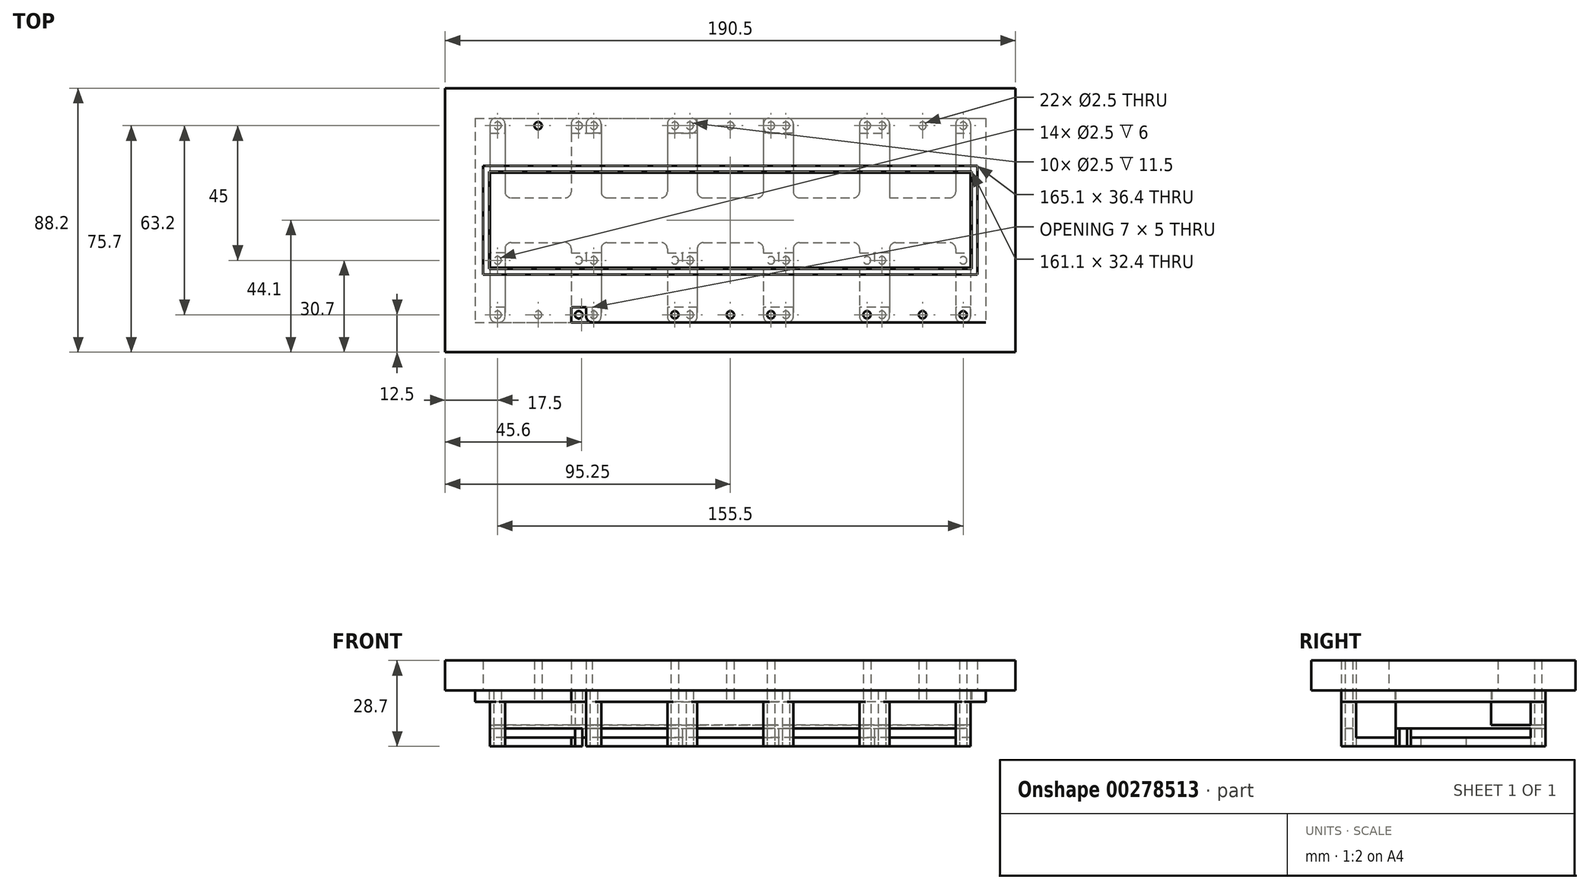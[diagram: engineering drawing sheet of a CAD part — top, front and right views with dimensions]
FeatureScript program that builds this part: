
annotation { "Feature Type Name" : "Feature", "Feature Type Description" : "" }
export const myFeature = defineFeature(function(context is Context, id is Id, definition is map)
    precondition{}
    {
        {
            var Q0;
            Q0=qCreatedBy(makeId("Top.planeOp"),FACE);
            var sketch = newSketch(context, id + "F0", { "sketchPlane" : qUnion([Q0])});
            skLineSegment(sketch, "E0.bottom", {"start": v(0, 0) * mm, "end": v(32.1, 0) * mm});
            skLineSegment(sketch, "E0.top", {"start": v(0, 50) * mm, "end": v(32.1, 50) * mm});
            skLineSegment(sketch, "E0.left", {"start": v(0, 0) * mm, "end": v(0, 50) * mm});
            skLineSegment(sketch, "E0.right", {"start": v(32.1, 0) * mm, "end": v(32.1, 50) * mm});
            skLineSegment(sketch, "E1", {"start": v(0, 31.8) * mm, "end": v(32.1, 31.8) * mm, "construction": true});
            skLineSegment(sketch, "E2", {"start": v(0, -18.2) * mm, "end": v(32.1, -18.2) * mm});
            skLineSegment(sketch, "E3", {"start": v(0, 0) * mm, "end": v(0, -18.2) * mm});
            skLineSegment(sketch, "E4", {"start": v(32.1, -18.2) * mm, "end": v(32.1, 0) * mm});
            skLineSegment(sketch, "E5", {"start": v(16.05, 50) * mm, "end": v(16.05, -18.2) * mm, "construction": true});
            skLineSegment(sketch, "E6", {"start": v(61.63, 15.9) * mm, "end": v(-27.1, 15.9) * mm, "construction": true});
            skPoint(sketch, "E6.startSnap0", {"position": v(16.05, 15.9) * mm});
            skCircle(sketch, "E7", {"center": v(2.5, 47.5) * mm, "radius": 1.25 * mm});
            skCircle(sketch, "E8.MirrorC", {"center": v(29.6, 47.5) * mm, "radius": 1.25 * mm});
            skCircle(sketch, "E9.MirrorC", {"center": v(29.6, -15.7) * mm, "radius": 1.25 * mm});
            skCircle(sketch, "E10.MirrorC", {"center": v(2.5, -15.7) * mm, "radius": 1.25 * mm});
            skCircle(sketch, "E11.1.0.0", {"center": v(61.7, 47.5) * mm, "radius": 1.25 * mm});
            skCircle(sketch, "E11.1.0.1", {"center": v(34.6, 47.5) * mm, "radius": 1.25 * mm});
            skCircle(sketch, "E11.1.0.2", {"center": v(34.6, -15.7) * mm, "radius": 1.25 * mm});
            skCircle(sketch, "E11.1.0.3", {"center": v(61.7, -15.7) * mm, "radius": 1.25 * mm});
            skLineSegment(sketch, "E11.1.0.4", {"start": v(32.1, 50) * mm, "end": v(64.2, 50) * mm});
            skLineSegment(sketch, "E11.1.0.5", {"start": v(32.1, -18.2) * mm, "end": v(64.2, -18.2) * mm});
            skCircle(sketch, "E11.2.0.0", {"center": v(93.8, 47.5) * mm, "radius": 1.25 * mm});
            skCircle(sketch, "E11.2.0.1", {"center": v(66.7, 47.5) * mm, "radius": 1.25 * mm});
            skCircle(sketch, "E11.2.0.2", {"center": v(66.7, -15.7) * mm, "radius": 1.25 * mm});
            skCircle(sketch, "E11.2.0.3", {"center": v(93.8, -15.7) * mm, "radius": 1.25 * mm});
            skLineSegment(sketch, "E11.2.0.4", {"start": v(64.2, 50) * mm, "end": v(96.3, 50) * mm});
            skLineSegment(sketch, "E11.2.0.5", {"start": v(64.2, -18.2) * mm, "end": v(96.3, -18.2) * mm});
            skCircle(sketch, "E11.3.0.0", {"center": v(125.9, 47.5) * mm, "radius": 1.25 * mm});
            skCircle(sketch, "E11.3.0.1", {"center": v(98.8, 47.5) * mm, "radius": 1.25 * mm});
            skCircle(sketch, "E11.3.0.2", {"center": v(98.8, -15.7) * mm, "radius": 1.25 * mm});
            skCircle(sketch, "E11.3.0.3", {"center": v(125.9, -15.7) * mm, "radius": 1.25 * mm});
            skLineSegment(sketch, "E11.3.0.4", {"start": v(96.3, 50) * mm, "end": v(128.4, 50) * mm});
            skLineSegment(sketch, "E11.3.0.5", {"start": v(96.3, -18.2) * mm, "end": v(128.4, -18.2) * mm});
            skCircle(sketch, "E11.4.0.0", {"center": v(158, 47.5) * mm, "radius": 1.25 * mm});
            skCircle(sketch, "E11.4.0.1", {"center": v(130.9, 47.5) * mm, "radius": 1.25 * mm});
            skCircle(sketch, "E11.4.0.2", {"center": v(130.9, -15.7) * mm, "radius": 1.25 * mm});
            skCircle(sketch, "E11.4.0.3", {"center": v(158, -15.7) * mm, "radius": 1.25 * mm});
            skLineSegment(sketch, "E11.4.0.4", {"start": v(128.4, 50) * mm, "end": v(160.5, 50) * mm});
            skLineSegment(sketch, "E11.4.0.5", {"start": v(128.4, -18.2) * mm, "end": v(160.5, -18.2) * mm});
            skLineSegment(sketch, "E11.direction1", {"start": v(29.6, 47.5) * mm, "end": v(61.7, 47.5) * mm, "construction": true});
            skLineSegment(sketch, "E12", {"start": v(160.5, 50) * mm, "end": v(160.5, -18.2) * mm});
            skSolve(sketch);
        }
        {
            var Q0;
            Q0=qCreatedBy(makeId("Top.planeOp"),FACE);
            var sketch = newSketch(context, id + "F1", { "sketchPlane" : qUnion([Q0])});
            skPoint(sketch, "E13.0", {"position": v(2.5, 47.5) * mm});
            skPoint(sketch, "E14.0", {"position": v(2.5, -15.7) * mm});
            skCircle(sketch, "E15", {"center": v(2.5, 47.5) * mm, "radius": 1.25 * mm});
            skCircle(sketch, "E16", {"center": v(2.5, -15.7) * mm, "radius": 1.25 * mm});
            skCircle(sketch, "E17", {"center": v(2.5, 2.5) * mm, "radius": 1.25 * mm});
            skCircle(sketch, "E18.MirrorC", {"center": v(29.6, 47.5) * mm, "radius": 1.25 * mm});
            skCircle(sketch, "E19.MirrorC", {"center": v(29.6, 2.5) * mm, "radius": 1.25 * mm});
            skCircle(sketch, "E20.MirrorC", {"center": v(29.6, -15.7) * mm, "radius": 1.25 * mm});
            skPoint(sketch, "E21.0", {"position": v(0, 50) * mm});
            skPoint(sketch, "E22.0", {"position": v(0, -18.2) * mm});
            skLineSegment(sketch, "E23.bottom", {"start": v(0, 50) * mm, "end": v(5, 50) * mm});
            skLineSegment(sketch, "E23.top", {"start": v(0, -18.2) * mm, "end": v(5, -18.2) * mm});
            skLineSegment(sketch, "E23.left", {"start": v(0, 50) * mm, "end": v(0, -18.2) * mm});
            skLineSegment(sketch, "E23.right", {"start": v(5, 50) * mm, "end": v(5, 23.4) * mm});
            skLineSegment(sketch, "E24.MirrorCS", {"start": v(27.1, 50) * mm, "end": v(27.1, 23.4) * mm});
            skLineSegment(sketch, "E25.MirrorCS", {"start": v(32.1, 50) * mm, "end": v(32.1, -18.2) * mm});
            skLineSegment(sketch, "E26.MirrorCS", {"start": v(32.1, 50) * mm, "end": v(27.1, 50) * mm});
            skLineSegment(sketch, "E27.MirrorCS", {"start": v(32.1, -18.2) * mm, "end": v(27.1, -18.2) * mm});
            skLineSegment(sketch, "E28", {"start": v(5, 23.4) * mm, "end": v(27.1, 23.4) * mm});
            skLineSegment(sketch, "E29", {"start": v(5, 15.9) * mm, "end": v(27.1, 15.9) * mm, "construction": true});
            skLineSegment(sketch, "E30.MirrorCS", {"start": v(5, 8.4) * mm, "end": v(27.1, 8.4) * mm});
            skLineSegment(sketch, "E31.trimOffspring", {"start": v(5, 8.4) * mm, "end": v(5, -18.2) * mm});
            skLineSegment(sketch, "E32.trimOffspring", {"start": v(27.1, 8.4) * mm, "end": v(27.1, -18.2) * mm});
            skPoint(sketch, "E33.1.0.0", {"position": v(32.1, -18.2) * mm});
            skLineSegment(sketch, "E33.1.0.1", {"start": v(37.1, 50) * mm, "end": v(37.1, 23.4) * mm});
            skPoint(sketch, "E33.1.0.2", {"position": v(34.6, -15.7) * mm});
            skLineSegment(sketch, "E33.1.0.3", {"start": v(59.2, 50) * mm, "end": v(59.2, 23.4) * mm});
            skLineSegment(sketch, "E33.1.0.4", {"start": v(64.2, 50) * mm, "end": v(64.2, -18.2) * mm});
            skPoint(sketch, "E33.1.0.5", {"position": v(34.6, 47.5) * mm});
            skLineSegment(sketch, "E33.1.0.6", {"start": v(64.2, 50) * mm, "end": v(59.2, 50) * mm});
            skPoint(sketch, "E33.1.0.7", {"position": v(32.1, 50) * mm});
            skLineSegment(sketch, "E33.1.0.8", {"start": v(37.1, 8.4) * mm, "end": v(37.1, -18.2) * mm});
            skLineSegment(sketch, "E33.1.0.9", {"start": v(59.2, 8.4) * mm, "end": v(59.2, -18.2) * mm});
            skLineSegment(sketch, "E33.1.0.10", {"start": v(37.1, 8.4) * mm, "end": v(59.2, 8.4) * mm});
            skLineSegment(sketch, "E33.1.0.11", {"start": v(64.2, -18.2) * mm, "end": v(59.2, -18.2) * mm});
            skLineSegment(sketch, "E33.1.0.12", {"start": v(37.1, 23.4) * mm, "end": v(59.2, 23.4) * mm});
            skLineSegment(sketch, "E33.1.0.13", {"start": v(37.1, 15.9) * mm, "end": v(59.2, 15.9) * mm, "construction": true});
            skLineSegment(sketch, "E33.1.0.15", {"start": v(32.1, -18.2) * mm, "end": v(37.1, -18.2) * mm});
            skCircle(sketch, "E33.1.0.16", {"center": v(34.6, 2.5) * mm, "radius": 1.25 * mm});
            skCircle(sketch, "E33.1.0.17", {"center": v(61.7, 47.5) * mm, "radius": 1.25 * mm});
            skCircle(sketch, "E33.1.0.18", {"center": v(61.7, 2.5) * mm, "radius": 1.25 * mm});
            skCircle(sketch, "E33.1.0.19", {"center": v(61.7, -15.7) * mm, "radius": 1.25 * mm});
            skLineSegment(sketch, "E33.1.0.20", {"start": v(32.1, 50) * mm, "end": v(37.1, 50) * mm});
            skCircle(sketch, "E33.1.0.21", {"center": v(34.6, 47.5) * mm, "radius": 1.25 * mm});
            skCircle(sketch, "E33.1.0.22", {"center": v(34.6, -15.7) * mm, "radius": 1.25 * mm});
            skPoint(sketch, "E33.2.0.0", {"position": v(64.2, -18.2) * mm});
            skLineSegment(sketch, "E33.2.0.1", {"start": v(69.2, 50) * mm, "end": v(69.2, 23.4) * mm});
            skPoint(sketch, "E33.2.0.2", {"position": v(66.7, -15.7) * mm});
            skLineSegment(sketch, "E33.2.0.3", {"start": v(91.3, 50) * mm, "end": v(91.3, 23.4) * mm});
            skLineSegment(sketch, "E33.2.0.4", {"start": v(96.3, 50) * mm, "end": v(96.3, -18.2) * mm});
            skPoint(sketch, "E33.2.0.5", {"position": v(66.7, 47.5) * mm});
            skLineSegment(sketch, "E33.2.0.6", {"start": v(96.3, 50) * mm, "end": v(91.3, 50) * mm});
            skPoint(sketch, "E33.2.0.7", {"position": v(64.2, 50) * mm});
            skLineSegment(sketch, "E33.2.0.8", {"start": v(69.2, 8.4) * mm, "end": v(69.2, -18.2) * mm});
            skLineSegment(sketch, "E33.2.0.9", {"start": v(91.3, 8.4) * mm, "end": v(91.3, -18.2) * mm});
            skLineSegment(sketch, "E33.2.0.10", {"start": v(69.2, 8.4) * mm, "end": v(91.3, 8.4) * mm});
            skLineSegment(sketch, "E33.2.0.11", {"start": v(96.3, -18.2) * mm, "end": v(91.3, -18.2) * mm});
            skLineSegment(sketch, "E33.2.0.12", {"start": v(69.2, 23.4) * mm, "end": v(91.3, 23.4) * mm});
            skLineSegment(sketch, "E33.2.0.13", {"start": v(69.2, 15.9) * mm, "end": v(91.3, 15.9) * mm, "construction": true});
            skLineSegment(sketch, "E33.2.0.14", {"start": v(64.2, 50) * mm, "end": v(64.2, -18.2) * mm});
            skLineSegment(sketch, "E33.2.0.15", {"start": v(64.2, -18.2) * mm, "end": v(69.2, -18.2) * mm});
            skCircle(sketch, "E33.2.0.16", {"center": v(66.7, 2.5) * mm, "radius": 1.25 * mm});
            skCircle(sketch, "E33.2.0.17", {"center": v(93.8, 47.5) * mm, "radius": 1.25 * mm});
            skCircle(sketch, "E33.2.0.18", {"center": v(93.8, 2.5) * mm, "radius": 1.25 * mm});
            skCircle(sketch, "E33.2.0.19", {"center": v(93.8, -15.7) * mm, "radius": 1.25 * mm});
            skLineSegment(sketch, "E33.2.0.20", {"start": v(64.2, 50) * mm, "end": v(69.2, 50) * mm});
            skCircle(sketch, "E33.2.0.21", {"center": v(66.7, 47.5) * mm, "radius": 1.25 * mm});
            skCircle(sketch, "E33.2.0.22", {"center": v(66.7, -15.7) * mm, "radius": 1.25 * mm});
            skPoint(sketch, "E33.3.0.0", {"position": v(96.3, -18.2) * mm});
            skLineSegment(sketch, "E33.3.0.1", {"start": v(101.3, 50) * mm, "end": v(101.3, 23.4) * mm});
            skPoint(sketch, "E33.3.0.2", {"position": v(98.8, -15.7) * mm});
            skLineSegment(sketch, "E33.3.0.3", {"start": v(123.4, 50) * mm, "end": v(123.4, 23.4) * mm});
            skLineSegment(sketch, "E33.3.0.4", {"start": v(128.4, 50) * mm, "end": v(128.4, -18.2) * mm});
            skPoint(sketch, "E33.3.0.5", {"position": v(98.8, 47.5) * mm});
            skLineSegment(sketch, "E33.3.0.6", {"start": v(128.4, 50) * mm, "end": v(123.4, 50) * mm});
            skPoint(sketch, "E33.3.0.7", {"position": v(96.3, 50) * mm});
            skLineSegment(sketch, "E33.3.0.8", {"start": v(101.3, 8.4) * mm, "end": v(101.3, -18.2) * mm});
            skLineSegment(sketch, "E33.3.0.9", {"start": v(123.4, 8.4) * mm, "end": v(123.4, -18.2) * mm});
            skLineSegment(sketch, "E33.3.0.10", {"start": v(101.3, 8.4) * mm, "end": v(123.4, 8.4) * mm});
            skLineSegment(sketch, "E33.3.0.11", {"start": v(128.4, -18.2) * mm, "end": v(123.4, -18.2) * mm});
            skLineSegment(sketch, "E33.3.0.12", {"start": v(101.3, 23.4) * mm, "end": v(123.4, 23.4) * mm});
            skLineSegment(sketch, "E33.3.0.13", {"start": v(101.3, 15.9) * mm, "end": v(123.4, 15.9) * mm, "construction": true});
            skLineSegment(sketch, "E33.3.0.14", {"start": v(96.3, 50) * mm, "end": v(96.3, -18.2) * mm});
            skLineSegment(sketch, "E33.3.0.15", {"start": v(96.3, -18.2) * mm, "end": v(101.3, -18.2) * mm});
            skCircle(sketch, "E33.3.0.16", {"center": v(98.8, 2.5) * mm, "radius": 1.25 * mm});
            skCircle(sketch, "E33.3.0.17", {"center": v(125.9, 47.5) * mm, "radius": 1.25 * mm});
            skCircle(sketch, "E33.3.0.18", {"center": v(125.9, 2.5) * mm, "radius": 1.25 * mm});
            skCircle(sketch, "E33.3.0.19", {"center": v(125.9, -15.7) * mm, "radius": 1.25 * mm});
            skLineSegment(sketch, "E33.3.0.20", {"start": v(96.3, 50) * mm, "end": v(101.3, 50) * mm});
            skCircle(sketch, "E33.3.0.21", {"center": v(98.8, 47.5) * mm, "radius": 1.25 * mm});
            skCircle(sketch, "E33.3.0.22", {"center": v(98.8, -15.7) * mm, "radius": 1.25 * mm});
            skPoint(sketch, "E33.4.0.0", {"position": v(128.4, -18.2) * mm});
            skLineSegment(sketch, "E33.4.0.1", {"start": v(133.4, 50) * mm, "end": v(133.4, 23.4) * mm});
            skPoint(sketch, "E33.4.0.2", {"position": v(130.9, -15.7) * mm});
            skLineSegment(sketch, "E33.4.0.3", {"start": v(155.5, 50) * mm, "end": v(155.5, 23.4) * mm});
            skLineSegment(sketch, "E33.4.0.4", {"start": v(160.5, 50) * mm, "end": v(160.5, -18.2) * mm});
            skPoint(sketch, "E33.4.0.5", {"position": v(130.9, 47.5) * mm});
            skLineSegment(sketch, "E33.4.0.6", {"start": v(160.5, 50) * mm, "end": v(155.5, 50) * mm});
            skPoint(sketch, "E33.4.0.7", {"position": v(128.4, 50) * mm});
            skLineSegment(sketch, "E33.4.0.8", {"start": v(133.4, 8.4) * mm, "end": v(133.4, -18.2) * mm});
            skLineSegment(sketch, "E33.4.0.9", {"start": v(155.5, 8.4) * mm, "end": v(155.5, -18.2) * mm});
            skLineSegment(sketch, "E33.4.0.10", {"start": v(133.4, 8.4) * mm, "end": v(155.5, 8.4) * mm});
            skLineSegment(sketch, "E33.4.0.11", {"start": v(160.5, -18.2) * mm, "end": v(155.5, -18.2) * mm});
            skLineSegment(sketch, "E33.4.0.12", {"start": v(133.4, 23.4) * mm, "end": v(155.5, 23.4) * mm});
            skLineSegment(sketch, "E33.4.0.13", {"start": v(133.4, 15.9) * mm, "end": v(155.5, 15.9) * mm, "construction": true});
            skLineSegment(sketch, "E33.4.0.14", {"start": v(128.4, 50) * mm, "end": v(128.4, -18.2) * mm});
            skLineSegment(sketch, "E33.4.0.15", {"start": v(128.4, -18.2) * mm, "end": v(133.4, -18.2) * mm});
            skCircle(sketch, "E33.4.0.16", {"center": v(130.9, 2.5) * mm, "radius": 1.25 * mm});
            skCircle(sketch, "E33.4.0.17", {"center": v(158, 47.5) * mm, "radius": 1.25 * mm});
            skCircle(sketch, "E33.4.0.18", {"center": v(158, 2.5) * mm, "radius": 1.25 * mm});
            skCircle(sketch, "E33.4.0.19", {"center": v(158, -15.7) * mm, "radius": 1.25 * mm});
            skLineSegment(sketch, "E33.4.0.20", {"start": v(128.4, 50) * mm, "end": v(133.4, 50) * mm});
            skCircle(sketch, "E33.4.0.21", {"center": v(130.9, 47.5) * mm, "radius": 1.25 * mm});
            skCircle(sketch, "E33.4.0.22", {"center": v(130.9, -15.7) * mm, "radius": 1.25 * mm});
            skLineSegment(sketch, "E33.direction1", {"start": v(0, -18.2) * mm, "end": v(32.1, -18.2) * mm, "construction": true});
            skLineSegment(sketch, "E34", {"start": v(0, 45) * mm, "end": v(5, 45) * mm});
            skLineSegment(sketch, "E35.trimOffspring", {"start": v(27.1, 45) * mm, "end": v(37.1, 45) * mm});
            skLineSegment(sketch, "E36.trimOffspring", {"start": v(59.2, 45) * mm, "end": v(69.2, 45) * mm});
            skLineSegment(sketch, "E37.trimOffspring", {"start": v(91.3, 45) * mm, "end": v(101.3, 45) * mm});
            skLineSegment(sketch, "E38.trimOffspring", {"start": v(123.4, 45) * mm, "end": v(133.4, 45) * mm});
            skLineSegment(sketch, "E39.trimOffspring", {"start": v(155.5, 45) * mm, "end": v(160.5, 45) * mm});
            skLineSegment(sketch, "E40.MirrorCS", {"start": v(0, -13.2) * mm, "end": v(5, -13.2) * mm});
            skLineSegment(sketch, "E41.MirrorCS", {"start": v(27.1, -13.2) * mm, "end": v(37.1, -13.2) * mm});
            skLineSegment(sketch, "E42.MirrorCS", {"start": v(59.2, -13.2) * mm, "end": v(69.2, -13.2) * mm});
            skLineSegment(sketch, "E43.MirrorCS", {"start": v(91.3, -13.2) * mm, "end": v(101.3, -13.2) * mm});
            skLineSegment(sketch, "E44.MirrorCS", {"start": v(123.4, -13.2) * mm, "end": v(133.4, -13.2) * mm});
            skLineSegment(sketch, "E45.MirrorCS", {"start": v(155.5, -13.2) * mm, "end": v(160.5, -13.2) * mm});
            skLineSegment(sketch, "E46", {"start": v(2.5, 2.5) * mm, "end": v(29.6, 2.5) * mm, "construction": true});
            skLineSegment(sketch, "E47", {"start": v(0, 5) * mm, "end": v(5, 5) * mm});
            skLineSegment(sketch, "E48.MirrorCS", {"start": v(0, 0) * mm, "end": v(5, 0) * mm});
            skPoint(sketch, "E49.orphan", {"position": v(-13.99, 5) * mm});
            skPoint(sketch, "E50.orphan", {"position": v(-13.99, 0) * mm});
            skLineSegment(sketch, "E51.trimOffspring", {"start": v(27.1, 5) * mm, "end": v(37.1, 5) * mm});
            skLineSegment(sketch, "E52.trimOffspring", {"start": v(27.1, 0) * mm, "end": v(37.1, 0) * mm});
            skLineSegment(sketch, "E53.trimOffspring", {"start": v(59.2, 5) * mm, "end": v(69.2, 5) * mm});
            skLineSegment(sketch, "E54.trimOffspring", {"start": v(59.2, 0) * mm, "end": v(69.2, 0) * mm});
            skLineSegment(sketch, "E55.trimOffspring", {"start": v(91.3, 5) * mm, "end": v(101.3, 5) * mm});
            skLineSegment(sketch, "E56.trimOffspring", {"start": v(91.3, 0) * mm, "end": v(101.3, 0) * mm});
            skLineSegment(sketch, "E57.trimOffspring", {"start": v(123.4, 5) * mm, "end": v(133.4, 5) * mm});
            skLineSegment(sketch, "E58.trimOffspring", {"start": v(123.4, 0) * mm, "end": v(133.4, 0) * mm});
            skLineSegment(sketch, "E59.trimOffspring", {"start": v(155.5, 5) * mm, "end": v(160.5, 5) * mm});
            skLineSegment(sketch, "E60.trimOffspring", {"start": v(155.5, 0) * mm, "end": v(160.5, 0) * mm});
            skPoint(sketch, "E61.orphan", {"position": v(172.12, 5) * mm});
            skPoint(sketch, "E62.orphan", {"position": v(172.12, 0) * mm});
            skSolve(sketch);
        }
        {
            var Q0;
            Q0=makeQuery(id+"F1.imprint","IMPRINT",FACE,{"disambiguationData":[TD([[makeQuery(id+"F1.imprint","IMPRINT",EDGE,{"derivedFrom":sQuery(id+"F1.wireOp",EDGE,"E15")}),-1.0]])]});
            var Q1;
            Q1=makeQuery(id+"F1.imprint","IMPRINT",FACE,{"disambiguationData":[TD([[makeQuery(id+"F1.imprint","IMPRINT",EDGE,{"derivedFrom":sQuery(id+"F1.wireOp",EDGE,"E33.1.0.1")}),-1.0]])]});
            var Q2;
            Q2=makeQuery(id+"F1.imprint","IMPRINT",FACE,{"disambiguationData":[TD([[makeQuery(id+"F1.imprint","IMPRINT",EDGE,{"derivedFrom":sQuery(id+"F1.wireOp",EDGE,"E33.3.0.1")}),-1.0]])]});
            var Q3;
            Q3=makeQuery(id+"F1.imprint","IMPRINT",FACE,{"disambiguationData":[TD([[makeQuery(id+"F1.imprint","IMPRINT",EDGE,{"derivedFrom":sQuery(id+"F1.wireOp",EDGE,"E33.2.0.1")}),-1.0]])]});
            var Q4;
            Q4=makeQuery(id+"F1.imprint","IMPRINT",FACE,{"disambiguationData":[TD([[makeQuery(id+"F1.imprint","IMPRINT",EDGE,{"derivedFrom":sQuery(id+"F1.wireOp",EDGE,"E33.4.0.1")}),-1.0]])]});
            var Q5;
            {var subQ12=sQuery(id+"F1.wireOp",EDGE,"E28");Q5=makeQuery(id+"F1.imprint","IMPRINT",FACE,{"disambiguationData":[TD([[makeQuery(id+"F1.imprint","IMPRINT",EDGE,{"derivedFrom":subQ12}),-1.0]])]});}
            var Q6;
            {var subQ15=sQuery(id+"F1.wireOp",EDGE,"E33.2.0.10");Q6=makeQuery(id+"F1.imprint","IMPRINT",FACE,{"disambiguationData":[TD([[makeQuery(id+"F1.imprint","IMPRINT",EDGE,{"derivedFrom":subQ15}),1.0]])]});}
            var Q7;
            {var subQ5=sQuery(id+"F1.wireOp",EDGE,"E33.3.0.10");Q7=makeQuery(id+"F1.imprint","IMPRINT",FACE,{"disambiguationData":[TD([[makeQuery(id+"F1.imprint","IMPRINT",EDGE,{"derivedFrom":subQ5}),1.0]])]});}
            var Q8;
            {var subQ9=sQuery(id+"F1.wireOp",EDGE,"E33.4.0.10");Q8=makeQuery(id+"F1.imprint","IMPRINT",FACE,{"disambiguationData":[TD([[makeQuery(id+"F1.imprint","IMPRINT",EDGE,{"derivedFrom":subQ9}),1.0]])]});}
            var Q9;
            Q9=makeQuery(id+"F1.imprint","IMPRINT",FACE,{"disambiguationData":[TD([[makeQuery(id+"F1.imprint","IMPRINT",EDGE,{"derivedFrom":sQuery(id+"F1.wireOp",EDGE,"E18.MirrorC")}),1.0]])]});
            var Q10;
            {var subQ1=sQuery(id+"F1.wireOp",EDGE,"E33.1.0.6");Q10=makeQuery(id+"F1.imprint","IMPRINT",FACE,{"disambiguationData":[TD([[makeQuery(id+"F1.imprint","IMPRINT",EDGE,{"derivedFrom":subQ1}),1.0]])]});}
            var Q11;
            {var subQ1=sQuery(id+"F1.wireOp",EDGE,"E33.2.0.6");Q11=makeQuery(id+"F1.imprint","IMPRINT",FACE,{"disambiguationData":[TD([[makeQuery(id+"F1.imprint","IMPRINT",EDGE,{"derivedFrom":subQ1}),1.0]])]});}
            var Q12;
            {var subQ1=sQuery(id+"F1.wireOp",EDGE,"E33.3.0.6");Q12=makeQuery(id+"F1.imprint","IMPRINT",FACE,{"disambiguationData":[TD([[makeQuery(id+"F1.imprint","IMPRINT",EDGE,{"derivedFrom":subQ1}),1.0]])]});}
            var Q13;
            {var subQ0=sQuery(id+"F1.wireOp",EDGE,"E33.4.0.6");Q13=makeQuery(id+"F1.imprint","IMPRINT",FACE,{"disambiguationData":[TD([[makeQuery(id+"F1.imprint","IMPRINT",EDGE,{"derivedFrom":subQ0}),1.0]])]});}
            var Q14;
            {var subQ13=sQuery(id+"F1.wireOp",EDGE,"E33.1.0.10");Q14=makeQuery(id+"F1.imprint","IMPRINT",FACE,{"disambiguationData":[TD([[makeQuery(id+"F1.imprint","IMPRINT",EDGE,{"derivedFrom":subQ13}),1.0]])]});}
            var Q15;
            {var subQ0=sQuery(id+"F1.wireOp",EDGE,"E40.MirrorCS");Q15=makeQuery(id+"F1.imprint","IMPRINT",FACE,{"disambiguationData":[TD([[makeQuery(id+"F1.imprint","IMPRINT",EDGE,{"derivedFrom":subQ0}),1.0]])]});}
            var Q16;
            {var subQ0=sQuery(id+"F1.wireOp",EDGE,"E41.MirrorCS");var subQ1=sQuery(id+"F1.wireOp",EDGE,"E32.trimOffspring");var subQ2=makeQuery(id+"F1.imprint","INTERSECT",VERTEX,{"derivedFrom":[subQ1,subQ0]});Q16=makeQuery(id+"F1.imprint","IMPRINT",FACE,{"disambiguationData":[TD([[makeQuery(id+"F1.imprint","IMPRINT",EDGE,{"disambiguationData":[TD([[subQ2,1.0]])],"derivedFrom":subQ1}),1.0]])]});}
            var Q17;
            {var subQ0=sQuery(id+"F1.wireOp",EDGE,"E41.MirrorCS");var subQ1=sQuery(id+"F1.wireOp",EDGE,"E33.1.0.8");var subQ2=makeQuery(id+"F1.imprint","INTERSECT",VERTEX,{"derivedFrom":[subQ1,subQ0]});Q17=makeQuery(id+"F1.imprint","IMPRINT",FACE,{"disambiguationData":[TD([[makeQuery(id+"F1.imprint","IMPRINT",EDGE,{"disambiguationData":[TD([[subQ2,1.0]])],"derivedFrom":subQ1}),-1.0]])]});}
            var Q18;
            {var subQ0=sQuery(id+"F1.wireOp",EDGE,"E42.MirrorCS");var subQ1=sQuery(id+"F1.wireOp",EDGE,"E33.1.0.9");var subQ2=makeQuery(id+"F1.imprint","INTERSECT",VERTEX,{"derivedFrom":[subQ1,subQ0]});Q18=makeQuery(id+"F1.imprint","IMPRINT",FACE,{"disambiguationData":[TD([[makeQuery(id+"F1.imprint","IMPRINT",EDGE,{"disambiguationData":[TD([[subQ2,1.0]])],"derivedFrom":subQ1}),1.0]])]});}
            var Q19;
            {var subQ0=sQuery(id+"F1.wireOp",EDGE,"E43.MirrorCS");var subQ1=sQuery(id+"F1.wireOp",EDGE,"E33.3.0.8");var subQ2=makeQuery(id+"F1.imprint","INTERSECT",VERTEX,{"derivedFrom":[subQ1,subQ0]});Q19=makeQuery(id+"F1.imprint","IMPRINT",FACE,{"disambiguationData":[TD([[makeQuery(id+"F1.imprint","IMPRINT",EDGE,{"disambiguationData":[TD([[subQ2,1.0]])],"derivedFrom":subQ1}),-1.0]])]});}
            var Q20;
            {var subQ0=sQuery(id+"F1.wireOp",EDGE,"E44.MirrorCS");var subQ1=sQuery(id+"F1.wireOp",EDGE,"E33.3.0.9");var subQ2=makeQuery(id+"F1.imprint","INTERSECT",VERTEX,{"derivedFrom":[subQ1,subQ0]});Q20=makeQuery(id+"F1.imprint","IMPRINT",FACE,{"disambiguationData":[TD([[makeQuery(id+"F1.imprint","IMPRINT",EDGE,{"disambiguationData":[TD([[subQ2,1.0]])],"derivedFrom":subQ1}),1.0]])]});}
            var Q21;
            {var subQ0=sQuery(id+"F1.wireOp",EDGE,"E44.MirrorCS");var subQ1=sQuery(id+"F1.wireOp",EDGE,"E33.4.0.8");var subQ2=makeQuery(id+"F1.imprint","INTERSECT",VERTEX,{"derivedFrom":[subQ1,subQ0]});Q21=makeQuery(id+"F1.imprint","IMPRINT",FACE,{"disambiguationData":[TD([[makeQuery(id+"F1.imprint","IMPRINT",EDGE,{"disambiguationData":[TD([[subQ2,1.0]])],"derivedFrom":subQ1}),-1.0]])]});}
            var Q22;
            {var subQ0=sQuery(id+"F1.wireOp",EDGE,"E45.MirrorCS");Q22=makeQuery(id+"F1.imprint","IMPRINT",FACE,{"disambiguationData":[TD([[makeQuery(id+"F1.imprint","IMPRINT",EDGE,{"derivedFrom":subQ0}),1.0]])]});}
            var Q23;
            Q23=makeQuery(id+"F1.imprint","IMPRINT",FACE,{"disambiguationData":[TD([[makeQuery(id+"F1.imprint","IMPRINT",EDGE,{"derivedFrom":sQuery(id+"F1.wireOp",EDGE,"E17")}),-1.0]])]});
            var Q24;
            Q24=makeQuery(id+"F1.imprint","IMPRINT",FACE,{"disambiguationData":[TD([[makeQuery(id+"F1.imprint","IMPRINT",EDGE,{"derivedFrom":sQuery(id+"F1.wireOp",EDGE,"E16")}),-1.0]])]});
            var Q25;
            Q25=makeQuery(id+"F1.imprint","IMPRINT",FACE,{"disambiguationData":[TD([[makeQuery(id+"F1.imprint","IMPRINT",EDGE,{"derivedFrom":sQuery(id+"F1.wireOp",EDGE,"E19.MirrorC")}),1.0]])]});
            var Q26;
            Q26=makeQuery(id+"F1.imprint","IMPRINT",FACE,{"disambiguationData":[TD([[makeQuery(id+"F1.imprint","IMPRINT",EDGE,{"derivedFrom":sQuery(id+"F1.wireOp",EDGE,"E33.1.0.16")}),-1.0]])]});
            var Q27;
            Q27=makeQuery(id+"F1.imprint","IMPRINT",FACE,{"disambiguationData":[TD([[makeQuery(id+"F1.imprint","IMPRINT",EDGE,{"derivedFrom":sQuery(id+"F1.wireOp",EDGE,"E20.MirrorC")}),1.0]])]});
            var Q28;
            {var subQ0=sQuery(id+"F1.wireOp",EDGE,"E33.1.0.15");Q28=makeQuery(id+"F1.imprint","IMPRINT",FACE,{"disambiguationData":[TD([[makeQuery(id+"F1.imprint","IMPRINT",EDGE,{"derivedFrom":subQ0}),1.0]])]});}
            var Q29;
            {var subQ0=sQuery(id+"F1.wireOp",EDGE,"E33.1.0.11");Q29=makeQuery(id+"F1.imprint","IMPRINT",FACE,{"disambiguationData":[TD([[makeQuery(id+"F1.imprint","IMPRINT",EDGE,{"derivedFrom":subQ0}),-1.0]])]});}
            var Q30;
            Q30=makeQuery(id+"F1.imprint","IMPRINT",FACE,{"disambiguationData":[TD([[makeQuery(id+"F1.imprint","IMPRINT",EDGE,{"derivedFrom":sQuery(id+"F1.wireOp",EDGE,"E33.1.0.18")}),1.0]])]});
            var Q31;
            Q31=makeQuery(id+"F1.imprint","IMPRINT",FACE,{"disambiguationData":[TD([[makeQuery(id+"F1.imprint","IMPRINT",EDGE,{"derivedFrom":sQuery(id+"F1.wireOp",EDGE,"E33.2.0.16")}),-1.0]])]});
            var Q32;
            {var subQ0=sQuery(id+"F1.wireOp",EDGE,"E33.2.0.15");Q32=makeQuery(id+"F1.imprint","IMPRINT",FACE,{"disambiguationData":[TD([[makeQuery(id+"F1.imprint","IMPRINT",EDGE,{"derivedFrom":subQ0}),1.0]])]});}
            var Q33;
            {var subQ0=sQuery(id+"F1.wireOp",EDGE,"E33.2.0.11");Q33=makeQuery(id+"F1.imprint","IMPRINT",FACE,{"disambiguationData":[TD([[makeQuery(id+"F1.imprint","IMPRINT",EDGE,{"derivedFrom":subQ0}),-1.0]])]});}
            var Q34;
            Q34=makeQuery(id+"F1.imprint","IMPRINT",FACE,{"disambiguationData":[TD([[makeQuery(id+"F1.imprint","IMPRINT",EDGE,{"derivedFrom":sQuery(id+"F1.wireOp",EDGE,"E33.2.0.18")}),1.0]])]});
            var Q35;
            Q35=makeQuery(id+"F1.imprint","IMPRINT",FACE,{"disambiguationData":[TD([[makeQuery(id+"F1.imprint","IMPRINT",EDGE,{"derivedFrom":sQuery(id+"F1.wireOp",EDGE,"E33.3.0.16")}),-1.0]])]});
            var Q36;
            {var subQ0=sQuery(id+"F1.wireOp",EDGE,"E33.3.0.15");Q36=makeQuery(id+"F1.imprint","IMPRINT",FACE,{"disambiguationData":[TD([[makeQuery(id+"F1.imprint","IMPRINT",EDGE,{"derivedFrom":subQ0}),1.0]])]});}
            var Q37;
            {var subQ0=sQuery(id+"F1.wireOp",EDGE,"E43.MirrorCS");var subQ1=sQuery(id+"F1.wireOp",EDGE,"E33.2.0.9");var subQ2=makeQuery(id+"F1.imprint","INTERSECT",VERTEX,{"derivedFrom":[subQ1,subQ0]});Q37=makeQuery(id+"F1.imprint","IMPRINT",FACE,{"disambiguationData":[TD([[makeQuery(id+"F1.imprint","IMPRINT",EDGE,{"disambiguationData":[TD([[subQ2,1.0]])],"derivedFrom":subQ1}),1.0]])]});}
            var Q38;
            {var subQ0=sQuery(id+"F1.wireOp",EDGE,"E42.MirrorCS");var subQ1=sQuery(id+"F1.wireOp",EDGE,"E33.2.0.8");var subQ2=makeQuery(id+"F1.imprint","INTERSECT",VERTEX,{"derivedFrom":[subQ1,subQ0]});Q38=makeQuery(id+"F1.imprint","IMPRINT",FACE,{"disambiguationData":[TD([[makeQuery(id+"F1.imprint","IMPRINT",EDGE,{"disambiguationData":[TD([[subQ2,1.0]])],"derivedFrom":subQ1}),-1.0]])]});}
            var Q39;
            Q39=makeQuery(id+"F1.imprint","IMPRINT",FACE,{"disambiguationData":[TD([[makeQuery(id+"F1.imprint","IMPRINT",EDGE,{"derivedFrom":sQuery(id+"F1.wireOp",EDGE,"E33.4.0.16")}),-1.0]])]});
            var Q40;
            {var subQ0=sQuery(id+"F1.wireOp",EDGE,"E33.4.0.15");Q40=makeQuery(id+"F1.imprint","IMPRINT",FACE,{"disambiguationData":[TD([[makeQuery(id+"F1.imprint","IMPRINT",EDGE,{"derivedFrom":subQ0}),1.0]])]});}
            var Q41;
            {var subQ0=sQuery(id+"F1.wireOp",EDGE,"E33.3.0.11");Q41=makeQuery(id+"F1.imprint","IMPRINT",FACE,{"disambiguationData":[TD([[makeQuery(id+"F1.imprint","IMPRINT",EDGE,{"derivedFrom":subQ0}),-1.0]])]});}
            var Q42;
            Q42=makeQuery(id+"F1.imprint","IMPRINT",FACE,{"disambiguationData":[TD([[makeQuery(id+"F1.imprint","IMPRINT",EDGE,{"derivedFrom":sQuery(id+"F1.wireOp",EDGE,"E33.4.0.18")}),1.0]])]});
            var Q43;
            {var subQ0=sQuery(id+"F1.wireOp",EDGE,"E33.4.0.11");Q43=makeQuery(id+"F1.imprint","IMPRINT",FACE,{"disambiguationData":[TD([[makeQuery(id+"F1.imprint","IMPRINT",EDGE,{"derivedFrom":subQ0}),-1.0]])]});}
            var Q44;
            Q44=makeQuery(id+"F1.imprint","IMPRINT",FACE,{"disambiguationData":[TD([[makeQuery(id+"F1.imprint","IMPRINT",EDGE,{"derivedFrom":sQuery(id+"F1.wireOp",EDGE,"E33.3.0.18")}),1.0]])]});
            extrude(context, id + "F2", {"entities" : qUnion([Q0, Q1, Q2, Q3, Q4, Q5, Q6, Q7, Q8, Q9, Q10, Q11, Q12, Q13, Q14, Q15, Q16, Q17, Q18, Q19, Q20, Q21, Q22, Q23, Q24, Q25, Q26, Q27, Q28, Q29, Q30, Q31, Q32, Q33, Q34, Q35, Q36, Q37, Q38, Q39, Q40, Q41, Q42, Q43, Q44]), "depth" : 3 * mm, "offsetDistance" : 25 * mm});
        }
        {
            var Q0;
            Q0=makeQuery(id+"F1.imprint","IMPRINT",FACE,{"disambiguationData":[TD([[makeQuery(id+"F1.imprint","IMPRINT",EDGE,{"derivedFrom":sQuery(id+"F1.wireOp",EDGE,"E15")}),-1.0]])]});
            var Q1;
            Q1=makeQuery(id+"F1.imprint","IMPRINT",FACE,{"disambiguationData":[TD([[makeQuery(id+"F1.imprint","IMPRINT",EDGE,{"derivedFrom":sQuery(id+"F1.wireOp",EDGE,"E18.MirrorC")}),1.0]])]});
            var Q2;
            {var subQ0=sQuery(id+"F1.wireOp",EDGE,"E33.1.0.20");Q2=makeQuery(id+"F1.imprint","IMPRINT",FACE,{"disambiguationData":[TD([[makeQuery(id+"F1.imprint","IMPRINT",EDGE,{"derivedFrom":subQ0}),-1.0]])]});}
            var Q3;
            {var subQ1=sQuery(id+"F1.wireOp",EDGE,"E33.1.0.6");Q3=makeQuery(id+"F1.imprint","IMPRINT",FACE,{"disambiguationData":[TD([[makeQuery(id+"F1.imprint","IMPRINT",EDGE,{"derivedFrom":subQ1}),1.0]])]});}
            var Q4;
            {var subQ0=sQuery(id+"F1.wireOp",EDGE,"E33.2.0.20");Q4=makeQuery(id+"F1.imprint","IMPRINT",FACE,{"disambiguationData":[TD([[makeQuery(id+"F1.imprint","IMPRINT",EDGE,{"derivedFrom":subQ0}),-1.0]])]});}
            var Q5;
            {var subQ0=sQuery(id+"F1.wireOp",EDGE,"E33.3.0.20");Q5=makeQuery(id+"F1.imprint","IMPRINT",FACE,{"disambiguationData":[TD([[makeQuery(id+"F1.imprint","IMPRINT",EDGE,{"derivedFrom":subQ0}),-1.0]])]});}
            var Q6;
            {var subQ1=sQuery(id+"F1.wireOp",EDGE,"E33.3.0.6");Q6=makeQuery(id+"F1.imprint","IMPRINT",FACE,{"disambiguationData":[TD([[makeQuery(id+"F1.imprint","IMPRINT",EDGE,{"derivedFrom":subQ1}),1.0]])]});}
            var Q7;
            {var subQ0=sQuery(id+"F1.wireOp",EDGE,"E33.4.0.20");Q7=makeQuery(id+"F1.imprint","IMPRINT",FACE,{"disambiguationData":[TD([[makeQuery(id+"F1.imprint","IMPRINT",EDGE,{"derivedFrom":subQ0}),-1.0]])]});}
            var Q8;
            {var subQ1=sQuery(id+"F1.wireOp",EDGE,"E33.2.0.6");Q8=makeQuery(id+"F1.imprint","IMPRINT",FACE,{"disambiguationData":[TD([[makeQuery(id+"F1.imprint","IMPRINT",EDGE,{"derivedFrom":subQ1}),1.0]])]});}
            var Q9;
            {var subQ0=sQuery(id+"F1.wireOp",EDGE,"E33.4.0.6");Q9=makeQuery(id+"F1.imprint","IMPRINT",FACE,{"disambiguationData":[TD([[makeQuery(id+"F1.imprint","IMPRINT",EDGE,{"derivedFrom":subQ0}),1.0]])]});}
            var Q10;
            Q10=makeQuery(id+"F1.imprint","IMPRINT",FACE,{"disambiguationData":[TD([[makeQuery(id+"F1.imprint","IMPRINT",EDGE,{"derivedFrom":sQuery(id+"F1.wireOp",EDGE,"E33.4.0.18")}),1.0]])]});
            var Q11;
            Q11=makeQuery(id+"F1.imprint","IMPRINT",FACE,{"disambiguationData":[TD([[makeQuery(id+"F1.imprint","IMPRINT",EDGE,{"derivedFrom":sQuery(id+"F1.wireOp",EDGE,"E33.4.0.16")}),-1.0]])]});
            var Q12;
            Q12=makeQuery(id+"F1.imprint","IMPRINT",FACE,{"disambiguationData":[TD([[makeQuery(id+"F1.imprint","IMPRINT",EDGE,{"derivedFrom":sQuery(id+"F1.wireOp",EDGE,"E33.3.0.18")}),1.0]])]});
            var Q13;
            Q13=makeQuery(id+"F1.imprint","IMPRINT",FACE,{"disambiguationData":[TD([[makeQuery(id+"F1.imprint","IMPRINT",EDGE,{"derivedFrom":sQuery(id+"F1.wireOp",EDGE,"E33.3.0.16")}),-1.0]])]});
            var Q14;
            Q14=makeQuery(id+"F1.imprint","IMPRINT",FACE,{"disambiguationData":[TD([[makeQuery(id+"F1.imprint","IMPRINT",EDGE,{"derivedFrom":sQuery(id+"F1.wireOp",EDGE,"E33.2.0.18")}),1.0]])]});
            var Q15;
            Q15=makeQuery(id+"F1.imprint","IMPRINT",FACE,{"disambiguationData":[TD([[makeQuery(id+"F1.imprint","IMPRINT",EDGE,{"derivedFrom":sQuery(id+"F1.wireOp",EDGE,"E33.2.0.16")}),-1.0]])]});
            var Q16;
            Q16=makeQuery(id+"F1.imprint","IMPRINT",FACE,{"disambiguationData":[TD([[makeQuery(id+"F1.imprint","IMPRINT",EDGE,{"derivedFrom":sQuery(id+"F1.wireOp",EDGE,"E33.1.0.18")}),1.0]])]});
            var Q17;
            Q17=makeQuery(id+"F1.imprint","IMPRINT",FACE,{"disambiguationData":[TD([[makeQuery(id+"F1.imprint","IMPRINT",EDGE,{"derivedFrom":sQuery(id+"F1.wireOp",EDGE,"E33.1.0.16")}),-1.0]])]});
            var Q18;
            Q18=makeQuery(id+"F1.imprint","IMPRINT",FACE,{"disambiguationData":[TD([[makeQuery(id+"F1.imprint","IMPRINT",EDGE,{"derivedFrom":sQuery(id+"F1.wireOp",EDGE,"E19.MirrorC")}),1.0]])]});
            var Q19;
            Q19=makeQuery(id+"F1.imprint","IMPRINT",FACE,{"disambiguationData":[TD([[makeQuery(id+"F1.imprint","IMPRINT",EDGE,{"derivedFrom":sQuery(id+"F1.wireOp",EDGE,"E17")}),-1.0]])]});
            var Q20;
            Q20=makeQuery(id+"F1.imprint","IMPRINT",FACE,{"disambiguationData":[TD([[makeQuery(id+"F1.imprint","IMPRINT",EDGE,{"derivedFrom":sQuery(id+"F1.wireOp",EDGE,"E16")}),-1.0]])]});
            var Q21;
            Q21=makeQuery(id+"F1.imprint","IMPRINT",FACE,{"disambiguationData":[TD([[makeQuery(id+"F1.imprint","IMPRINT",EDGE,{"derivedFrom":sQuery(id+"F1.wireOp",EDGE,"E20.MirrorC")}),1.0]])]});
            var Q22;
            {var subQ0=sQuery(id+"F1.wireOp",EDGE,"E33.1.0.15");Q22=makeQuery(id+"F1.imprint","IMPRINT",FACE,{"disambiguationData":[TD([[makeQuery(id+"F1.imprint","IMPRINT",EDGE,{"derivedFrom":subQ0}),1.0]])]});}
            var Q23;
            {var subQ0=sQuery(id+"F1.wireOp",EDGE,"E33.1.0.11");Q23=makeQuery(id+"F1.imprint","IMPRINT",FACE,{"disambiguationData":[TD([[makeQuery(id+"F1.imprint","IMPRINT",EDGE,{"derivedFrom":subQ0}),-1.0]])]});}
            var Q24;
            {var subQ0=sQuery(id+"F1.wireOp",EDGE,"E33.2.0.15");Q24=makeQuery(id+"F1.imprint","IMPRINT",FACE,{"disambiguationData":[TD([[makeQuery(id+"F1.imprint","IMPRINT",EDGE,{"derivedFrom":subQ0}),1.0]])]});}
            var Q25;
            {var subQ0=sQuery(id+"F1.wireOp",EDGE,"E33.2.0.11");Q25=makeQuery(id+"F1.imprint","IMPRINT",FACE,{"disambiguationData":[TD([[makeQuery(id+"F1.imprint","IMPRINT",EDGE,{"derivedFrom":subQ0}),-1.0]])]});}
            var Q26;
            {var subQ0=sQuery(id+"F1.wireOp",EDGE,"E33.3.0.15");Q26=makeQuery(id+"F1.imprint","IMPRINT",FACE,{"disambiguationData":[TD([[makeQuery(id+"F1.imprint","IMPRINT",EDGE,{"derivedFrom":subQ0}),1.0]])]});}
            var Q27;
            {var subQ0=sQuery(id+"F1.wireOp",EDGE,"E33.3.0.11");Q27=makeQuery(id+"F1.imprint","IMPRINT",FACE,{"disambiguationData":[TD([[makeQuery(id+"F1.imprint","IMPRINT",EDGE,{"derivedFrom":subQ0}),-1.0]])]});}
            var Q28;
            {var subQ0=sQuery(id+"F1.wireOp",EDGE,"E33.4.0.15");Q28=makeQuery(id+"F1.imprint","IMPRINT",FACE,{"disambiguationData":[TD([[makeQuery(id+"F1.imprint","IMPRINT",EDGE,{"derivedFrom":subQ0}),1.0]])]});}
            var Q29;
            {var subQ0=sQuery(id+"F1.wireOp",EDGE,"E33.4.0.11");Q29=makeQuery(id+"F1.imprint","IMPRINT",FACE,{"disambiguationData":[TD([[makeQuery(id+"F1.imprint","IMPRINT",EDGE,{"derivedFrom":subQ0}),-1.0]])]});}
            extrude(context, id + "F3", {"entities" : qUnion([Q0, Q1, Q2, Q3, Q4, Q5, Q6, Q7, Q8, Q9, Q10, Q11, Q12, Q13, Q14, Q15, Q16, Q17, Q18, Q19, Q20, Q21, Q22, Q23, Q24, Q25, Q26, Q27, Q28, Q29]), "operationType" : NewBodyOperationType.ADD, "depth" : 6 * mm, "offsetDistance" : 25 * mm});
        }
        {
            var Q0;
            Q0=makeQuery(id+"F3.opExtrude","CAP_FACE",FACE,{"disambiguationData":[OSD([sQuery(id+"F1.wireOp",EDGE,"E18.MirrorC"),sQuery(id+"F1.wireOp",EDGE,"E24.MirrorCS"),sQuery(id+"F1.wireOp",EDGE,"E26.MirrorCS"),sQuery(id+"F1.wireOp",EDGE,"E33.1.0.1"),sQuery(id+"F1.wireOp",EDGE,"E33.1.0.20"),sQuery(id+"F1.wireOp",EDGE,"E33.1.0.21"),sQuery(id+"F1.wireOp",EDGE,"E35.trimOffspring")])],"isStart":false});
            var sketch = newSketch(context, id + "F4", { "sketchPlane" : qUnion([Q0])});
            skPoint(sketch, "E63.0", {"position": v(0, 50) * mm});
            skPoint(sketch, "E64.0", {"position": v(160.5, 0) * mm});
            skLineSegment(sketch, "E65.bottom", {"start": v(0, 50) * mm, "end": v(160.5, 50) * mm});
            skLineSegment(sketch, "E65.top", {"start": v(0, 0) * mm, "end": v(160.5, 0) * mm});
            skLineSegment(sketch, "E65.left", {"start": v(0, 50) * mm, "end": v(0, 0) * mm});
            skLineSegment(sketch, "E65.right", {"start": v(160.5, 50) * mm, "end": v(160.5, 0) * mm});
            skLineSegment(sketch, "E66", {"start": v(0, 31.8) * mm, "end": v(160.5, 31.8) * mm});
            skLineSegment(sketch, "E67.0", {"start": v(0, 31.8) * mm, "end": v(32.1, 31.8) * mm});
            skSolve(sketch);
        }
        {
            var Q0;
            Q0 = qSketchRegion(id + "F4", true);
            extrude(context, id + "F5", {"entities" : qUnion([Q0]), "depth" : 1.2 * mm, "offsetDistance" : 25 * mm});
        }
        {
            var Q0;
            {var subQ0=sQuery(id+"F4.wireOp",EDGE,"E65.top");Q0=makeQuery(id+"F4.imprint","IMPRINT",FACE,{"disambiguationData":[TD([[makeQuery(id+"F4.imprint","IMPRINT",EDGE,{"derivedFrom":subQ0}),1.0]])]});}
            extrude(context, id + "F6", {"entities" : qUnion([Q0]), "operationType" : NewBodyOperationType.ADD, "depth" : 12.7 * mm, "offsetDistance" : 25 * mm});
        }
        {
            var Q0;
            Q0=makeQuery(id+"F5.opExtrude","CAP_FACE",FACE,{"disambiguationData":[OSD([sQuery(id+"F4.wireOp",EDGE,"E65.bottom"),sQuery(id+"F4.wireOp",EDGE,"E65.top"),sQuery(id+"F4.wireOp",EDGE,"E65.left"),sQuery(id+"F4.wireOp",EDGE,"E65.right")])],"isStart":false});
            var sketch = newSketch(context, id + "F7", { "sketchPlane" : qUnion([Q0])});
            skLineSegment(sketch, "E68.0.0", {"start": v(27.1, 50) * mm, "end": v(27.1, 45) * mm});
            skLineSegment(sketch, "E68.0.1", {"start": v(27.1, 45) * mm, "end": v(37.1, 45) * mm});
            skLineSegment(sketch, "E68.0.2", {"start": v(37.1, 45) * mm, "end": v(37.1, 50) * mm});
            skLineSegment(sketch, "E68.0.3", {"start": v(37.1, 50) * mm, "end": v(27.1, 50) * mm});
            skCircle(sketch, "E69.0", {"center": v(66.7, 47.5) * mm, "radius": 1.25 * mm});
            skLineSegment(sketch, "E70.0.0", {"start": v(59.2, 50) * mm, "end": v(59.2, 45) * mm});
            skLineSegment(sketch, "E70.0.1", {"start": v(59.2, 45) * mm, "end": v(69.2, 45) * mm});
            skLineSegment(sketch, "E70.0.2", {"start": v(69.2, 45) * mm, "end": v(69.2, 50) * mm});
            skLineSegment(sketch, "E70.0.3", {"start": v(69.2, 50) * mm, "end": v(59.2, 50) * mm});
            skLineSegment(sketch, "E71.0.0", {"start": v(101.3, 50) * mm, "end": v(91.3, 50) * mm});
            skLineSegment(sketch, "E71.0.1", {"start": v(91.3, 50) * mm, "end": v(91.3, 45) * mm});
            skLineSegment(sketch, "E71.0.2", {"start": v(91.3, 45) * mm, "end": v(101.3, 45) * mm});
            skLineSegment(sketch, "E71.0.3", {"start": v(101.3, 45) * mm, "end": v(101.3, 50) * mm});
            skLineSegment(sketch, "E72.0.0", {"start": v(123.4, 50) * mm, "end": v(123.4, 45) * mm});
            skLineSegment(sketch, "E72.0.1", {"start": v(123.4, 45) * mm, "end": v(133.4, 45) * mm});
            skLineSegment(sketch, "E72.0.2", {"start": v(133.4, 45) * mm, "end": v(133.4, 50) * mm});
            skLineSegment(sketch, "E72.0.3", {"start": v(133.4, 50) * mm, "end": v(123.4, 50) * mm});
            skLineSegment(sketch, "E73.0.0", {"start": v(155.5, 50) * mm, "end": v(155.5, 45) * mm});
            skLineSegment(sketch, "E73.0.1", {"start": v(155.5, 45) * mm, "end": v(160.5, 45) * mm});
            skLineSegment(sketch, "E73.0.2", {"start": v(160.5, 45) * mm, "end": v(160.5, 50) * mm});
            skLineSegment(sketch, "E73.0.3", {"start": v(160.5, 50) * mm, "end": v(155.5, 50) * mm});
            skCircle(sketch, "E74.0", {"center": v(61.7, 47.5) * mm, "radius": 1.25 * mm});
            skCircle(sketch, "E75.0", {"center": v(34.6, 47.5) * mm, "radius": 1.25 * mm});
            skCircle(sketch, "E76.0", {"center": v(29.6, 47.5) * mm, "radius": 1.25 * mm});
            skCircle(sketch, "E77.0", {"center": v(2.5, 47.5) * mm, "radius": 1.25 * mm});
            skLineSegment(sketch, "E78.0.0", {"start": v(0, 50) * mm, "end": v(0, 45) * mm});
            skLineSegment(sketch, "E78.0.1", {"start": v(0, 45) * mm, "end": v(5, 45) * mm});
            skLineSegment(sketch, "E78.0.2", {"start": v(5, 45) * mm, "end": v(5, 50) * mm});
            skLineSegment(sketch, "E78.0.3", {"start": v(5, 50) * mm, "end": v(0, 50) * mm});
            skCircle(sketch, "E79.0", {"center": v(93.8, 47.5) * mm, "radius": 1.25 * mm});
            skCircle(sketch, "E80.0", {"center": v(98.8, 47.5) * mm, "radius": 1.25 * mm});
            skCircle(sketch, "E81.0", {"center": v(125.9, 47.5) * mm, "radius": 1.25 * mm});
            skCircle(sketch, "E82.0", {"center": v(130.9, 47.5) * mm, "radius": 1.25 * mm});
            skCircle(sketch, "E83.0", {"center": v(158, 47.5) * mm, "radius": 1.25 * mm});
            skLineSegment(sketch, "E84.0.0", {"start": v(5, -13.2) * mm, "end": v(0, -13.2) * mm});
            skLineSegment(sketch, "E84.0.1", {"start": v(0, -13.2) * mm, "end": v(0, -18.2) * mm});
            skLineSegment(sketch, "E84.0.2", {"start": v(0, -18.2) * mm, "end": v(5, -18.2) * mm});
            skLineSegment(sketch, "E84.0.3", {"start": v(5, -18.2) * mm, "end": v(5, -13.2) * mm});
            skCircle(sketch, "E85.0", {"center": v(2.5, -15.7) * mm, "radius": 1.25 * mm});
            skLineSegment(sketch, "E86.0.0", {"start": v(37.1, -13.2) * mm, "end": v(27.1, -13.2) * mm});
            skLineSegment(sketch, "E86.0.1", {"start": v(27.1, -13.2) * mm, "end": v(27.1, -18.2) * mm});
            skLineSegment(sketch, "E86.0.2", {"start": v(27.1, -18.2) * mm, "end": v(37.1, -18.2) * mm});
            skLineSegment(sketch, "E86.0.3", {"start": v(37.1, -18.2) * mm, "end": v(37.1, -13.2) * mm});
            skCircle(sketch, "E87.0", {"center": v(29.6, -15.7) * mm, "radius": 1.25 * mm});
            skCircle(sketch, "E88.0", {"center": v(34.6, -15.7) * mm, "radius": 1.25 * mm});
            skCircle(sketch, "E89.0", {"center": v(61.7, -15.7) * mm, "radius": 1.25 * mm});
            skCircle(sketch, "E90.0", {"center": v(66.7, -15.7) * mm, "radius": 1.25 * mm});
            skLineSegment(sketch, "E91.0.0", {"start": v(59.2, -18.2) * mm, "end": v(69.2, -18.2) * mm});
            skLineSegment(sketch, "E91.0.1", {"start": v(69.2, -18.2) * mm, "end": v(69.2, -13.2) * mm});
            skLineSegment(sketch, "E91.0.2", {"start": v(69.2, -13.2) * mm, "end": v(59.2, -13.2) * mm});
            skLineSegment(sketch, "E91.0.3", {"start": v(59.2, -13.2) * mm, "end": v(59.2, -18.2) * mm});
            skCircle(sketch, "E92.0", {"center": v(93.8, -15.7) * mm, "radius": 1.25 * mm});
            skCircle(sketch, "E93.0", {"center": v(98.8, -15.7) * mm, "radius": 1.25 * mm});
            skLineSegment(sketch, "E94.0.0", {"start": v(91.3, -18.2) * mm, "end": v(101.3, -18.2) * mm});
            skLineSegment(sketch, "E94.0.1", {"start": v(101.3, -18.2) * mm, "end": v(101.3, -13.2) * mm});
            skLineSegment(sketch, "E94.0.2", {"start": v(101.3, -13.2) * mm, "end": v(91.3, -13.2) * mm});
            skLineSegment(sketch, "E94.0.3", {"start": v(91.3, -13.2) * mm, "end": v(91.3, -18.2) * mm});
            skCircle(sketch, "E95.0", {"center": v(125.9, -15.7) * mm, "radius": 1.25 * mm});
            skCircle(sketch, "E96.0", {"center": v(130.9, -15.7) * mm, "radius": 1.25 * mm});
            skCircle(sketch, "E97.0", {"center": v(158, -15.7) * mm, "radius": 1.25 * mm});
            skPoint(sketch, "E98.0", {"position": v(155.5, -13.2) * mm});
            skLineSegment(sketch, "E99.0.0", {"start": v(160.5, -13.2) * mm, "end": v(155.5, -13.2) * mm});
            skLineSegment(sketch, "E99.0.1", {"start": v(155.5, -13.2) * mm, "end": v(155.5, -18.2) * mm});
            skLineSegment(sketch, "E99.0.2", {"start": v(155.5, -18.2) * mm, "end": v(160.5, -18.2) * mm});
            skLineSegment(sketch, "E99.0.3", {"start": v(160.5, -18.2) * mm, "end": v(160.5, -13.2) * mm});
            skLineSegment(sketch, "E100.0.0", {"start": v(123.4, -18.2) * mm, "end": v(133.4, -18.2) * mm});
            skLineSegment(sketch, "E100.0.1", {"start": v(133.4, -18.2) * mm, "end": v(133.4, -13.2) * mm});
            skLineSegment(sketch, "E100.0.2", {"start": v(133.4, -13.2) * mm, "end": v(123.4, -13.2) * mm});
            skLineSegment(sketch, "E100.0.3", {"start": v(123.4, -13.2) * mm, "end": v(123.4, -18.2) * mm});
            skLineSegment(sketch, "E101.0.0", {"start": v(160.5, 0) * mm, "end": v(160.5, 31.8) * mm, "construction": true});
            skLineSegment(sketch, "E101.0.1", {"start": v(160.5, 31.8) * mm, "end": v(0, 31.8) * mm, "construction": true});
            skLineSegment(sketch, "E101.0.2", {"start": v(0, 31.8) * mm, "end": v(0, 0) * mm, "construction": true});
            skLineSegment(sketch, "E101.0.3", {"start": v(0, 0) * mm, "end": v(160.5, 0) * mm, "construction": true});
            skLineSegment(sketch, "E102.0", {"start": v(160.8, -0.3) * mm, "end": v(160.8, 32.1) * mm});
            skLineSegment(sketch, "E102.1", {"start": v(-0.3, -0.3) * mm, "end": v(160.8, -0.3) * mm});
            skLineSegment(sketch, "E102.2", {"start": v(-0.3, 32.1) * mm, "end": v(-0.3, -0.3) * mm});
            skLineSegment(sketch, "E102.3", {"start": v(160.8, 32.1) * mm, "end": v(-0.3, 32.1) * mm});
            skLineSegment(sketch, "E103.left", {"start": v(-5, 50) * mm, "end": v(-5, -18.2) * mm});
            skLineSegment(sketch, "E103.right", {"start": v(165.5, 50) * mm, "end": v(165.5, -18.2) * mm});
            skLineSegment(sketch, "E104", {"start": v(0, 50) * mm, "end": v(5, 50) * mm});
            skLineSegment(sketch, "E105", {"start": v(-5, -18.2) * mm, "end": v(165.5, -18.2) * mm});
            skLineSegment(sketch, "E106.trimOffspring", {"start": v(59.2, 50) * mm, "end": v(101.3, 50) * mm});
            skLineSegment(sketch, "E107.trimOffspring", {"start": v(123.4, 50) * mm, "end": v(133.4, 50) * mm});
            skLineSegment(sketch, "E108.trimOffspring", {"start": v(155.5, 50) * mm, "end": v(160.5, 50) * mm});
            skLineSegment(sketch, "E109", {"start": v(-5, 50) * mm, "end": v(165.5, 50) * mm});
            skSolve(sketch);
        }
        {
            var Q0;
            {var subQ0=sQuery(id+"F7.wireOp",EDGE,"E68.0.3");Q0=makeQuery(id+"F7.imprint","IMPRINT",FACE,{"disambiguationData":[TD([[makeQuery(id+"F7.imprint","IMPRINT",EDGE,{"derivedFrom":subQ0}),1.0]])]});}
            var Q1;
            {var subQ20=sQuery(id+"F7.wireOp",EDGE,"E68.0.0");Q1=makeQuery(id+"F7.imprint","IMPRINT",FACE,{"disambiguationData":[TD([[makeQuery(id+"F7.imprint","IMPRINT",EDGE,{"derivedFrom":subQ20}),-1.0]])]});}
            var Q2;
            {var subQ13=sQuery(id+"F7.wireOp",EDGE,"E73.0.2");Q2=makeQuery(id+"F7.imprint","IMPRINT",FACE,{"disambiguationData":[TD([[makeQuery(id+"F7.imprint","IMPRINT",EDGE,{"derivedFrom":subQ13}),1.0]])]});}
            var Q3;
            Q3=makeQuery(id+"F6.opExtrude","CAP_FACE",FACE,{"disambiguationData":[OSD([sQuery(id+"F4.wireOp",EDGE,"E65.top"),sQuery(id+"F4.wireOp",EDGE,"E65.left"),sQuery(id+"F4.wireOp",EDGE,"E65.right"),sQuery(id+"F4.wireOp",EDGE,"E66")])],"isStart":false});
            extrude(context, id + "F8", {"entities" : qUnion([Q0, Q1, Q2]), "endBound" : BoundingType.UP_TO_SURFACE, "depth" : -3 * mm, "endBoundEntityFace" : qUnion([Q3]), "offsetDistance" : 25 * mm, "hasSecondDirection" : true, "secondDirectionOppositeDirection" : false, "secondDirectionDepth" : 7.7 * mm});
        }
        {
            var Q0;
            Q0=makeQuery(id+"F3.opExtrude","CAP_FACE",FACE,{"disambiguationData":[OSD([sQuery(id+"F1.wireOp",EDGE,"E16"),sQuery(id+"F1.wireOp",EDGE,"E23.top"),sQuery(id+"F1.wireOp",EDGE,"E23.left"),sQuery(id+"F1.wireOp",EDGE,"E31.trimOffspring"),sQuery(id+"F1.wireOp",EDGE,"E40.MirrorCS")])],"isStart":false});
            var Q1;
            Q1=makeQuery(id+"F3.opExtrude","CAP_FACE",FACE,{"disambiguationData":[OSD([sQuery(id+"F1.wireOp",EDGE,"E33.1.0.9"),sQuery(id+"F1.wireOp",EDGE,"E33.1.0.11"),sQuery(id+"F1.wireOp",EDGE,"E33.1.0.19"),sQuery(id+"F1.wireOp",EDGE,"E33.2.0.8"),sQuery(id+"F1.wireOp",EDGE,"E33.2.0.15"),sQuery(id+"F1.wireOp",EDGE,"E33.2.0.22"),sQuery(id+"F1.wireOp",EDGE,"E42.MirrorCS")])],"isStart":false});
            var Q2;
            Q2=makeQuery(id+"F3.opExtrude","CAP_FACE",FACE,{"disambiguationData":[OSD([sQuery(id+"F1.wireOp",EDGE,"E33.2.0.9"),sQuery(id+"F1.wireOp",EDGE,"E33.2.0.11"),sQuery(id+"F1.wireOp",EDGE,"E33.2.0.19"),sQuery(id+"F1.wireOp",EDGE,"E33.3.0.8"),sQuery(id+"F1.wireOp",EDGE,"E33.3.0.15"),sQuery(id+"F1.wireOp",EDGE,"E33.3.0.22"),sQuery(id+"F1.wireOp",EDGE,"E43.MirrorCS")])],"isStart":false});
            var Q3;
            Q3=makeQuery(id+"F3.opExtrude","CAP_FACE",FACE,{"disambiguationData":[OSD([sQuery(id+"F1.wireOp",EDGE,"E33.3.0.9"),sQuery(id+"F1.wireOp",EDGE,"E33.3.0.11"),sQuery(id+"F1.wireOp",EDGE,"E33.3.0.19"),sQuery(id+"F1.wireOp",EDGE,"E33.4.0.8"),sQuery(id+"F1.wireOp",EDGE,"E33.4.0.15"),sQuery(id+"F1.wireOp",EDGE,"E33.4.0.22"),sQuery(id+"F1.wireOp",EDGE,"E44.MirrorCS")])],"isStart":false});
            var Q4;
            Q4=makeQuery(id+"F3.opExtrude","CAP_FACE",FACE,{"disambiguationData":[OSD([sQuery(id+"F1.wireOp",EDGE,"E33.4.0.4"),sQuery(id+"F1.wireOp",EDGE,"E33.4.0.9"),sQuery(id+"F1.wireOp",EDGE,"E33.4.0.11"),sQuery(id+"F1.wireOp",EDGE,"E33.4.0.19"),sQuery(id+"F1.wireOp",EDGE,"E45.MirrorCS")])],"isStart":false});
            var Q5;
            Q5=makeQuery(id+"F3.opExtrude","CAP_FACE",FACE,{"disambiguationData":[OSD([sQuery(id+"F1.wireOp",EDGE,"E20.MirrorC"),sQuery(id+"F1.wireOp",EDGE,"E27.MirrorCS"),sQuery(id+"F1.wireOp",EDGE,"E32.trimOffspring"),sQuery(id+"F1.wireOp",EDGE,"E33.1.0.8"),sQuery(id+"F1.wireOp",EDGE,"E33.1.0.15"),sQuery(id+"F1.wireOp",EDGE,"E33.1.0.22"),sQuery(id+"F1.wireOp",EDGE,"E41.MirrorCS")])],"isStart":false});
            var Q6;
            Q6=makeQuery(id+"F8.opExtrude","CAP_FACE",FACE,{"disambiguationData":[OSD([sQuery(id+"F7.wireOp",EDGE,"E68.0.0"),sQuery(id+"F7.wireOp",EDGE,"E68.0.1"),sQuery(id+"F7.wireOp",EDGE,"E68.0.2"),sQuery(id+"F7.wireOp",EDGE,"E70.0.0"),sQuery(id+"F7.wireOp",EDGE,"E70.0.1"),sQuery(id+"F7.wireOp",EDGE,"E70.0.2"),sQuery(id+"F7.wireOp",EDGE,"E71.0.1"),sQuery(id+"F7.wireOp",EDGE,"E71.0.2"),sQuery(id+"F7.wireOp",EDGE,"E71.0.3"),sQuery(id+"F7.wireOp",EDGE,"E72.0.0"),sQuery(id+"F7.wireOp",EDGE,"E72.0.1"),sQuery(id+"F7.wireOp",EDGE,"E72.0.2"),sQuery(id+"F7.wireOp",EDGE,"E73.0.0"),sQuery(id+"F7.wireOp",EDGE,"E73.0.1"),sQuery(id+"F7.wireOp",EDGE,"E73.0.2"),sQuery(id+"F7.wireOp",EDGE,"E78.0.0"),sQuery(id+"F7.wireOp",EDGE,"E78.0.1"),sQuery(id+"F7.wireOp",EDGE,"E78.0.2"),sQuery(id+"F7.wireOp",EDGE,"E84.0.0"),sQuery(id+"F7.wireOp",EDGE,"E84.0.1"),sQuery(id+"F7.wireOp",EDGE,"E84.0.3"),sQuery(id+"F7.wireOp",EDGE,"E86.0.0"),sQuery(id+"F7.wireOp",EDGE,"E86.0.1"),sQuery(id+"F7.wireOp",EDGE,"E86.0.3"),sQuery(id+"F7.wireOp",EDGE,"E91.0.1"),sQuery(id+"F7.wireOp",EDGE,"E91.0.2"),sQuery(id+"F7.wireOp",EDGE,"E91.0.3"),sQuery(id+"F7.wireOp",EDGE,"E94.0.1"),sQuery(id+"F7.wireOp",EDGE,"E94.0.2"),sQuery(id+"F7.wireOp",EDGE,"E94.0.3"),sQuery(id+"F7.wireOp",EDGE,"E99.0.0"),sQuery(id+"F7.wireOp",EDGE,"E99.0.1"),sQuery(id+"F7.wireOp",EDGE,"E99.0.3"),sQuery(id+"F7.wireOp",EDGE,"E100.0.1"),sQuery(id+"F7.wireOp",EDGE,"E100.0.2"),sQuery(id+"F7.wireOp",EDGE,"E100.0.3"),sQuery(id+"F7.wireOp",EDGE,"E102.0"),sQuery(id+"F7.wireOp",EDGE,"E102.1"),sQuery(id+"F7.wireOp",EDGE,"E102.2"),sQuery(id+"F7.wireOp",EDGE,"E102.3"),sQuery(id+"F7.wireOp",EDGE,"E103.left"),sQuery(id+"F7.wireOp",EDGE,"E103.right"),sQuery(id+"F7.wireOp",EDGE,"E105"),sQuery(id+"F7.wireOp",EDGE,"E109")])],"isStart":false});
            extrude(context, id + "F9", {"entities" : qUnion([Q0, Q1, Q2, Q3, Q4, Q5]), "operationType" : NewBodyOperationType.ADD, "endBound" : BoundingType.UP_TO_SURFACE, "depth" : 25 * mm, "endBoundEntityFace" : qUnion([Q6]), "offsetDistance" : 25 * mm});
        }
        {
            var Q0;
            {var subQ1=sQuery(id+"F7.wireOp",EDGE,"E73.0.0");Q0=makeQuery(id+"F7.imprint","IMPRINT",FACE,{"disambiguationData":[TD([[makeQuery(id+"F7.imprint","IMPRINT",EDGE,{"derivedFrom":subQ1}),1.0]])]});}
            var Q1;
            {var subQ1=sQuery(id+"F7.wireOp",EDGE,"E72.0.0");Q1=makeQuery(id+"F7.imprint","IMPRINT",FACE,{"disambiguationData":[TD([[makeQuery(id+"F7.imprint","IMPRINT",EDGE,{"derivedFrom":subQ1}),1.0]])]});}
            var Q2;
            {var subQ1=sQuery(id+"F7.wireOp",EDGE,"E71.0.1");Q2=makeQuery(id+"F7.imprint","IMPRINT",FACE,{"disambiguationData":[TD([[makeQuery(id+"F7.imprint","IMPRINT",EDGE,{"derivedFrom":subQ1}),1.0]])]});}
            var Q3;
            Q3=makeQuery(id+"F7.imprint","IMPRINT",FACE,{"disambiguationData":[TD([[makeQuery(id+"F7.imprint","IMPRINT",EDGE,{"derivedFrom":sQuery(id+"F7.wireOp",EDGE,"E69.0")}),-1.0]])]});
            var Q4;
            {var subQ1=sQuery(id+"F7.wireOp",EDGE,"E68.0.0");Q4=makeQuery(id+"F7.imprint","IMPRINT",FACE,{"disambiguationData":[TD([[makeQuery(id+"F7.imprint","IMPRINT",EDGE,{"derivedFrom":subQ1}),1.0]])]});}
            var Q5;
            Q5=makeQuery(id+"F7.imprint","IMPRINT",FACE,{"disambiguationData":[TD([[makeQuery(id+"F7.imprint","IMPRINT",EDGE,{"derivedFrom":sQuery(id+"F7.wireOp",EDGE,"E77.0")}),-1.0]])]});
            var Q6;
            Q6=makeQuery(id+"F9.boolean.opBoolean","MERGE",FACE,{"derivedFrom":[makeQuery(id+"F8.opExtrude","CAP_FACE",FACE,{"disambiguationData":[OSD([sQuery(id+"F7.wireOp",EDGE,"E68.0.0"),sQuery(id+"F7.wireOp",EDGE,"E68.0.1"),sQuery(id+"F7.wireOp",EDGE,"E68.0.2"),sQuery(id+"F7.wireOp",EDGE,"E70.0.0"),sQuery(id+"F7.wireOp",EDGE,"E70.0.1"),sQuery(id+"F7.wireOp",EDGE,"E70.0.2"),sQuery(id+"F7.wireOp",EDGE,"E71.0.1"),sQuery(id+"F7.wireOp",EDGE,"E71.0.2"),sQuery(id+"F7.wireOp",EDGE,"E71.0.3"),sQuery(id+"F7.wireOp",EDGE,"E72.0.0"),sQuery(id+"F7.wireOp",EDGE,"E72.0.1"),sQuery(id+"F7.wireOp",EDGE,"E72.0.2"),sQuery(id+"F7.wireOp",EDGE,"E73.0.0"),sQuery(id+"F7.wireOp",EDGE,"E73.0.1"),sQuery(id+"F7.wireOp",EDGE,"E73.0.2"),sQuery(id+"F7.wireOp",EDGE,"E78.0.0"),sQuery(id+"F7.wireOp",EDGE,"E78.0.1"),sQuery(id+"F7.wireOp",EDGE,"E78.0.2"),sQuery(id+"F7.wireOp",EDGE,"E84.0.0"),sQuery(id+"F7.wireOp",EDGE,"E84.0.1"),sQuery(id+"F7.wireOp",EDGE,"E84.0.3"),sQuery(id+"F7.wireOp",EDGE,"E86.0.0"),sQuery(id+"F7.wireOp",EDGE,"E86.0.1"),sQuery(id+"F7.wireOp",EDGE,"E86.0.3"),sQuery(id+"F7.wireOp",EDGE,"E91.0.1"),sQuery(id+"F7.wireOp",EDGE,"E91.0.2"),sQuery(id+"F7.wireOp",EDGE,"E91.0.3"),sQuery(id+"F7.wireOp",EDGE,"E94.0.1"),sQuery(id+"F7.wireOp",EDGE,"E94.0.2"),sQuery(id+"F7.wireOp",EDGE,"E94.0.3"),sQuery(id+"F7.wireOp",EDGE,"E99.0.0"),sQuery(id+"F7.wireOp",EDGE,"E99.0.1"),sQuery(id+"F7.wireOp",EDGE,"E99.0.3"),sQuery(id+"F7.wireOp",EDGE,"E100.0.1"),sQuery(id+"F7.wireOp",EDGE,"E100.0.2"),sQuery(id+"F7.wireOp",EDGE,"E100.0.3"),sQuery(id+"F7.wireOp",EDGE,"E102.0"),sQuery(id+"F7.wireOp",EDGE,"E102.1"),sQuery(id+"F7.wireOp",EDGE,"E102.2"),sQuery(id+"F7.wireOp",EDGE,"E102.3"),sQuery(id+"F7.wireOp",EDGE,"E103.left"),sQuery(id+"F7.wireOp",EDGE,"E103.right"),sQuery(id+"F7.wireOp",EDGE,"E105"),sQuery(id+"F7.wireOp",EDGE,"E109")])],"isStart":false}),makeQuery(id+"F9.opExtrude","CAP_FACE",FACE,{"disambiguationData":[OSD([sQuery(id+"F1.wireOp",EDGE,"E16"),sQuery(id+"F1.wireOp",EDGE,"E23.top"),sQuery(id+"F1.wireOp",EDGE,"E23.left"),sQuery(id+"F1.wireOp",EDGE,"E31.trimOffspring"),sQuery(id+"F1.wireOp",EDGE,"E40.MirrorCS")])],"isStart":false}),makeQuery(id+"F9.opExtrude","CAP_FACE",FACE,{"disambiguationData":[OSD([sQuery(id+"F1.wireOp",EDGE,"E20.MirrorC"),sQuery(id+"F1.wireOp",EDGE,"E27.MirrorCS"),sQuery(id+"F1.wireOp",EDGE,"E32.trimOffspring"),sQuery(id+"F1.wireOp",EDGE,"E33.1.0.8"),sQuery(id+"F1.wireOp",EDGE,"E33.1.0.15"),sQuery(id+"F1.wireOp",EDGE,"E33.1.0.22"),sQuery(id+"F1.wireOp",EDGE,"E41.MirrorCS")])],"isStart":false}),makeQuery(id+"F9.opExtrude","CAP_FACE",FACE,{"disambiguationData":[OSD([sQuery(id+"F1.wireOp",EDGE,"E33.1.0.9"),sQuery(id+"F1.wireOp",EDGE,"E33.1.0.11"),sQuery(id+"F1.wireOp",EDGE,"E33.1.0.19"),sQuery(id+"F1.wireOp",EDGE,"E33.2.0.8"),sQuery(id+"F1.wireOp",EDGE,"E33.2.0.15"),sQuery(id+"F1.wireOp",EDGE,"E33.2.0.22"),sQuery(id+"F1.wireOp",EDGE,"E42.MirrorCS")])],"isStart":false}),makeQuery(id+"F9.opExtrude","CAP_FACE",FACE,{"disambiguationData":[OSD([sQuery(id+"F1.wireOp",EDGE,"E33.2.0.9"),sQuery(id+"F1.wireOp",EDGE,"E33.2.0.11"),sQuery(id+"F1.wireOp",EDGE,"E33.2.0.19"),sQuery(id+"F1.wireOp",EDGE,"E33.3.0.8"),sQuery(id+"F1.wireOp",EDGE,"E33.3.0.15"),sQuery(id+"F1.wireOp",EDGE,"E33.3.0.22"),sQuery(id+"F1.wireOp",EDGE,"E43.MirrorCS")])],"isStart":false}),makeQuery(id+"F9.opExtrude","CAP_FACE",FACE,{"disambiguationData":[OSD([sQuery(id+"F1.wireOp",EDGE,"E33.3.0.9"),sQuery(id+"F1.wireOp",EDGE,"E33.3.0.11"),sQuery(id+"F1.wireOp",EDGE,"E33.3.0.19"),sQuery(id+"F1.wireOp",EDGE,"E33.4.0.8"),sQuery(id+"F1.wireOp",EDGE,"E33.4.0.15"),sQuery(id+"F1.wireOp",EDGE,"E33.4.0.22"),sQuery(id+"F1.wireOp",EDGE,"E44.MirrorCS")])],"isStart":false}),makeQuery(id+"F9.opExtrude","CAP_FACE",FACE,{"disambiguationData":[OSD([sQuery(id+"F1.wireOp",EDGE,"E33.4.0.4"),sQuery(id+"F1.wireOp",EDGE,"E33.4.0.9"),sQuery(id+"F1.wireOp",EDGE,"E33.4.0.11"),sQuery(id+"F1.wireOp",EDGE,"E33.4.0.19"),sQuery(id+"F1.wireOp",EDGE,"E45.MirrorCS")])],"isStart":false})]});
            extrude(context, id + "F10", {"entities" : qUnion([Q0, Q1, Q2, Q3, Q4, Q5]), "operationType" : NewBodyOperationType.ADD, "endBound" : BoundingType.UP_TO_SURFACE, "depth" : 25 * mm, "endBoundEntityFace" : qUnion([Q6]), "offsetDistance" : 25 * mm});
        }
        {
            var Q0;
            Q0=makeQuery(id+"F8.opExtrude","CAP_FACE",FACE,{"disambiguationData":[OSD([sQuery(id+"F7.wireOp",EDGE,"E68.0.0"),sQuery(id+"F7.wireOp",EDGE,"E68.0.1"),sQuery(id+"F7.wireOp",EDGE,"E68.0.2"),sQuery(id+"F7.wireOp",EDGE,"E70.0.0"),sQuery(id+"F7.wireOp",EDGE,"E70.0.1"),sQuery(id+"F7.wireOp",EDGE,"E70.0.2"),sQuery(id+"F7.wireOp",EDGE,"E71.0.1"),sQuery(id+"F7.wireOp",EDGE,"E71.0.2"),sQuery(id+"F7.wireOp",EDGE,"E71.0.3"),sQuery(id+"F7.wireOp",EDGE,"E72.0.0"),sQuery(id+"F7.wireOp",EDGE,"E72.0.1"),sQuery(id+"F7.wireOp",EDGE,"E72.0.2"),sQuery(id+"F7.wireOp",EDGE,"E73.0.0"),sQuery(id+"F7.wireOp",EDGE,"E73.0.1"),sQuery(id+"F7.wireOp",EDGE,"E73.0.2"),sQuery(id+"F7.wireOp",EDGE,"E78.0.0"),sQuery(id+"F7.wireOp",EDGE,"E78.0.1"),sQuery(id+"F7.wireOp",EDGE,"E78.0.2"),sQuery(id+"F7.wireOp",EDGE,"E84.0.0"),sQuery(id+"F7.wireOp",EDGE,"E84.0.1"),sQuery(id+"F7.wireOp",EDGE,"E84.0.3"),sQuery(id+"F7.wireOp",EDGE,"E86.0.0"),sQuery(id+"F7.wireOp",EDGE,"E86.0.1"),sQuery(id+"F7.wireOp",EDGE,"E86.0.3"),sQuery(id+"F7.wireOp",EDGE,"E91.0.1"),sQuery(id+"F7.wireOp",EDGE,"E91.0.2"),sQuery(id+"F7.wireOp",EDGE,"E91.0.3"),sQuery(id+"F7.wireOp",EDGE,"E94.0.1"),sQuery(id+"F7.wireOp",EDGE,"E94.0.2"),sQuery(id+"F7.wireOp",EDGE,"E94.0.3"),sQuery(id+"F7.wireOp",EDGE,"E99.0.0"),sQuery(id+"F7.wireOp",EDGE,"E99.0.1"),sQuery(id+"F7.wireOp",EDGE,"E99.0.3"),sQuery(id+"F7.wireOp",EDGE,"E100.0.1"),sQuery(id+"F7.wireOp",EDGE,"E100.0.2"),sQuery(id+"F7.wireOp",EDGE,"E100.0.3"),sQuery(id+"F7.wireOp",EDGE,"E102.0"),sQuery(id+"F7.wireOp",EDGE,"E102.1"),sQuery(id+"F7.wireOp",EDGE,"E102.2"),sQuery(id+"F7.wireOp",EDGE,"E102.3"),sQuery(id+"F7.wireOp",EDGE,"E103.left"),sQuery(id+"F7.wireOp",EDGE,"E103.right"),sQuery(id+"F7.wireOp",EDGE,"E105"),sQuery(id+"F7.wireOp",EDGE,"E109")])],"isStart":true});
            var sketch = newSketch(context, id + "F11", { "sketchPlane" : qUnion([Q0])});
            skCircle(sketch, "E110", {"center": v(144.45, -47.5) * mm, "radius": 1.25 * mm});
            skLineSegment(sketch, "E111", {"start": v(178.71, -15.9) * mm, "end": v(-18.62, -15.9) * mm, "construction": true});
            skPoint(sketch, "E111.startSnap0", {"position": v(160.8, -15.9) * mm});
            skLineSegment(sketch, "E112", {"start": v(80.25, 22.96) * mm, "end": v(80.25, -62.15) * mm, "construction": true});
            skPoint(sketch, "E112.startSnap0", {"position": v(80.25, 18.2) * mm});
            skCircle(sketch, "E113", {"center": v(80.25, -47.5) * mm, "radius": 1.25 * mm});
            skCircle(sketch, "E114.MirrorC", {"center": v(16.05, -47.5) * mm, "radius": 1.25 * mm});
            skCircle(sketch, "E115.MirrorC", {"center": v(144.45, 15.7) * mm, "radius": 1.25 * mm});
            skCircle(sketch, "E116.MirrorC", {"center": v(80.25, 15.7) * mm, "radius": 1.25 * mm});
            skCircle(sketch, "E117.MirrorC", {"center": v(16.05, 15.7) * mm, "radius": 1.25 * mm});
            skPoint(sketch, "E118", {"position": v(133.4, -47.5) * mm});
            skPoint(sketch, "E119", {"position": v(144.45, -50) * mm});
            skSolve(sketch);
        }
        {
            var Q0;
            Q0 = qSketchRegion(id + "F11", true);
            extrude(context, id + "F12", {"entities" : qUnion([Q0]), "operationType" : NewBodyOperationType.REMOVE, "endBound" : BoundingType.THROUGH_ALL, "oppositeDirection" : true, "depth" : 25 * mm, "offsetDistance" : 25 * mm});
        }
        {
            var Q0;
            Q0=makeQuery(id+"F2.opExtrude","SWEPT_EDGE",EDGE,{"disambiguationData":[OSD([sQuery(id+"F1.wireOp",EDGE,"E33.1.0.8"),sQuery(id+"F1.wireOp",EDGE,"E33.1.0.10")])]});
            var Q1;
            Q1=makeQuery(id+"F2.opExtrude","SWEPT_EDGE",EDGE,{"disambiguationData":[OSD([sQuery(id+"F1.wireOp",EDGE,"E30.MirrorCS"),sQuery(id+"F1.wireOp",EDGE,"E31.trimOffspring")])]});
            var Q2;
            Q2=makeQuery(id+"F2.opExtrude","SWEPT_EDGE",EDGE,{"disambiguationData":[OSD([sQuery(id+"F1.wireOp",EDGE,"E33.2.0.8"),sQuery(id+"F1.wireOp",EDGE,"E33.2.0.10")])]});
            var Q3;
            Q3=makeQuery(id+"F2.opExtrude","SWEPT_EDGE",EDGE,{"disambiguationData":[OSD([sQuery(id+"F1.wireOp",EDGE,"E33.3.0.8"),sQuery(id+"F1.wireOp",EDGE,"E33.3.0.10")])]});
            var Q4;
            Q4=makeQuery(id+"F2.opExtrude","SWEPT_EDGE",EDGE,{"disambiguationData":[OSD([sQuery(id+"F1.wireOp",EDGE,"E33.4.0.8"),sQuery(id+"F1.wireOp",EDGE,"E33.4.0.10")])]});
            var Q5;
            Q5=makeQuery(id+"F2.opExtrude","SWEPT_EDGE",EDGE,{"disambiguationData":[OSD([sQuery(id+"F1.wireOp",EDGE,"E30.MirrorCS"),sQuery(id+"F1.wireOp",EDGE,"E32.trimOffspring")])]});
            var Q6;
            Q6=makeQuery(id+"F2.opExtrude","SWEPT_EDGE",EDGE,{"disambiguationData":[OSD([sQuery(id+"F1.wireOp",EDGE,"E33.1.0.9"),sQuery(id+"F1.wireOp",EDGE,"E33.1.0.10")])]});
            var Q7;
            Q7=makeQuery(id+"F2.opExtrude","SWEPT_EDGE",EDGE,{"disambiguationData":[OSD([sQuery(id+"F1.wireOp",EDGE,"E33.2.0.9"),sQuery(id+"F1.wireOp",EDGE,"E33.2.0.10")])]});
            var Q8;
            Q8=makeQuery(id+"F2.opExtrude","SWEPT_EDGE",EDGE,{"disambiguationData":[OSD([sQuery(id+"F1.wireOp",EDGE,"E33.3.0.9"),sQuery(id+"F1.wireOp",EDGE,"E33.3.0.10")])]});
            var Q9;
            Q9=makeQuery(id+"F2.opExtrude","SWEPT_EDGE",EDGE,{"disambiguationData":[OSD([sQuery(id+"F1.wireOp",EDGE,"E33.4.0.9"),sQuery(id+"F1.wireOp",EDGE,"E33.4.0.10")])]});
            var Q10;
            Q10=makeQuery(id+"F2.opExtrude","SWEPT_EDGE",EDGE,{"disambiguationData":[OSD([sQuery(id+"F1.wireOp",EDGE,"E23.right"),sQuery(id+"F1.wireOp",EDGE,"E28")])]});
            var Q11;
            Q11=makeQuery(id+"F2.opExtrude","SWEPT_EDGE",EDGE,{"disambiguationData":[OSD([sQuery(id+"F1.wireOp",EDGE,"E24.MirrorCS"),sQuery(id+"F1.wireOp",EDGE,"E28")])]});
            var Q12;
            Q12=makeQuery(id+"F2.opExtrude","SWEPT_EDGE",EDGE,{"disambiguationData":[OSD([sQuery(id+"F1.wireOp",EDGE,"E33.1.0.1"),sQuery(id+"F1.wireOp",EDGE,"E33.1.0.12")])]});
            var Q13;
            Q13=makeQuery(id+"F2.opExtrude","SWEPT_EDGE",EDGE,{"disambiguationData":[OSD([sQuery(id+"F1.wireOp",EDGE,"E33.1.0.3"),sQuery(id+"F1.wireOp",EDGE,"E33.1.0.12")])]});
            var Q14;
            Q14=makeQuery(id+"F2.opExtrude","SWEPT_EDGE",EDGE,{"disambiguationData":[OSD([sQuery(id+"F1.wireOp",EDGE,"E33.2.0.3"),sQuery(id+"F1.wireOp",EDGE,"E33.2.0.12")])]});
            var Q15;
            Q15=makeQuery(id+"F2.opExtrude","SWEPT_EDGE",EDGE,{"disambiguationData":[OSD([sQuery(id+"F1.wireOp",EDGE,"E33.3.0.3"),sQuery(id+"F1.wireOp",EDGE,"E33.3.0.12")])]});
            var Q16;
            Q16=makeQuery(id+"F2.opExtrude","SWEPT_EDGE",EDGE,{"disambiguationData":[OSD([sQuery(id+"F1.wireOp",EDGE,"E33.4.0.3"),sQuery(id+"F1.wireOp",EDGE,"E33.4.0.12")])]});
            var Q17;
            Q17=makeQuery(id+"F2.opExtrude","SWEPT_EDGE",EDGE,{"disambiguationData":[OSD([sQuery(id+"F1.wireOp",EDGE,"E33.2.0.1"),sQuery(id+"F1.wireOp",EDGE,"E33.2.0.12")])]});
            var Q18;
            Q18=makeQuery(id+"F2.opExtrude","SWEPT_EDGE",EDGE,{"disambiguationData":[OSD([sQuery(id+"F1.wireOp",EDGE,"E33.3.0.1"),sQuery(id+"F1.wireOp",EDGE,"E33.3.0.12")])]});
            var Q19;
            {var subQ0=sQuery(id+"F1.wireOp",EDGE,"E23.left");var subQ1=sQuery(id+"F1.wireOp",EDGE,"E23.bottom");Q19=makeQuery(id+"F3.boolean.opBoolean","MERGE",EDGE,{"derivedFrom":[makeQuery(id+"F2.opExtrude","SWEPT_EDGE",EDGE,{"disambiguationData":[OSD([subQ1,subQ0])]}),makeQuery(id+"F3.opExtrude","SWEPT_EDGE",EDGE,{"disambiguationData":[OSD([subQ1,subQ0])]})]});}
            var Q20;
            {var subQ0=sQuery(id+"F1.wireOp",EDGE,"E23.right");var subQ1=sQuery(id+"F1.wireOp",EDGE,"E23.bottom");Q20=makeQuery(id+"F3.boolean.opBoolean","MERGE",EDGE,{"derivedFrom":[makeQuery(id+"F2.opExtrude","SWEPT_EDGE",EDGE,{"disambiguationData":[OSD([subQ1,subQ0])]}),makeQuery(id+"F3.opExtrude","SWEPT_EDGE",EDGE,{"disambiguationData":[OSD([subQ1,subQ0])]})]});}
            var Q21;
            {var subQ0=sQuery(id+"F1.wireOp",EDGE,"E26.MirrorCS");var subQ1=sQuery(id+"F1.wireOp",EDGE,"E24.MirrorCS");Q21=makeQuery(id+"F3.boolean.opBoolean","MERGE",EDGE,{"derivedFrom":[makeQuery(id+"F2.opExtrude","SWEPT_EDGE",EDGE,{"disambiguationData":[OSD([subQ1,subQ0])]}),makeQuery(id+"F3.opExtrude","SWEPT_EDGE",EDGE,{"disambiguationData":[OSD([subQ1,subQ0])]})]});}
            var Q22;
            {var subQ0=sQuery(id+"F1.wireOp",EDGE,"E33.1.0.20");var subQ1=sQuery(id+"F1.wireOp",EDGE,"E33.1.0.1");Q22=makeQuery(id+"F3.boolean.opBoolean","MERGE",EDGE,{"derivedFrom":[makeQuery(id+"F2.opExtrude","SWEPT_EDGE",EDGE,{"disambiguationData":[OSD([subQ1,subQ0])]}),makeQuery(id+"F3.opExtrude","SWEPT_EDGE",EDGE,{"disambiguationData":[OSD([subQ1,subQ0])]})]});}
            var Q23;
            {var subQ0=sQuery(id+"F1.wireOp",EDGE,"E33.1.0.6");var subQ1=sQuery(id+"F1.wireOp",EDGE,"E33.1.0.3");Q23=makeQuery(id+"F3.boolean.opBoolean","MERGE",EDGE,{"derivedFrom":[makeQuery(id+"F2.opExtrude","SWEPT_EDGE",EDGE,{"disambiguationData":[OSD([subQ1,subQ0])]}),makeQuery(id+"F3.opExtrude","SWEPT_EDGE",EDGE,{"disambiguationData":[OSD([subQ1,subQ0])]})]});}
            var Q24;
            {var subQ0=sQuery(id+"F1.wireOp",EDGE,"E33.2.0.20");var subQ1=sQuery(id+"F1.wireOp",EDGE,"E33.2.0.1");Q24=makeQuery(id+"F3.boolean.opBoolean","MERGE",EDGE,{"derivedFrom":[makeQuery(id+"F2.opExtrude","SWEPT_EDGE",EDGE,{"disambiguationData":[OSD([subQ1,subQ0])]}),makeQuery(id+"F3.opExtrude","SWEPT_EDGE",EDGE,{"disambiguationData":[OSD([subQ1,subQ0])]})]});}
            var Q25;
            {var subQ0=sQuery(id+"F1.wireOp",EDGE,"E33.2.0.6");var subQ1=sQuery(id+"F1.wireOp",EDGE,"E33.2.0.3");Q25=makeQuery(id+"F3.boolean.opBoolean","MERGE",EDGE,{"derivedFrom":[makeQuery(id+"F2.opExtrude","SWEPT_EDGE",EDGE,{"disambiguationData":[OSD([subQ1,subQ0])]}),makeQuery(id+"F3.opExtrude","SWEPT_EDGE",EDGE,{"disambiguationData":[OSD([subQ1,subQ0])]})]});}
            var Q26;
            {var subQ0=sQuery(id+"F1.wireOp",EDGE,"E33.3.0.6");var subQ1=sQuery(id+"F1.wireOp",EDGE,"E33.3.0.3");Q26=makeQuery(id+"F3.boolean.opBoolean","MERGE",EDGE,{"derivedFrom":[makeQuery(id+"F2.opExtrude","SWEPT_EDGE",EDGE,{"disambiguationData":[OSD([subQ1,subQ0])]}),makeQuery(id+"F3.opExtrude","SWEPT_EDGE",EDGE,{"disambiguationData":[OSD([subQ1,subQ0])]})]});}
            var Q27;
            {var subQ0=sQuery(id+"F1.wireOp",EDGE,"E33.4.0.20");var subQ1=sQuery(id+"F1.wireOp",EDGE,"E33.4.0.1");Q27=makeQuery(id+"F3.boolean.opBoolean","MERGE",EDGE,{"derivedFrom":[makeQuery(id+"F2.opExtrude","SWEPT_EDGE",EDGE,{"disambiguationData":[OSD([subQ1,subQ0])]}),makeQuery(id+"F3.opExtrude","SWEPT_EDGE",EDGE,{"disambiguationData":[OSD([subQ1,subQ0])]})]});}
            var Q28;
            {var subQ0=sQuery(id+"F1.wireOp",EDGE,"E33.4.0.6");var subQ1=sQuery(id+"F1.wireOp",EDGE,"E33.4.0.3");Q28=makeQuery(id+"F3.boolean.opBoolean","MERGE",EDGE,{"derivedFrom":[makeQuery(id+"F2.opExtrude","SWEPT_EDGE",EDGE,{"disambiguationData":[OSD([subQ1,subQ0])]}),makeQuery(id+"F3.opExtrude","SWEPT_EDGE",EDGE,{"disambiguationData":[OSD([subQ1,subQ0])]})]});}
            var Q29;
            {var subQ0=sQuery(id+"F1.wireOp",EDGE,"E33.4.0.6");var subQ1=sQuery(id+"F1.wireOp",EDGE,"E33.4.0.4");Q29=makeQuery(id+"F3.boolean.opBoolean","MERGE",EDGE,{"derivedFrom":[makeQuery(id+"F2.opExtrude","SWEPT_EDGE",EDGE,{"disambiguationData":[OSD([subQ1,subQ0])]}),makeQuery(id+"F3.opExtrude","SWEPT_EDGE",EDGE,{"disambiguationData":[OSD([subQ1,subQ0])]})]});}
            var Q30;
            {var subQ0=sQuery(id+"F1.wireOp",EDGE,"E33.4.0.11");var subQ1=sQuery(id+"F1.wireOp",EDGE,"E33.4.0.4");Q30=makeQuery(id+"F3.boolean.opBoolean","MERGE",EDGE,{"derivedFrom":[makeQuery(id+"F2.opExtrude","SWEPT_EDGE",EDGE,{"disambiguationData":[OSD([subQ1,subQ0])]}),makeQuery(id+"F3.opExtrude","SWEPT_EDGE",EDGE,{"disambiguationData":[OSD([subQ1,subQ0])]})]});}
            var Q31;
            {var subQ0=sQuery(id+"F1.wireOp",EDGE,"E33.4.0.11");var subQ1=sQuery(id+"F1.wireOp",EDGE,"E33.4.0.9");Q31=makeQuery(id+"F3.boolean.opBoolean","MERGE",EDGE,{"derivedFrom":[makeQuery(id+"F2.opExtrude","SWEPT_EDGE",EDGE,{"disambiguationData":[OSD([subQ1,subQ0])]}),makeQuery(id+"F3.opExtrude","SWEPT_EDGE",EDGE,{"disambiguationData":[OSD([subQ1,subQ0])]})]});}
            var Q32;
            {var subQ0=sQuery(id+"F1.wireOp",EDGE,"E33.4.0.15");var subQ1=sQuery(id+"F1.wireOp",EDGE,"E33.4.0.8");Q32=makeQuery(id+"F3.boolean.opBoolean","MERGE",EDGE,{"derivedFrom":[makeQuery(id+"F2.opExtrude","SWEPT_EDGE",EDGE,{"disambiguationData":[OSD([subQ1,subQ0])]}),makeQuery(id+"F3.opExtrude","SWEPT_EDGE",EDGE,{"disambiguationData":[OSD([subQ1,subQ0])]})]});}
            var Q33;
            {var subQ0=sQuery(id+"F1.wireOp",EDGE,"E33.3.0.11");var subQ1=sQuery(id+"F1.wireOp",EDGE,"E33.3.0.9");Q33=makeQuery(id+"F3.boolean.opBoolean","MERGE",EDGE,{"derivedFrom":[makeQuery(id+"F2.opExtrude","SWEPT_EDGE",EDGE,{"disambiguationData":[OSD([subQ1,subQ0])]}),makeQuery(id+"F3.opExtrude","SWEPT_EDGE",EDGE,{"disambiguationData":[OSD([subQ1,subQ0])]})]});}
            var Q34;
            {var subQ0=sQuery(id+"F1.wireOp",EDGE,"E33.2.0.15");var subQ1=sQuery(id+"F1.wireOp",EDGE,"E33.2.0.8");Q34=makeQuery(id+"F3.boolean.opBoolean","MERGE",EDGE,{"derivedFrom":[makeQuery(id+"F2.opExtrude","SWEPT_EDGE",EDGE,{"disambiguationData":[OSD([subQ1,subQ0])]}),makeQuery(id+"F3.opExtrude","SWEPT_EDGE",EDGE,{"disambiguationData":[OSD([subQ1,subQ0])]})]});}
            var Q35;
            {var subQ0=sQuery(id+"F1.wireOp",EDGE,"E33.1.0.11");var subQ1=sQuery(id+"F1.wireOp",EDGE,"E33.1.0.9");Q35=makeQuery(id+"F3.boolean.opBoolean","MERGE",EDGE,{"derivedFrom":[makeQuery(id+"F2.opExtrude","SWEPT_EDGE",EDGE,{"disambiguationData":[OSD([subQ1,subQ0])]}),makeQuery(id+"F3.opExtrude","SWEPT_EDGE",EDGE,{"disambiguationData":[OSD([subQ1,subQ0])]})]});}
            var Q36;
            {var subQ0=sQuery(id+"F1.wireOp",EDGE,"E33.1.0.15");var subQ1=sQuery(id+"F1.wireOp",EDGE,"E33.1.0.8");Q36=makeQuery(id+"F3.boolean.opBoolean","MERGE",EDGE,{"derivedFrom":[makeQuery(id+"F2.opExtrude","SWEPT_EDGE",EDGE,{"disambiguationData":[OSD([subQ1,subQ0])]}),makeQuery(id+"F3.opExtrude","SWEPT_EDGE",EDGE,{"disambiguationData":[OSD([subQ1,subQ0])]})]});}
            var Q37;
            {var subQ0=sQuery(id+"F1.wireOp",EDGE,"E31.trimOffspring");var subQ1=sQuery(id+"F1.wireOp",EDGE,"E23.top");Q37=makeQuery(id+"F3.boolean.opBoolean","MERGE",EDGE,{"derivedFrom":[makeQuery(id+"F2.opExtrude","SWEPT_EDGE",EDGE,{"disambiguationData":[OSD([subQ1,subQ0])]}),makeQuery(id+"F3.opExtrude","SWEPT_EDGE",EDGE,{"disambiguationData":[OSD([subQ1,subQ0])]})]});}
            var Q38;
            {var subQ0=sQuery(id+"F1.wireOp",EDGE,"E23.left");var subQ1=sQuery(id+"F1.wireOp",EDGE,"E23.top");Q38=makeQuery(id+"F3.boolean.opBoolean","MERGE",EDGE,{"derivedFrom":[makeQuery(id+"F2.opExtrude","SWEPT_EDGE",EDGE,{"disambiguationData":[OSD([subQ1,subQ0])]}),makeQuery(id+"F3.opExtrude","SWEPT_EDGE",EDGE,{"disambiguationData":[OSD([subQ1,subQ0])]})]});}
            var Q39;
            {var subQ0=sQuery(id+"F1.wireOp",EDGE,"E33.2.0.11");var subQ1=sQuery(id+"F1.wireOp",EDGE,"E33.2.0.9");Q39=makeQuery(id+"F3.boolean.opBoolean","MERGE",EDGE,{"derivedFrom":[makeQuery(id+"F2.opExtrude","SWEPT_EDGE",EDGE,{"disambiguationData":[OSD([subQ1,subQ0])]}),makeQuery(id+"F3.opExtrude","SWEPT_EDGE",EDGE,{"disambiguationData":[OSD([subQ1,subQ0])]})]});}
            var Q40;
            {var subQ0=sQuery(id+"F1.wireOp",EDGE,"E33.3.0.15");var subQ1=sQuery(id+"F1.wireOp",EDGE,"E33.3.0.8");Q40=makeQuery(id+"F3.boolean.opBoolean","MERGE",EDGE,{"derivedFrom":[makeQuery(id+"F2.opExtrude","SWEPT_EDGE",EDGE,{"disambiguationData":[OSD([subQ1,subQ0])]}),makeQuery(id+"F3.opExtrude","SWEPT_EDGE",EDGE,{"disambiguationData":[OSD([subQ1,subQ0])]})]});}
            var Q41;
            {var subQ0=sQuery(id+"F1.wireOp",EDGE,"E32.trimOffspring");var subQ1=sQuery(id+"F1.wireOp",EDGE,"E27.MirrorCS");Q41=makeQuery(id+"F3.boolean.opBoolean","MERGE",EDGE,{"derivedFrom":[makeQuery(id+"F2.opExtrude","SWEPT_EDGE",EDGE,{"disambiguationData":[OSD([subQ1,subQ0])]}),makeQuery(id+"F3.opExtrude","SWEPT_EDGE",EDGE,{"disambiguationData":[OSD([subQ1,subQ0])]})]});}
            var Q42;
            {var subQ0=sQuery(id+"F1.wireOp",EDGE,"E33.3.0.20");var subQ1=sQuery(id+"F1.wireOp",EDGE,"E33.3.0.1");Q42=makeQuery(id+"F3.boolean.opBoolean","MERGE",EDGE,{"derivedFrom":[makeQuery(id+"F2.opExtrude","SWEPT_EDGE",EDGE,{"disambiguationData":[OSD([subQ1,subQ0])]}),makeQuery(id+"F3.opExtrude","SWEPT_EDGE",EDGE,{"disambiguationData":[OSD([subQ1,subQ0])]})]});}
            var Q43;
            Q43=makeQuery(id+"F9.opExtrude","SWEPT_EDGE",EDGE,{"disambiguationData":[OSD([sQuery(id+"F1.wireOp",EDGE,"E23.top"),sQuery(id+"F1.wireOp",EDGE,"E23.left")])]});
            var Q44;
            Q44=makeQuery(id+"F9.opExtrude","SWEPT_EDGE",EDGE,{"disambiguationData":[OSD([sQuery(id+"F1.wireOp",EDGE,"E23.top"),sQuery(id+"F1.wireOp",EDGE,"E31.trimOffspring")])]});
            var Q45;
            Q45=makeQuery(id+"F9.opExtrude","SWEPT_EDGE",EDGE,{"disambiguationData":[OSD([sQuery(id+"F1.wireOp",EDGE,"E27.MirrorCS"),sQuery(id+"F1.wireOp",EDGE,"E32.trimOffspring")])]});
            var Q46;
            Q46=makeQuery(id+"F9.opExtrude","SWEPT_EDGE",EDGE,{"disambiguationData":[OSD([sQuery(id+"F1.wireOp",EDGE,"E33.1.0.8"),sQuery(id+"F1.wireOp",EDGE,"E33.1.0.15")])]});
            var Q47;
            Q47=makeQuery(id+"F9.opExtrude","SWEPT_EDGE",EDGE,{"disambiguationData":[OSD([sQuery(id+"F1.wireOp",EDGE,"E33.1.0.9"),sQuery(id+"F1.wireOp",EDGE,"E33.1.0.11")])]});
            var Q48;
            Q48=makeQuery(id+"F9.opExtrude","SWEPT_EDGE",EDGE,{"disambiguationData":[OSD([sQuery(id+"F1.wireOp",EDGE,"E33.2.0.8"),sQuery(id+"F1.wireOp",EDGE,"E33.2.0.15")])]});
            var Q49;
            Q49=makeQuery(id+"F9.opExtrude","SWEPT_EDGE",EDGE,{"disambiguationData":[OSD([sQuery(id+"F1.wireOp",EDGE,"E33.2.0.9"),sQuery(id+"F1.wireOp",EDGE,"E33.2.0.11")])]});
            var Q50;
            Q50=makeQuery(id+"F9.opExtrude","SWEPT_EDGE",EDGE,{"disambiguationData":[OSD([sQuery(id+"F1.wireOp",EDGE,"E33.3.0.8"),sQuery(id+"F1.wireOp",EDGE,"E33.3.0.15")])]});
            var Q51;
            Q51=makeQuery(id+"F9.opExtrude","SWEPT_EDGE",EDGE,{"disambiguationData":[OSD([sQuery(id+"F1.wireOp",EDGE,"E33.3.0.9"),sQuery(id+"F1.wireOp",EDGE,"E33.3.0.11")])]});
            var Q52;
            Q52=makeQuery(id+"F9.opExtrude","SWEPT_EDGE",EDGE,{"disambiguationData":[OSD([sQuery(id+"F1.wireOp",EDGE,"E33.4.0.8"),sQuery(id+"F1.wireOp",EDGE,"E33.4.0.15")])]});
            var Q53;
            Q53=makeQuery(id+"F9.opExtrude","SWEPT_EDGE",EDGE,{"disambiguationData":[OSD([sQuery(id+"F1.wireOp",EDGE,"E33.4.0.9"),sQuery(id+"F1.wireOp",EDGE,"E33.4.0.11")])]});
            var Q54;
            Q54=makeQuery(id+"F9.opExtrude","SWEPT_EDGE",EDGE,{"disambiguationData":[OSD([sQuery(id+"F1.wireOp",EDGE,"E33.4.0.4"),sQuery(id+"F1.wireOp",EDGE,"E33.4.0.11")])]});
            var Q55;
            Q55=makeQuery(id+"F10.opExtrude","SWEPT_EDGE",EDGE,{"disambiguationData":[OSD([sQuery(id+"F7.wireOp",EDGE,"E78.0.0"),sQuery(id+"F7.wireOp",EDGE,"E109")])]});
            var Q56;
            Q56=makeQuery(id+"F10.opExtrude","SWEPT_EDGE",EDGE,{"disambiguationData":[OSD([sQuery(id+"F7.wireOp",EDGE,"E78.0.2"),sQuery(id+"F7.wireOp",EDGE,"E109")])]});
            var Q57;
            Q57=makeQuery(id+"F10.opExtrude","SWEPT_EDGE",EDGE,{"disambiguationData":[OSD([sQuery(id+"F7.wireOp",EDGE,"E68.0.0"),sQuery(id+"F7.wireOp",EDGE,"E109")])]});
            var Q58;
            Q58=makeQuery(id+"F10.opExtrude","SWEPT_EDGE",EDGE,{"disambiguationData":[OSD([sQuery(id+"F7.wireOp",EDGE,"E68.0.2"),sQuery(id+"F7.wireOp",EDGE,"E109")])]});
            var Q59;
            Q59=makeQuery(id+"F10.opExtrude","SWEPT_EDGE",EDGE,{"disambiguationData":[OSD([sQuery(id+"F7.wireOp",EDGE,"E70.0.0"),sQuery(id+"F7.wireOp",EDGE,"E109")])]});
            var Q60;
            Q60=makeQuery(id+"F10.opExtrude","SWEPT_EDGE",EDGE,{"disambiguationData":[OSD([sQuery(id+"F7.wireOp",EDGE,"E70.0.2"),sQuery(id+"F7.wireOp",EDGE,"E109")])]});
            var Q61;
            Q61=makeQuery(id+"F10.opExtrude","SWEPT_EDGE",EDGE,{"disambiguationData":[OSD([sQuery(id+"F7.wireOp",EDGE,"E71.0.1"),sQuery(id+"F7.wireOp",EDGE,"E109")])]});
            var Q62;
            Q62=makeQuery(id+"F10.opExtrude","SWEPT_EDGE",EDGE,{"disambiguationData":[OSD([sQuery(id+"F7.wireOp",EDGE,"E71.0.3"),sQuery(id+"F7.wireOp",EDGE,"E109")])]});
            var Q63;
            Q63=makeQuery(id+"F10.opExtrude","SWEPT_EDGE",EDGE,{"disambiguationData":[OSD([sQuery(id+"F7.wireOp",EDGE,"E72.0.0"),sQuery(id+"F7.wireOp",EDGE,"E109")])]});
            var Q64;
            Q64=makeQuery(id+"F10.opExtrude","SWEPT_EDGE",EDGE,{"disambiguationData":[OSD([sQuery(id+"F7.wireOp",EDGE,"E72.0.2"),sQuery(id+"F7.wireOp",EDGE,"E109")])]});
            var Q65;
            Q65=makeQuery(id+"F10.opExtrude","SWEPT_EDGE",EDGE,{"disambiguationData":[OSD([sQuery(id+"F7.wireOp",EDGE,"E73.0.0"),sQuery(id+"F7.wireOp",EDGE,"E109")])]});
            var Q66;
            Q66=makeQuery(id+"F10.opExtrude","SWEPT_EDGE",EDGE,{"disambiguationData":[OSD([sQuery(id+"F7.wireOp",EDGE,"E73.0.2"),sQuery(id+"F7.wireOp",EDGE,"E109")])]});
            fillet(context, id + "F13", {"entities" : qUnion([Q0, Q1, Q2, Q3, Q4, Q5, Q6, Q7, Q8, Q9, Q10, Q11, Q12, Q13, Q14, Q15, Q16, Q17, Q18, Q19, Q20, Q21, Q22, Q23, Q24, Q25, Q26, Q27, Q28, Q29, Q30, Q31, Q32, Q33, Q34, Q35, Q36, Q37, Q38, Q39, Q40, Q41, Q42, Q43, Q44, Q45, Q46, Q47, Q48, Q49, Q50, Q51, Q52, Q53, Q54, Q55, Q56, Q57, Q58, Q59, Q60, Q61, Q62, Q63, Q64, Q65, Q66]), "radius" : 2 * mm, "allowEdgeOverflow" : false});
        }
        {
            var Q0;
            {var subQ0=sQuery(id+"F7.wireOp",EDGE,"E109");var subQ1=sQuery(id+"F7.wireOp",EDGE,"E78.0.2");var subQ2=sQuery(id+"F7.wireOp",EDGE,"E78.0.1");var subQ3=sQuery(id+"F7.wireOp",EDGE,"E78.0.0");var subQ4=sQuery(id+"F7.wireOp",EDGE,"E73.0.2");var subQ5=sQuery(id+"F7.wireOp",EDGE,"E73.0.1");var subQ6=sQuery(id+"F7.wireOp",EDGE,"E73.0.0");var subQ7=sQuery(id+"F7.wireOp",EDGE,"E72.0.2");var subQ8=sQuery(id+"F7.wireOp",EDGE,"E72.0.1");var subQ9=sQuery(id+"F7.wireOp",EDGE,"E72.0.0");var subQ10=sQuery(id+"F7.wireOp",EDGE,"E71.0.3");var subQ11=sQuery(id+"F7.wireOp",EDGE,"E71.0.2");var subQ12=sQuery(id+"F7.wireOp",EDGE,"E71.0.1");var subQ13=sQuery(id+"F7.wireOp",EDGE,"E70.0.2");var subQ14=sQuery(id+"F7.wireOp",EDGE,"E70.0.1");var subQ15=sQuery(id+"F7.wireOp",EDGE,"E70.0.0");var subQ16=sQuery(id+"F7.wireOp",EDGE,"E68.0.2");var subQ17=sQuery(id+"F7.wireOp",EDGE,"E68.0.1");var subQ18=sQuery(id+"F7.wireOp",EDGE,"E68.0.0");Q0=makeQuery(id+"F10.boolean.opBoolean","MERGE",FACE,{"derivedFrom":[makeQuery(id+"F9.boolean.opBoolean","MERGE",FACE,{"derivedFrom":[makeQuery(id+"F8.opExtrude","CAP_FACE",FACE,{"disambiguationData":[OSD([subQ18,subQ17,subQ16,subQ15,subQ14,subQ13,subQ12,subQ11,subQ10,subQ9,subQ8,subQ7,subQ6,subQ5,subQ4,subQ3,subQ2,subQ1,sQuery(id+"F7.wireOp",EDGE,"E84.0.0"),sQuery(id+"F7.wireOp",EDGE,"E84.0.1"),sQuery(id+"F7.wireOp",EDGE,"E84.0.3"),sQuery(id+"F7.wireOp",EDGE,"E86.0.0"),sQuery(id+"F7.wireOp",EDGE,"E86.0.1"),sQuery(id+"F7.wireOp",EDGE,"E86.0.3"),sQuery(id+"F7.wireOp",EDGE,"E91.0.1"),sQuery(id+"F7.wireOp",EDGE,"E91.0.2"),sQuery(id+"F7.wireOp",EDGE,"E91.0.3"),sQuery(id+"F7.wireOp",EDGE,"E94.0.1"),sQuery(id+"F7.wireOp",EDGE,"E94.0.2"),sQuery(id+"F7.wireOp",EDGE,"E94.0.3"),sQuery(id+"F7.wireOp",EDGE,"E99.0.0"),sQuery(id+"F7.wireOp",EDGE,"E99.0.1"),sQuery(id+"F7.wireOp",EDGE,"E99.0.3"),sQuery(id+"F7.wireOp",EDGE,"E100.0.1"),sQuery(id+"F7.wireOp",EDGE,"E100.0.2"),sQuery(id+"F7.wireOp",EDGE,"E100.0.3"),sQuery(id+"F7.wireOp",EDGE,"E102.0"),sQuery(id+"F7.wireOp",EDGE,"E102.1"),sQuery(id+"F7.wireOp",EDGE,"E102.2"),sQuery(id+"F7.wireOp",EDGE,"E102.3"),sQuery(id+"F7.wireOp",EDGE,"E103.left"),sQuery(id+"F7.wireOp",EDGE,"E103.right"),sQuery(id+"F7.wireOp",EDGE,"E105"),subQ0])],"isStart":false}),makeQuery(id+"F9.opExtrude","CAP_FACE",FACE,{"disambiguationData":[OSD([sQuery(id+"F1.wireOp",EDGE,"E16"),sQuery(id+"F1.wireOp",EDGE,"E23.top"),sQuery(id+"F1.wireOp",EDGE,"E23.left"),sQuery(id+"F1.wireOp",EDGE,"E31.trimOffspring"),sQuery(id+"F1.wireOp",EDGE,"E40.MirrorCS")])],"isStart":false}),makeQuery(id+"F9.opExtrude","CAP_FACE",FACE,{"disambiguationData":[OSD([sQuery(id+"F1.wireOp",EDGE,"E20.MirrorC"),sQuery(id+"F1.wireOp",EDGE,"E27.MirrorCS"),sQuery(id+"F1.wireOp",EDGE,"E32.trimOffspring"),sQuery(id+"F1.wireOp",EDGE,"E33.1.0.8"),sQuery(id+"F1.wireOp",EDGE,"E33.1.0.15"),sQuery(id+"F1.wireOp",EDGE,"E33.1.0.22"),sQuery(id+"F1.wireOp",EDGE,"E41.MirrorCS")])],"isStart":false}),makeQuery(id+"F9.opExtrude","CAP_FACE",FACE,{"disambiguationData":[OSD([sQuery(id+"F1.wireOp",EDGE,"E33.1.0.9"),sQuery(id+"F1.wireOp",EDGE,"E33.1.0.11"),sQuery(id+"F1.wireOp",EDGE,"E33.1.0.19"),sQuery(id+"F1.wireOp",EDGE,"E33.2.0.8"),sQuery(id+"F1.wireOp",EDGE,"E33.2.0.15"),sQuery(id+"F1.wireOp",EDGE,"E33.2.0.22"),sQuery(id+"F1.wireOp",EDGE,"E42.MirrorCS")])],"isStart":false}),makeQuery(id+"F9.opExtrude","CAP_FACE",FACE,{"disambiguationData":[OSD([sQuery(id+"F1.wireOp",EDGE,"E33.2.0.9"),sQuery(id+"F1.wireOp",EDGE,"E33.2.0.11"),sQuery(id+"F1.wireOp",EDGE,"E33.2.0.19"),sQuery(id+"F1.wireOp",EDGE,"E33.3.0.8"),sQuery(id+"F1.wireOp",EDGE,"E33.3.0.15"),sQuery(id+"F1.wireOp",EDGE,"E33.3.0.22"),sQuery(id+"F1.wireOp",EDGE,"E43.MirrorCS")])],"isStart":false}),makeQuery(id+"F9.opExtrude","CAP_FACE",FACE,{"disambiguationData":[OSD([sQuery(id+"F1.wireOp",EDGE,"E33.3.0.9"),sQuery(id+"F1.wireOp",EDGE,"E33.3.0.11"),sQuery(id+"F1.wireOp",EDGE,"E33.3.0.19"),sQuery(id+"F1.wireOp",EDGE,"E33.4.0.8"),sQuery(id+"F1.wireOp",EDGE,"E33.4.0.15"),sQuery(id+"F1.wireOp",EDGE,"E33.4.0.22"),sQuery(id+"F1.wireOp",EDGE,"E44.MirrorCS")])],"isStart":false}),makeQuery(id+"F9.opExtrude","CAP_FACE",FACE,{"disambiguationData":[OSD([sQuery(id+"F1.wireOp",EDGE,"E33.4.0.4"),sQuery(id+"F1.wireOp",EDGE,"E33.4.0.9"),sQuery(id+"F1.wireOp",EDGE,"E33.4.0.11"),sQuery(id+"F1.wireOp",EDGE,"E33.4.0.19"),sQuery(id+"F1.wireOp",EDGE,"E45.MirrorCS")])],"isStart":false})]}),makeQuery(id+"F10.opExtrude","CAP_FACE",FACE,{"disambiguationData":[OSD([subQ18,subQ17,subQ16,sQuery(id+"F7.wireOp",EDGE,"E75.0"),sQuery(id+"F7.wireOp",EDGE,"E76.0"),subQ0])],"isStart":false}),makeQuery(id+"F10.opExtrude","CAP_FACE",FACE,{"disambiguationData":[OSD([sQuery(id+"F7.wireOp",EDGE,"E69.0"),subQ15,subQ14,subQ13,sQuery(id+"F7.wireOp",EDGE,"E74.0"),subQ0])],"isStart":false}),makeQuery(id+"F10.opExtrude","CAP_FACE",FACE,{"disambiguationData":[OSD([subQ12,subQ11,subQ10,sQuery(id+"F7.wireOp",EDGE,"E79.0"),sQuery(id+"F7.wireOp",EDGE,"E80.0"),subQ0])],"isStart":false}),makeQuery(id+"F10.opExtrude","CAP_FACE",FACE,{"disambiguationData":[OSD([subQ9,subQ8,subQ7,sQuery(id+"F7.wireOp",EDGE,"E81.0"),sQuery(id+"F7.wireOp",EDGE,"E82.0"),subQ0])],"isStart":false}),makeQuery(id+"F10.opExtrude","CAP_FACE",FACE,{"disambiguationData":[OSD([subQ6,subQ5,subQ4,sQuery(id+"F7.wireOp",EDGE,"E83.0"),subQ0])],"isStart":false}),makeQuery(id+"F10.opExtrude","CAP_FACE",FACE,{"disambiguationData":[OSD([sQuery(id+"F7.wireOp",EDGE,"E77.0"),subQ3,subQ2,subQ1,subQ0])],"isStart":false})]});}
            var sketch = newSketch(context, id + "F14", { "sketchPlane" : qUnion([Q0])});
            skLineSegment(sketch, "E120.bottom", {"start": v(-5, 50) * mm, "end": v(165.5, 50) * mm});
            skLineSegment(sketch, "E120.top", {"start": v(-5, -18.2) * mm, "end": v(165.5, -18.2) * mm});
            skLineSegment(sketch, "E120.left", {"start": v(-5, 50) * mm, "end": v(-5, -18.2) * mm});
            skLineSegment(sketch, "E120.right", {"start": v(165.5, 50) * mm, "end": v(165.5, -18.2) * mm});
            skLineSegment(sketch, "E121.0", {"start": v(160.8, 32.1) * mm, "end": v(-0.3, 32.1) * mm, "construction": true});
            skLineSegment(sketch, "E122.0", {"start": v(-0.3, -0.3) * mm, "end": v(160.8, -0.3) * mm, "construction": true});
            skPoint(sketch, "E123.0", {"position": v(-0.3, 15.9) * mm});
            skLineSegment(sketch, "E124.0", {"start": v(160.8, -0.3) * mm, "end": v(160.8, 32.1) * mm, "construction": true});
            skLineSegment(sketch, "E125.0", {"start": v(-0.3, 32.1) * mm, "end": v(-0.3, -0.3) * mm, "construction": true});
            skLineSegment(sketch, "E126.0", {"start": v(162.8, 34.1) * mm, "end": v(-2.3, 34.1) * mm});
            skLineSegment(sketch, "E126.1", {"start": v(162.8, -2.3) * mm, "end": v(162.8, 34.1) * mm});
            skLineSegment(sketch, "E126.2", {"start": v(-2.3, -2.3) * mm, "end": v(162.8, -2.3) * mm});
            skLineSegment(sketch, "E126.3", {"start": v(-2.3, 34.1) * mm, "end": v(-2.3, -2.3) * mm});
            skLineSegment(sketch, "E127.bottom", {"start": v(-5, 50) * mm, "end": v(-15, 50) * mm});
            skLineSegment(sketch, "E127.top", {"start": v(-5, -18.2) * mm, "end": v(-15, -18.2) * mm});
            skLineSegment(sketch, "E127.right", {"start": v(-15, 50) * mm, "end": v(-15, -18.2) * mm});
            skLineSegment(sketch, "E128.bottom", {"start": v(165.5, 50) * mm, "end": v(175.5, 50) * mm});
            skLineSegment(sketch, "E128.top", {"start": v(165.5, -18.2) * mm, "end": v(175.5, -18.2) * mm});
            skLineSegment(sketch, "E128.right", {"start": v(175.5, 50) * mm, "end": v(175.5, -18.2) * mm});
            skLineSegment(sketch, "E129.bottom", {"start": v(-15, 50) * mm, "end": v(175.5, 50) * mm});
            skLineSegment(sketch, "E129.top", {"start": v(-15, 60) * mm, "end": v(175.5, 60) * mm});
            skLineSegment(sketch, "E129.left", {"start": v(-15, 50) * mm, "end": v(-15, 60) * mm});
            skLineSegment(sketch, "E129.right", {"start": v(175.5, 50) * mm, "end": v(175.5, 60) * mm});
            skLineSegment(sketch, "E130.bottom", {"start": v(-15, -18.2) * mm, "end": v(175.5, -18.2) * mm});
            skLineSegment(sketch, "E130.top", {"start": v(-15, -28.2) * mm, "end": v(175.5, -28.2) * mm});
            skLineSegment(sketch, "E130.left", {"start": v(-15, -18.2) * mm, "end": v(-15, -28.2) * mm});
            skLineSegment(sketch, "E130.right", {"start": v(175.5, -18.2) * mm, "end": v(175.5, -28.2) * mm});
            skSolve(sketch);
        }
        {
            var Q0;
            Q0=makeQuery(id+"F14.imprint","IMPRINT",FACE,{"disambiguationData":[TD([[makeQuery(id+"F14.imprint","IMPRINT",EDGE,{"derivedFrom":sQuery(id+"F14.wireOp",EDGE,"E129.top")}),-1.0]])]});
            var Q1;
            {var subQ0=sQuery(id+"F14.wireOp",EDGE,"E120.left");Q1=makeQuery(id+"F14.imprint","IMPRINT",FACE,{"disambiguationData":[TD([[makeQuery(id+"F14.imprint","IMPRINT",EDGE,{"derivedFrom":subQ0}),-1.0]])]});}
            var Q2;
            {var subQ0=sQuery(id+"F14.wireOp",EDGE,"E120.right");Q2=makeQuery(id+"F14.imprint","IMPRINT",FACE,{"disambiguationData":[TD([[makeQuery(id+"F14.imprint","IMPRINT",EDGE,{"derivedFrom":subQ0}),1.0]])]});}
            var Q3;
            Q3=makeQuery(id+"F14.imprint","IMPRINT",FACE,{"disambiguationData":[TD([[makeQuery(id+"F14.imprint","IMPRINT",EDGE,{"derivedFrom":sQuery(id+"F14.wireOp",EDGE,"E126.0")}),-1.0]])]});
            var Q4;
            Q4=makeQuery(id+"F14.imprint","IMPRINT",FACE,{"disambiguationData":[TD([[makeQuery(id+"F14.imprint","IMPRINT",EDGE,{"derivedFrom":sQuery(id+"F14.wireOp",EDGE,"E130.top")}),1.0]])]});
            var Q5;
            Q5=makeQuery(id+"F14.imprint","IMPRINT",FACE,{"disambiguationData":[TD([[makeQuery(id+"F14.imprint","IMPRINT",EDGE,{"derivedFrom":makeQuery(id+"F10.opExtrude","CAP_EDGE",EDGE,{"disambiguationData":[OSD([sQuery(id+"F7.wireOp",EDGE,"E77.0")])],"isStart":false})}),1.0]])]});
            var Q6;
            {var subQ0=sQuery(id+"F7.wireOp",EDGE,"E109");var subQ1=sQuery(id+"F7.wireOp",EDGE,"E78.0.2");var subQ2=sQuery(id+"F7.wireOp",EDGE,"E78.0.1");var subQ3=sQuery(id+"F7.wireOp",EDGE,"E78.0.0");var subQ4=sQuery(id+"F7.wireOp",EDGE,"E73.0.2");var subQ5=sQuery(id+"F7.wireOp",EDGE,"E73.0.1");var subQ6=sQuery(id+"F7.wireOp",EDGE,"E73.0.0");var subQ7=sQuery(id+"F7.wireOp",EDGE,"E72.0.2");var subQ8=sQuery(id+"F7.wireOp",EDGE,"E72.0.1");var subQ9=sQuery(id+"F7.wireOp",EDGE,"E72.0.0");var subQ10=sQuery(id+"F7.wireOp",EDGE,"E71.0.3");var subQ11=sQuery(id+"F7.wireOp",EDGE,"E71.0.2");var subQ12=sQuery(id+"F7.wireOp",EDGE,"E71.0.1");var subQ13=sQuery(id+"F7.wireOp",EDGE,"E70.0.2");var subQ14=sQuery(id+"F7.wireOp",EDGE,"E70.0.1");var subQ15=sQuery(id+"F7.wireOp",EDGE,"E70.0.0");var subQ16=sQuery(id+"F7.wireOp",EDGE,"E68.0.2");var subQ17=sQuery(id+"F7.wireOp",EDGE,"E68.0.1");var subQ18=sQuery(id+"F7.wireOp",EDGE,"E68.0.0");Q6=makeQuery(id+"F14.imprint","IMPRINT",FACE,{"disambiguationData":[TD([[makeQuery(id+"F14.imprint","IMPRINT",EDGE,{"derivedFrom":makeQuery(id+"F12.boolean.opBoolean","INTERSECT",EDGE,{"derivedFrom":[makeQuery(id+"F10.boolean.opBoolean","MERGE",FACE,{"derivedFrom":[makeQuery(id+"F9.boolean.opBoolean","MERGE",FACE,{"derivedFrom":[makeQuery(id+"F8.opExtrude","CAP_FACE",FACE,{"disambiguationData":[OSD([subQ18,subQ17,subQ16,subQ15,subQ14,subQ13,subQ12,subQ11,subQ10,subQ9,subQ8,subQ7,subQ6,subQ5,subQ4,subQ3,subQ2,subQ1,sQuery(id+"F7.wireOp",EDGE,"E84.0.0"),sQuery(id+"F7.wireOp",EDGE,"E84.0.1"),sQuery(id+"F7.wireOp",EDGE,"E84.0.3"),sQuery(id+"F7.wireOp",EDGE,"E86.0.0"),sQuery(id+"F7.wireOp",EDGE,"E86.0.1"),sQuery(id+"F7.wireOp",EDGE,"E86.0.3"),sQuery(id+"F7.wireOp",EDGE,"E91.0.1"),sQuery(id+"F7.wireOp",EDGE,"E91.0.2"),sQuery(id+"F7.wireOp",EDGE,"E91.0.3"),sQuery(id+"F7.wireOp",EDGE,"E94.0.1"),sQuery(id+"F7.wireOp",EDGE,"E94.0.2"),sQuery(id+"F7.wireOp",EDGE,"E94.0.3"),sQuery(id+"F7.wireOp",EDGE,"E99.0.0"),sQuery(id+"F7.wireOp",EDGE,"E99.0.1"),sQuery(id+"F7.wireOp",EDGE,"E99.0.3"),sQuery(id+"F7.wireOp",EDGE,"E100.0.1"),sQuery(id+"F7.wireOp",EDGE,"E100.0.2"),sQuery(id+"F7.wireOp",EDGE,"E100.0.3"),sQuery(id+"F7.wireOp",EDGE,"E102.0"),sQuery(id+"F7.wireOp",EDGE,"E102.1"),sQuery(id+"F7.wireOp",EDGE,"E102.2"),sQuery(id+"F7.wireOp",EDGE,"E102.3"),sQuery(id+"F7.wireOp",EDGE,"E103.left"),sQuery(id+"F7.wireOp",EDGE,"E103.right"),sQuery(id+"F7.wireOp",EDGE,"E105"),subQ0])],"isStart":false}),makeQuery(id+"F9.opExtrude","CAP_FACE",FACE,{"disambiguationData":[OSD([sQuery(id+"F1.wireOp",EDGE,"E16"),sQuery(id+"F1.wireOp",EDGE,"E23.top"),sQuery(id+"F1.wireOp",EDGE,"E23.left"),sQuery(id+"F1.wireOp",EDGE,"E31.trimOffspring"),sQuery(id+"F1.wireOp",EDGE,"E40.MirrorCS")])],"isStart":false}),makeQuery(id+"F9.opExtrude","CAP_FACE",FACE,{"disambiguationData":[OSD([sQuery(id+"F1.wireOp",EDGE,"E20.MirrorC"),sQuery(id+"F1.wireOp",EDGE,"E27.MirrorCS"),sQuery(id+"F1.wireOp",EDGE,"E32.trimOffspring"),sQuery(id+"F1.wireOp",EDGE,"E33.1.0.8"),sQuery(id+"F1.wireOp",EDGE,"E33.1.0.15"),sQuery(id+"F1.wireOp",EDGE,"E33.1.0.22"),sQuery(id+"F1.wireOp",EDGE,"E41.MirrorCS")])],"isStart":false}),makeQuery(id+"F9.opExtrude","CAP_FACE",FACE,{"disambiguationData":[OSD([sQuery(id+"F1.wireOp",EDGE,"E33.1.0.9"),sQuery(id+"F1.wireOp",EDGE,"E33.1.0.11"),sQuery(id+"F1.wireOp",EDGE,"E33.1.0.19"),sQuery(id+"F1.wireOp",EDGE,"E33.2.0.8"),sQuery(id+"F1.wireOp",EDGE,"E33.2.0.15"),sQuery(id+"F1.wireOp",EDGE,"E33.2.0.22"),sQuery(id+"F1.wireOp",EDGE,"E42.MirrorCS")])],"isStart":false}),makeQuery(id+"F9.opExtrude","CAP_FACE",FACE,{"disambiguationData":[OSD([sQuery(id+"F1.wireOp",EDGE,"E33.2.0.9"),sQuery(id+"F1.wireOp",EDGE,"E33.2.0.11"),sQuery(id+"F1.wireOp",EDGE,"E33.2.0.19"),sQuery(id+"F1.wireOp",EDGE,"E33.3.0.8"),sQuery(id+"F1.wireOp",EDGE,"E33.3.0.15"),sQuery(id+"F1.wireOp",EDGE,"E33.3.0.22"),sQuery(id+"F1.wireOp",EDGE,"E43.MirrorCS")])],"isStart":false}),makeQuery(id+"F9.opExtrude","CAP_FACE",FACE,{"disambiguationData":[OSD([sQuery(id+"F1.wireOp",EDGE,"E33.3.0.9"),sQuery(id+"F1.wireOp",EDGE,"E33.3.0.11"),sQuery(id+"F1.wireOp",EDGE,"E33.3.0.19"),sQuery(id+"F1.wireOp",EDGE,"E33.4.0.8"),sQuery(id+"F1.wireOp",EDGE,"E33.4.0.15"),sQuery(id+"F1.wireOp",EDGE,"E33.4.0.22"),sQuery(id+"F1.wireOp",EDGE,"E44.MirrorCS")])],"isStart":false}),makeQuery(id+"F9.opExtrude","CAP_FACE",FACE,{"disambiguationData":[OSD([sQuery(id+"F1.wireOp",EDGE,"E33.4.0.4"),sQuery(id+"F1.wireOp",EDGE,"E33.4.0.9"),sQuery(id+"F1.wireOp",EDGE,"E33.4.0.11"),sQuery(id+"F1.wireOp",EDGE,"E33.4.0.19"),sQuery(id+"F1.wireOp",EDGE,"E45.MirrorCS")])],"isStart":false})]}),makeQuery(id+"F10.opExtrude","CAP_FACE",FACE,{"disambiguationData":[OSD([subQ18,subQ17,subQ16,sQuery(id+"F7.wireOp",EDGE,"E75.0"),sQuery(id+"F7.wireOp",EDGE,"E76.0"),subQ0])],"isStart":false}),makeQuery(id+"F10.opExtrude","CAP_FACE",FACE,{"disambiguationData":[OSD([sQuery(id+"F7.wireOp",EDGE,"E69.0"),subQ15,subQ14,subQ13,sQuery(id+"F7.wireOp",EDGE,"E74.0"),subQ0])],"isStart":false}),makeQuery(id+"F10.opExtrude","CAP_FACE",FACE,{"disambiguationData":[OSD([subQ12,subQ11,subQ10,sQuery(id+"F7.wireOp",EDGE,"E79.0"),sQuery(id+"F7.wireOp",EDGE,"E80.0"),subQ0])],"isStart":false}),makeQuery(id+"F10.opExtrude","CAP_FACE",FACE,{"disambiguationData":[OSD([subQ9,subQ8,subQ7,sQuery(id+"F7.wireOp",EDGE,"E81.0"),sQuery(id+"F7.wireOp",EDGE,"E82.0"),subQ0])],"isStart":false}),makeQuery(id+"F10.opExtrude","CAP_FACE",FACE,{"disambiguationData":[OSD([subQ6,subQ5,subQ4,sQuery(id+"F7.wireOp",EDGE,"E83.0"),subQ0])],"isStart":false}),makeQuery(id+"F10.opExtrude","CAP_FACE",FACE,{"disambiguationData":[OSD([sQuery(id+"F7.wireOp",EDGE,"E77.0"),subQ3,subQ2,subQ1,subQ0])],"isStart":false})]}),makeQuery(id+"F12.opExtrude","SWEPT_FACE",FACE,{"disambiguationData":[OSD([sQuery(id+"F11.wireOp",EDGE,"E114.MirrorC")])]})]})}),-1.0]])]});}
            var Q7;
            Q7=makeQuery(id+"F14.imprint","IMPRINT",FACE,{"disambiguationData":[TD([[makeQuery(id+"F14.imprint","IMPRINT",EDGE,{"derivedFrom":makeQuery(id+"F10.opExtrude","CAP_EDGE",EDGE,{"disambiguationData":[OSD([sQuery(id+"F7.wireOp",EDGE,"E76.0")])],"isStart":false})}),1.0]])]});
            var Q8;
            Q8=makeQuery(id+"F14.imprint","IMPRINT",FACE,{"disambiguationData":[TD([[makeQuery(id+"F14.imprint","IMPRINT",EDGE,{"derivedFrom":makeQuery(id+"F10.opExtrude","CAP_EDGE",EDGE,{"disambiguationData":[OSD([sQuery(id+"F7.wireOp",EDGE,"E75.0")])],"isStart":false})}),1.0]])]});
            var Q9;
            Q9=makeQuery(id+"F14.imprint","IMPRINT",FACE,{"disambiguationData":[TD([[makeQuery(id+"F14.imprint","IMPRINT",EDGE,{"derivedFrom":makeQuery(id+"F10.opExtrude","CAP_EDGE",EDGE,{"disambiguationData":[OSD([sQuery(id+"F7.wireOp",EDGE,"E74.0")])],"isStart":false})}),1.0]])]});
            var Q10;
            {var subQ0=sQuery(id+"F7.wireOp",EDGE,"E109");var subQ1=sQuery(id+"F7.wireOp",EDGE,"E78.0.2");var subQ2=sQuery(id+"F7.wireOp",EDGE,"E78.0.1");var subQ3=sQuery(id+"F7.wireOp",EDGE,"E78.0.0");var subQ4=sQuery(id+"F7.wireOp",EDGE,"E73.0.2");var subQ5=sQuery(id+"F7.wireOp",EDGE,"E73.0.1");var subQ6=sQuery(id+"F7.wireOp",EDGE,"E73.0.0");var subQ7=sQuery(id+"F7.wireOp",EDGE,"E72.0.2");var subQ8=sQuery(id+"F7.wireOp",EDGE,"E72.0.1");var subQ9=sQuery(id+"F7.wireOp",EDGE,"E72.0.0");var subQ10=sQuery(id+"F7.wireOp",EDGE,"E71.0.3");var subQ11=sQuery(id+"F7.wireOp",EDGE,"E71.0.2");var subQ12=sQuery(id+"F7.wireOp",EDGE,"E71.0.1");var subQ13=sQuery(id+"F7.wireOp",EDGE,"E70.0.2");var subQ14=sQuery(id+"F7.wireOp",EDGE,"E70.0.1");var subQ15=sQuery(id+"F7.wireOp",EDGE,"E70.0.0");var subQ16=sQuery(id+"F7.wireOp",EDGE,"E68.0.2");var subQ17=sQuery(id+"F7.wireOp",EDGE,"E68.0.1");var subQ18=sQuery(id+"F7.wireOp",EDGE,"E68.0.0");Q10=makeQuery(id+"F14.imprint","IMPRINT",FACE,{"disambiguationData":[TD([[makeQuery(id+"F14.imprint","IMPRINT",EDGE,{"derivedFrom":makeQuery(id+"F12.boolean.opBoolean","INTERSECT",EDGE,{"derivedFrom":[makeQuery(id+"F10.boolean.opBoolean","MERGE",FACE,{"derivedFrom":[makeQuery(id+"F9.boolean.opBoolean","MERGE",FACE,{"derivedFrom":[makeQuery(id+"F8.opExtrude","CAP_FACE",FACE,{"disambiguationData":[OSD([subQ18,subQ17,subQ16,subQ15,subQ14,subQ13,subQ12,subQ11,subQ10,subQ9,subQ8,subQ7,subQ6,subQ5,subQ4,subQ3,subQ2,subQ1,sQuery(id+"F7.wireOp",EDGE,"E84.0.0"),sQuery(id+"F7.wireOp",EDGE,"E84.0.1"),sQuery(id+"F7.wireOp",EDGE,"E84.0.3"),sQuery(id+"F7.wireOp",EDGE,"E86.0.0"),sQuery(id+"F7.wireOp",EDGE,"E86.0.1"),sQuery(id+"F7.wireOp",EDGE,"E86.0.3"),sQuery(id+"F7.wireOp",EDGE,"E91.0.1"),sQuery(id+"F7.wireOp",EDGE,"E91.0.2"),sQuery(id+"F7.wireOp",EDGE,"E91.0.3"),sQuery(id+"F7.wireOp",EDGE,"E94.0.1"),sQuery(id+"F7.wireOp",EDGE,"E94.0.2"),sQuery(id+"F7.wireOp",EDGE,"E94.0.3"),sQuery(id+"F7.wireOp",EDGE,"E99.0.0"),sQuery(id+"F7.wireOp",EDGE,"E99.0.1"),sQuery(id+"F7.wireOp",EDGE,"E99.0.3"),sQuery(id+"F7.wireOp",EDGE,"E100.0.1"),sQuery(id+"F7.wireOp",EDGE,"E100.0.2"),sQuery(id+"F7.wireOp",EDGE,"E100.0.3"),sQuery(id+"F7.wireOp",EDGE,"E102.0"),sQuery(id+"F7.wireOp",EDGE,"E102.1"),sQuery(id+"F7.wireOp",EDGE,"E102.2"),sQuery(id+"F7.wireOp",EDGE,"E102.3"),sQuery(id+"F7.wireOp",EDGE,"E103.left"),sQuery(id+"F7.wireOp",EDGE,"E103.right"),sQuery(id+"F7.wireOp",EDGE,"E105"),subQ0])],"isStart":false}),makeQuery(id+"F9.opExtrude","CAP_FACE",FACE,{"disambiguationData":[OSD([sQuery(id+"F1.wireOp",EDGE,"E16"),sQuery(id+"F1.wireOp",EDGE,"E23.top"),sQuery(id+"F1.wireOp",EDGE,"E23.left"),sQuery(id+"F1.wireOp",EDGE,"E31.trimOffspring"),sQuery(id+"F1.wireOp",EDGE,"E40.MirrorCS")])],"isStart":false}),makeQuery(id+"F9.opExtrude","CAP_FACE",FACE,{"disambiguationData":[OSD([sQuery(id+"F1.wireOp",EDGE,"E20.MirrorC"),sQuery(id+"F1.wireOp",EDGE,"E27.MirrorCS"),sQuery(id+"F1.wireOp",EDGE,"E32.trimOffspring"),sQuery(id+"F1.wireOp",EDGE,"E33.1.0.8"),sQuery(id+"F1.wireOp",EDGE,"E33.1.0.15"),sQuery(id+"F1.wireOp",EDGE,"E33.1.0.22"),sQuery(id+"F1.wireOp",EDGE,"E41.MirrorCS")])],"isStart":false}),makeQuery(id+"F9.opExtrude","CAP_FACE",FACE,{"disambiguationData":[OSD([sQuery(id+"F1.wireOp",EDGE,"E33.1.0.9"),sQuery(id+"F1.wireOp",EDGE,"E33.1.0.11"),sQuery(id+"F1.wireOp",EDGE,"E33.1.0.19"),sQuery(id+"F1.wireOp",EDGE,"E33.2.0.8"),sQuery(id+"F1.wireOp",EDGE,"E33.2.0.15"),sQuery(id+"F1.wireOp",EDGE,"E33.2.0.22"),sQuery(id+"F1.wireOp",EDGE,"E42.MirrorCS")])],"isStart":false}),makeQuery(id+"F9.opExtrude","CAP_FACE",FACE,{"disambiguationData":[OSD([sQuery(id+"F1.wireOp",EDGE,"E33.2.0.9"),sQuery(id+"F1.wireOp",EDGE,"E33.2.0.11"),sQuery(id+"F1.wireOp",EDGE,"E33.2.0.19"),sQuery(id+"F1.wireOp",EDGE,"E33.3.0.8"),sQuery(id+"F1.wireOp",EDGE,"E33.3.0.15"),sQuery(id+"F1.wireOp",EDGE,"E33.3.0.22"),sQuery(id+"F1.wireOp",EDGE,"E43.MirrorCS")])],"isStart":false}),makeQuery(id+"F9.opExtrude","CAP_FACE",FACE,{"disambiguationData":[OSD([sQuery(id+"F1.wireOp",EDGE,"E33.3.0.9"),sQuery(id+"F1.wireOp",EDGE,"E33.3.0.11"),sQuery(id+"F1.wireOp",EDGE,"E33.3.0.19"),sQuery(id+"F1.wireOp",EDGE,"E33.4.0.8"),sQuery(id+"F1.wireOp",EDGE,"E33.4.0.15"),sQuery(id+"F1.wireOp",EDGE,"E33.4.0.22"),sQuery(id+"F1.wireOp",EDGE,"E44.MirrorCS")])],"isStart":false}),makeQuery(id+"F9.opExtrude","CAP_FACE",FACE,{"disambiguationData":[OSD([sQuery(id+"F1.wireOp",EDGE,"E33.4.0.4"),sQuery(id+"F1.wireOp",EDGE,"E33.4.0.9"),sQuery(id+"F1.wireOp",EDGE,"E33.4.0.11"),sQuery(id+"F1.wireOp",EDGE,"E33.4.0.19"),sQuery(id+"F1.wireOp",EDGE,"E45.MirrorCS")])],"isStart":false})]}),makeQuery(id+"F10.opExtrude","CAP_FACE",FACE,{"disambiguationData":[OSD([subQ18,subQ17,subQ16,sQuery(id+"F7.wireOp",EDGE,"E75.0"),sQuery(id+"F7.wireOp",EDGE,"E76.0"),subQ0])],"isStart":false}),makeQuery(id+"F10.opExtrude","CAP_FACE",FACE,{"disambiguationData":[OSD([sQuery(id+"F7.wireOp",EDGE,"E69.0"),subQ15,subQ14,subQ13,sQuery(id+"F7.wireOp",EDGE,"E74.0"),subQ0])],"isStart":false}),makeQuery(id+"F10.opExtrude","CAP_FACE",FACE,{"disambiguationData":[OSD([subQ12,subQ11,subQ10,sQuery(id+"F7.wireOp",EDGE,"E79.0"),sQuery(id+"F7.wireOp",EDGE,"E80.0"),subQ0])],"isStart":false}),makeQuery(id+"F10.opExtrude","CAP_FACE",FACE,{"disambiguationData":[OSD([subQ9,subQ8,subQ7,sQuery(id+"F7.wireOp",EDGE,"E81.0"),sQuery(id+"F7.wireOp",EDGE,"E82.0"),subQ0])],"isStart":false}),makeQuery(id+"F10.opExtrude","CAP_FACE",FACE,{"disambiguationData":[OSD([subQ6,subQ5,subQ4,sQuery(id+"F7.wireOp",EDGE,"E83.0"),subQ0])],"isStart":false}),makeQuery(id+"F10.opExtrude","CAP_FACE",FACE,{"disambiguationData":[OSD([sQuery(id+"F7.wireOp",EDGE,"E77.0"),subQ3,subQ2,subQ1,subQ0])],"isStart":false})]}),makeQuery(id+"F12.opExtrude","SWEPT_FACE",FACE,{"disambiguationData":[OSD([sQuery(id+"F11.wireOp",EDGE,"E113")])]})]})}),1.0]])]});}
            var Q11;
            Q11=makeQuery(id+"F14.imprint","IMPRINT",FACE,{"disambiguationData":[TD([[makeQuery(id+"F14.imprint","IMPRINT",EDGE,{"derivedFrom":makeQuery(id+"F10.opExtrude","CAP_EDGE",EDGE,{"disambiguationData":[OSD([sQuery(id+"F7.wireOp",EDGE,"E83.0")])],"isStart":false})}),1.0]])]});
            var Q12;
            Q12=makeQuery(id+"F14.imprint","IMPRINT",FACE,{"disambiguationData":[TD([[makeQuery(id+"F14.imprint","IMPRINT",EDGE,{"derivedFrom":makeQuery(id+"F10.opExtrude","CAP_EDGE",EDGE,{"disambiguationData":[OSD([sQuery(id+"F7.wireOp",EDGE,"E80.0")])],"isStart":false})}),1.0]])]});
            var Q13;
            Q13=makeQuery(id+"F14.imprint","IMPRINT",FACE,{"disambiguationData":[TD([[makeQuery(id+"F14.imprint","IMPRINT",EDGE,{"derivedFrom":makeQuery(id+"F10.opExtrude","CAP_EDGE",EDGE,{"disambiguationData":[OSD([sQuery(id+"F7.wireOp",EDGE,"E69.0")])],"isStart":false})}),1.0]])]});
            var Q14;
            {var subQ0=sQuery(id+"F7.wireOp",EDGE,"E109");var subQ1=sQuery(id+"F7.wireOp",EDGE,"E78.0.2");var subQ2=sQuery(id+"F7.wireOp",EDGE,"E78.0.1");var subQ3=sQuery(id+"F7.wireOp",EDGE,"E78.0.0");var subQ4=sQuery(id+"F7.wireOp",EDGE,"E73.0.2");var subQ5=sQuery(id+"F7.wireOp",EDGE,"E73.0.1");var subQ6=sQuery(id+"F7.wireOp",EDGE,"E73.0.0");var subQ7=sQuery(id+"F7.wireOp",EDGE,"E72.0.2");var subQ8=sQuery(id+"F7.wireOp",EDGE,"E72.0.1");var subQ9=sQuery(id+"F7.wireOp",EDGE,"E72.0.0");var subQ10=sQuery(id+"F7.wireOp",EDGE,"E71.0.3");var subQ11=sQuery(id+"F7.wireOp",EDGE,"E71.0.2");var subQ12=sQuery(id+"F7.wireOp",EDGE,"E71.0.1");var subQ13=sQuery(id+"F7.wireOp",EDGE,"E70.0.2");var subQ14=sQuery(id+"F7.wireOp",EDGE,"E70.0.1");var subQ15=sQuery(id+"F7.wireOp",EDGE,"E70.0.0");var subQ16=sQuery(id+"F7.wireOp",EDGE,"E68.0.2");var subQ17=sQuery(id+"F7.wireOp",EDGE,"E68.0.1");var subQ18=sQuery(id+"F7.wireOp",EDGE,"E68.0.0");Q14=makeQuery(id+"F14.imprint","IMPRINT",FACE,{"disambiguationData":[TD([[makeQuery(id+"F14.imprint","IMPRINT",EDGE,{"derivedFrom":makeQuery(id+"F12.boolean.opBoolean","INTERSECT",EDGE,{"derivedFrom":[makeQuery(id+"F10.boolean.opBoolean","MERGE",FACE,{"derivedFrom":[makeQuery(id+"F9.boolean.opBoolean","MERGE",FACE,{"derivedFrom":[makeQuery(id+"F8.opExtrude","CAP_FACE",FACE,{"disambiguationData":[OSD([subQ18,subQ17,subQ16,subQ15,subQ14,subQ13,subQ12,subQ11,subQ10,subQ9,subQ8,subQ7,subQ6,subQ5,subQ4,subQ3,subQ2,subQ1,sQuery(id+"F7.wireOp",EDGE,"E84.0.0"),sQuery(id+"F7.wireOp",EDGE,"E84.0.1"),sQuery(id+"F7.wireOp",EDGE,"E84.0.3"),sQuery(id+"F7.wireOp",EDGE,"E86.0.0"),sQuery(id+"F7.wireOp",EDGE,"E86.0.1"),sQuery(id+"F7.wireOp",EDGE,"E86.0.3"),sQuery(id+"F7.wireOp",EDGE,"E91.0.1"),sQuery(id+"F7.wireOp",EDGE,"E91.0.2"),sQuery(id+"F7.wireOp",EDGE,"E91.0.3"),sQuery(id+"F7.wireOp",EDGE,"E94.0.1"),sQuery(id+"F7.wireOp",EDGE,"E94.0.2"),sQuery(id+"F7.wireOp",EDGE,"E94.0.3"),sQuery(id+"F7.wireOp",EDGE,"E99.0.0"),sQuery(id+"F7.wireOp",EDGE,"E99.0.1"),sQuery(id+"F7.wireOp",EDGE,"E99.0.3"),sQuery(id+"F7.wireOp",EDGE,"E100.0.1"),sQuery(id+"F7.wireOp",EDGE,"E100.0.2"),sQuery(id+"F7.wireOp",EDGE,"E100.0.3"),sQuery(id+"F7.wireOp",EDGE,"E102.0"),sQuery(id+"F7.wireOp",EDGE,"E102.1"),sQuery(id+"F7.wireOp",EDGE,"E102.2"),sQuery(id+"F7.wireOp",EDGE,"E102.3"),sQuery(id+"F7.wireOp",EDGE,"E103.left"),sQuery(id+"F7.wireOp",EDGE,"E103.right"),sQuery(id+"F7.wireOp",EDGE,"E105"),subQ0])],"isStart":false}),makeQuery(id+"F9.opExtrude","CAP_FACE",FACE,{"disambiguationData":[OSD([sQuery(id+"F1.wireOp",EDGE,"E16"),sQuery(id+"F1.wireOp",EDGE,"E23.top"),sQuery(id+"F1.wireOp",EDGE,"E23.left"),sQuery(id+"F1.wireOp",EDGE,"E31.trimOffspring"),sQuery(id+"F1.wireOp",EDGE,"E40.MirrorCS")])],"isStart":false}),makeQuery(id+"F9.opExtrude","CAP_FACE",FACE,{"disambiguationData":[OSD([sQuery(id+"F1.wireOp",EDGE,"E20.MirrorC"),sQuery(id+"F1.wireOp",EDGE,"E27.MirrorCS"),sQuery(id+"F1.wireOp",EDGE,"E32.trimOffspring"),sQuery(id+"F1.wireOp",EDGE,"E33.1.0.8"),sQuery(id+"F1.wireOp",EDGE,"E33.1.0.15"),sQuery(id+"F1.wireOp",EDGE,"E33.1.0.22"),sQuery(id+"F1.wireOp",EDGE,"E41.MirrorCS")])],"isStart":false}),makeQuery(id+"F9.opExtrude","CAP_FACE",FACE,{"disambiguationData":[OSD([sQuery(id+"F1.wireOp",EDGE,"E33.1.0.9"),sQuery(id+"F1.wireOp",EDGE,"E33.1.0.11"),sQuery(id+"F1.wireOp",EDGE,"E33.1.0.19"),sQuery(id+"F1.wireOp",EDGE,"E33.2.0.8"),sQuery(id+"F1.wireOp",EDGE,"E33.2.0.15"),sQuery(id+"F1.wireOp",EDGE,"E33.2.0.22"),sQuery(id+"F1.wireOp",EDGE,"E42.MirrorCS")])],"isStart":false}),makeQuery(id+"F9.opExtrude","CAP_FACE",FACE,{"disambiguationData":[OSD([sQuery(id+"F1.wireOp",EDGE,"E33.2.0.9"),sQuery(id+"F1.wireOp",EDGE,"E33.2.0.11"),sQuery(id+"F1.wireOp",EDGE,"E33.2.0.19"),sQuery(id+"F1.wireOp",EDGE,"E33.3.0.8"),sQuery(id+"F1.wireOp",EDGE,"E33.3.0.15"),sQuery(id+"F1.wireOp",EDGE,"E33.3.0.22"),sQuery(id+"F1.wireOp",EDGE,"E43.MirrorCS")])],"isStart":false}),makeQuery(id+"F9.opExtrude","CAP_FACE",FACE,{"disambiguationData":[OSD([sQuery(id+"F1.wireOp",EDGE,"E33.3.0.9"),sQuery(id+"F1.wireOp",EDGE,"E33.3.0.11"),sQuery(id+"F1.wireOp",EDGE,"E33.3.0.19"),sQuery(id+"F1.wireOp",EDGE,"E33.4.0.8"),sQuery(id+"F1.wireOp",EDGE,"E33.4.0.15"),sQuery(id+"F1.wireOp",EDGE,"E33.4.0.22"),sQuery(id+"F1.wireOp",EDGE,"E44.MirrorCS")])],"isStart":false}),makeQuery(id+"F9.opExtrude","CAP_FACE",FACE,{"disambiguationData":[OSD([sQuery(id+"F1.wireOp",EDGE,"E33.4.0.4"),sQuery(id+"F1.wireOp",EDGE,"E33.4.0.9"),sQuery(id+"F1.wireOp",EDGE,"E33.4.0.11"),sQuery(id+"F1.wireOp",EDGE,"E33.4.0.19"),sQuery(id+"F1.wireOp",EDGE,"E45.MirrorCS")])],"isStart":false})]}),makeQuery(id+"F10.opExtrude","CAP_FACE",FACE,{"disambiguationData":[OSD([subQ18,subQ17,subQ16,sQuery(id+"F7.wireOp",EDGE,"E75.0"),sQuery(id+"F7.wireOp",EDGE,"E76.0"),subQ0])],"isStart":false}),makeQuery(id+"F10.opExtrude","CAP_FACE",FACE,{"disambiguationData":[OSD([sQuery(id+"F7.wireOp",EDGE,"E69.0"),subQ15,subQ14,subQ13,sQuery(id+"F7.wireOp",EDGE,"E74.0"),subQ0])],"isStart":false}),makeQuery(id+"F10.opExtrude","CAP_FACE",FACE,{"disambiguationData":[OSD([subQ12,subQ11,subQ10,sQuery(id+"F7.wireOp",EDGE,"E79.0"),sQuery(id+"F7.wireOp",EDGE,"E80.0"),subQ0])],"isStart":false}),makeQuery(id+"F10.opExtrude","CAP_FACE",FACE,{"disambiguationData":[OSD([subQ9,subQ8,subQ7,sQuery(id+"F7.wireOp",EDGE,"E81.0"),sQuery(id+"F7.wireOp",EDGE,"E82.0"),subQ0])],"isStart":false}),makeQuery(id+"F10.opExtrude","CAP_FACE",FACE,{"disambiguationData":[OSD([subQ6,subQ5,subQ4,sQuery(id+"F7.wireOp",EDGE,"E83.0"),subQ0])],"isStart":false}),makeQuery(id+"F10.opExtrude","CAP_FACE",FACE,{"disambiguationData":[OSD([sQuery(id+"F7.wireOp",EDGE,"E77.0"),subQ3,subQ2,subQ1,subQ0])],"isStart":false})]}),makeQuery(id+"F12.opExtrude","SWEPT_FACE",FACE,{"disambiguationData":[OSD([sQuery(id+"F11.wireOp",EDGE,"E110")])]})]})}),1.0]])]});}
            var Q15;
            Q15=makeQuery(id+"F14.imprint","IMPRINT",FACE,{"disambiguationData":[TD([[makeQuery(id+"F14.imprint","IMPRINT",EDGE,{"derivedFrom":makeQuery(id+"F10.opExtrude","CAP_EDGE",EDGE,{"disambiguationData":[OSD([sQuery(id+"F7.wireOp",EDGE,"E82.0")])],"isStart":false})}),1.0]])]});
            var Q16;
            Q16=makeQuery(id+"F14.imprint","IMPRINT",FACE,{"disambiguationData":[TD([[makeQuery(id+"F14.imprint","IMPRINT",EDGE,{"derivedFrom":makeQuery(id+"F10.opExtrude","CAP_EDGE",EDGE,{"disambiguationData":[OSD([sQuery(id+"F7.wireOp",EDGE,"E79.0")])],"isStart":false})}),1.0]])]});
            var Q17;
            Q17=makeQuery(id+"F14.imprint","IMPRINT",FACE,{"disambiguationData":[TD([[makeQuery(id+"F14.imprint","IMPRINT",EDGE,{"derivedFrom":makeQuery(id+"F10.opExtrude","CAP_EDGE",EDGE,{"disambiguationData":[OSD([sQuery(id+"F7.wireOp",EDGE,"E81.0")])],"isStart":false})}),1.0]])]});
            var Q18;
            {var subQ0=sQuery(id+"F7.wireOp",EDGE,"E109");var subQ1=sQuery(id+"F7.wireOp",EDGE,"E78.0.2");var subQ2=sQuery(id+"F7.wireOp",EDGE,"E78.0.1");var subQ3=sQuery(id+"F7.wireOp",EDGE,"E78.0.0");var subQ4=sQuery(id+"F7.wireOp",EDGE,"E73.0.2");var subQ5=sQuery(id+"F7.wireOp",EDGE,"E73.0.1");var subQ6=sQuery(id+"F7.wireOp",EDGE,"E73.0.0");var subQ7=sQuery(id+"F7.wireOp",EDGE,"E72.0.2");var subQ8=sQuery(id+"F7.wireOp",EDGE,"E72.0.1");var subQ9=sQuery(id+"F7.wireOp",EDGE,"E72.0.0");var subQ10=sQuery(id+"F7.wireOp",EDGE,"E71.0.3");var subQ11=sQuery(id+"F7.wireOp",EDGE,"E71.0.2");var subQ12=sQuery(id+"F7.wireOp",EDGE,"E71.0.1");var subQ13=sQuery(id+"F7.wireOp",EDGE,"E70.0.2");var subQ14=sQuery(id+"F7.wireOp",EDGE,"E70.0.1");var subQ15=sQuery(id+"F7.wireOp",EDGE,"E70.0.0");var subQ16=sQuery(id+"F7.wireOp",EDGE,"E68.0.2");var subQ17=sQuery(id+"F7.wireOp",EDGE,"E68.0.1");var subQ18=sQuery(id+"F7.wireOp",EDGE,"E68.0.0");Q18=makeQuery(id+"F14.imprint","IMPRINT",FACE,{"disambiguationData":[TD([[makeQuery(id+"F14.imprint","IMPRINT",EDGE,{"derivedFrom":makeQuery(id+"F12.boolean.opBoolean","INTERSECT",EDGE,{"derivedFrom":[makeQuery(id+"F10.boolean.opBoolean","MERGE",FACE,{"derivedFrom":[makeQuery(id+"F9.boolean.opBoolean","MERGE",FACE,{"derivedFrom":[makeQuery(id+"F8.opExtrude","CAP_FACE",FACE,{"disambiguationData":[OSD([subQ18,subQ17,subQ16,subQ15,subQ14,subQ13,subQ12,subQ11,subQ10,subQ9,subQ8,subQ7,subQ6,subQ5,subQ4,subQ3,subQ2,subQ1,sQuery(id+"F7.wireOp",EDGE,"E84.0.0"),sQuery(id+"F7.wireOp",EDGE,"E84.0.1"),sQuery(id+"F7.wireOp",EDGE,"E84.0.3"),sQuery(id+"F7.wireOp",EDGE,"E86.0.0"),sQuery(id+"F7.wireOp",EDGE,"E86.0.1"),sQuery(id+"F7.wireOp",EDGE,"E86.0.3"),sQuery(id+"F7.wireOp",EDGE,"E91.0.1"),sQuery(id+"F7.wireOp",EDGE,"E91.0.2"),sQuery(id+"F7.wireOp",EDGE,"E91.0.3"),sQuery(id+"F7.wireOp",EDGE,"E94.0.1"),sQuery(id+"F7.wireOp",EDGE,"E94.0.2"),sQuery(id+"F7.wireOp",EDGE,"E94.0.3"),sQuery(id+"F7.wireOp",EDGE,"E99.0.0"),sQuery(id+"F7.wireOp",EDGE,"E99.0.1"),sQuery(id+"F7.wireOp",EDGE,"E99.0.3"),sQuery(id+"F7.wireOp",EDGE,"E100.0.1"),sQuery(id+"F7.wireOp",EDGE,"E100.0.2"),sQuery(id+"F7.wireOp",EDGE,"E100.0.3"),sQuery(id+"F7.wireOp",EDGE,"E102.0"),sQuery(id+"F7.wireOp",EDGE,"E102.1"),sQuery(id+"F7.wireOp",EDGE,"E102.2"),sQuery(id+"F7.wireOp",EDGE,"E102.3"),sQuery(id+"F7.wireOp",EDGE,"E103.left"),sQuery(id+"F7.wireOp",EDGE,"E103.right"),sQuery(id+"F7.wireOp",EDGE,"E105"),subQ0])],"isStart":false}),makeQuery(id+"F9.opExtrude","CAP_FACE",FACE,{"disambiguationData":[OSD([sQuery(id+"F1.wireOp",EDGE,"E16"),sQuery(id+"F1.wireOp",EDGE,"E23.top"),sQuery(id+"F1.wireOp",EDGE,"E23.left"),sQuery(id+"F1.wireOp",EDGE,"E31.trimOffspring"),sQuery(id+"F1.wireOp",EDGE,"E40.MirrorCS")])],"isStart":false}),makeQuery(id+"F9.opExtrude","CAP_FACE",FACE,{"disambiguationData":[OSD([sQuery(id+"F1.wireOp",EDGE,"E20.MirrorC"),sQuery(id+"F1.wireOp",EDGE,"E27.MirrorCS"),sQuery(id+"F1.wireOp",EDGE,"E32.trimOffspring"),sQuery(id+"F1.wireOp",EDGE,"E33.1.0.8"),sQuery(id+"F1.wireOp",EDGE,"E33.1.0.15"),sQuery(id+"F1.wireOp",EDGE,"E33.1.0.22"),sQuery(id+"F1.wireOp",EDGE,"E41.MirrorCS")])],"isStart":false}),makeQuery(id+"F9.opExtrude","CAP_FACE",FACE,{"disambiguationData":[OSD([sQuery(id+"F1.wireOp",EDGE,"E33.1.0.9"),sQuery(id+"F1.wireOp",EDGE,"E33.1.0.11"),sQuery(id+"F1.wireOp",EDGE,"E33.1.0.19"),sQuery(id+"F1.wireOp",EDGE,"E33.2.0.8"),sQuery(id+"F1.wireOp",EDGE,"E33.2.0.15"),sQuery(id+"F1.wireOp",EDGE,"E33.2.0.22"),sQuery(id+"F1.wireOp",EDGE,"E42.MirrorCS")])],"isStart":false}),makeQuery(id+"F9.opExtrude","CAP_FACE",FACE,{"disambiguationData":[OSD([sQuery(id+"F1.wireOp",EDGE,"E33.2.0.9"),sQuery(id+"F1.wireOp",EDGE,"E33.2.0.11"),sQuery(id+"F1.wireOp",EDGE,"E33.2.0.19"),sQuery(id+"F1.wireOp",EDGE,"E33.3.0.8"),sQuery(id+"F1.wireOp",EDGE,"E33.3.0.15"),sQuery(id+"F1.wireOp",EDGE,"E33.3.0.22"),sQuery(id+"F1.wireOp",EDGE,"E43.MirrorCS")])],"isStart":false}),makeQuery(id+"F9.opExtrude","CAP_FACE",FACE,{"disambiguationData":[OSD([sQuery(id+"F1.wireOp",EDGE,"E33.3.0.9"),sQuery(id+"F1.wireOp",EDGE,"E33.3.0.11"),sQuery(id+"F1.wireOp",EDGE,"E33.3.0.19"),sQuery(id+"F1.wireOp",EDGE,"E33.4.0.8"),sQuery(id+"F1.wireOp",EDGE,"E33.4.0.15"),sQuery(id+"F1.wireOp",EDGE,"E33.4.0.22"),sQuery(id+"F1.wireOp",EDGE,"E44.MirrorCS")])],"isStart":false}),makeQuery(id+"F9.opExtrude","CAP_FACE",FACE,{"disambiguationData":[OSD([sQuery(id+"F1.wireOp",EDGE,"E33.4.0.4"),sQuery(id+"F1.wireOp",EDGE,"E33.4.0.9"),sQuery(id+"F1.wireOp",EDGE,"E33.4.0.11"),sQuery(id+"F1.wireOp",EDGE,"E33.4.0.19"),sQuery(id+"F1.wireOp",EDGE,"E45.MirrorCS")])],"isStart":false})]}),makeQuery(id+"F10.opExtrude","CAP_FACE",FACE,{"disambiguationData":[OSD([subQ18,subQ17,subQ16,sQuery(id+"F7.wireOp",EDGE,"E75.0"),sQuery(id+"F7.wireOp",EDGE,"E76.0"),subQ0])],"isStart":false}),makeQuery(id+"F10.opExtrude","CAP_FACE",FACE,{"disambiguationData":[OSD([sQuery(id+"F7.wireOp",EDGE,"E69.0"),subQ15,subQ14,subQ13,sQuery(id+"F7.wireOp",EDGE,"E74.0"),subQ0])],"isStart":false}),makeQuery(id+"F10.opExtrude","CAP_FACE",FACE,{"disambiguationData":[OSD([subQ12,subQ11,subQ10,sQuery(id+"F7.wireOp",EDGE,"E79.0"),sQuery(id+"F7.wireOp",EDGE,"E80.0"),subQ0])],"isStart":false}),makeQuery(id+"F10.opExtrude","CAP_FACE",FACE,{"disambiguationData":[OSD([subQ9,subQ8,subQ7,sQuery(id+"F7.wireOp",EDGE,"E81.0"),sQuery(id+"F7.wireOp",EDGE,"E82.0"),subQ0])],"isStart":false}),makeQuery(id+"F10.opExtrude","CAP_FACE",FACE,{"disambiguationData":[OSD([subQ6,subQ5,subQ4,sQuery(id+"F7.wireOp",EDGE,"E83.0"),subQ0])],"isStart":false}),makeQuery(id+"F10.opExtrude","CAP_FACE",FACE,{"disambiguationData":[OSD([sQuery(id+"F7.wireOp",EDGE,"E77.0"),subQ3,subQ2,subQ1,subQ0])],"isStart":false})]}),makeQuery(id+"F12.opExtrude","SWEPT_FACE",FACE,{"disambiguationData":[OSD([sQuery(id+"F11.wireOp",EDGE,"E116.MirrorC")])]})]})}),-1.0]])]});}
            var Q19;
            Q19=makeQuery(id+"F14.imprint","IMPRINT",FACE,{"disambiguationData":[TD([[makeQuery(id+"F14.imprint","IMPRINT",EDGE,{"derivedFrom":makeQuery(id+"F9.opExtrude","CAP_EDGE",EDGE,{"disambiguationData":[OSD([sQuery(id+"F1.wireOp",EDGE,"E33.2.0.19")])],"isStart":false})}),-1.0]])]});
            var Q20;
            Q20=makeQuery(id+"F14.imprint","IMPRINT",FACE,{"disambiguationData":[TD([[makeQuery(id+"F14.imprint","IMPRINT",EDGE,{"derivedFrom":makeQuery(id+"F9.opExtrude","CAP_EDGE",EDGE,{"disambiguationData":[OSD([sQuery(id+"F1.wireOp",EDGE,"E33.2.0.22")])],"isStart":false})}),1.0]])]});
            var Q21;
            Q21=makeQuery(id+"F14.imprint","IMPRINT",FACE,{"disambiguationData":[TD([[makeQuery(id+"F14.imprint","IMPRINT",EDGE,{"derivedFrom":makeQuery(id+"F9.opExtrude","CAP_EDGE",EDGE,{"disambiguationData":[OSD([sQuery(id+"F1.wireOp",EDGE,"E33.4.0.19")])],"isStart":false})}),-1.0]])]});
            var Q22;
            Q22=makeQuery(id+"F14.imprint","IMPRINT",FACE,{"disambiguationData":[TD([[makeQuery(id+"F14.imprint","IMPRINT",EDGE,{"derivedFrom":makeQuery(id+"F9.opExtrude","CAP_EDGE",EDGE,{"disambiguationData":[OSD([sQuery(id+"F1.wireOp",EDGE,"E16")])],"isStart":false})}),1.0]])]});
            var Q23;
            Q23=makeQuery(id+"F14.imprint","IMPRINT",FACE,{"disambiguationData":[TD([[makeQuery(id+"F14.imprint","IMPRINT",EDGE,{"derivedFrom":makeQuery(id+"F9.opExtrude","CAP_EDGE",EDGE,{"disambiguationData":[OSD([sQuery(id+"F1.wireOp",EDGE,"E33.3.0.19")])],"isStart":false})}),-1.0]])]});
            var Q24;
            Q24=makeQuery(id+"F14.imprint","IMPRINT",FACE,{"disambiguationData":[TD([[makeQuery(id+"F14.imprint","IMPRINT",EDGE,{"derivedFrom":makeQuery(id+"F9.opExtrude","CAP_EDGE",EDGE,{"disambiguationData":[OSD([sQuery(id+"F1.wireOp",EDGE,"E33.1.0.22")])],"isStart":false})}),1.0]])]});
            var Q25;
            Q25=makeQuery(id+"F14.imprint","IMPRINT",FACE,{"disambiguationData":[TD([[makeQuery(id+"F14.imprint","IMPRINT",EDGE,{"derivedFrom":makeQuery(id+"F9.opExtrude","CAP_EDGE",EDGE,{"disambiguationData":[OSD([sQuery(id+"F1.wireOp",EDGE,"E33.3.0.22")])],"isStart":false})}),1.0]])]});
            var Q26;
            Q26=makeQuery(id+"F14.imprint","IMPRINT",FACE,{"disambiguationData":[TD([[makeQuery(id+"F14.imprint","IMPRINT",EDGE,{"derivedFrom":makeQuery(id+"F9.opExtrude","CAP_EDGE",EDGE,{"disambiguationData":[OSD([sQuery(id+"F1.wireOp",EDGE,"E20.MirrorC")])],"isStart":false})}),-1.0]])]});
            var Q27;
            {var subQ0=sQuery(id+"F7.wireOp",EDGE,"E109");var subQ1=sQuery(id+"F7.wireOp",EDGE,"E78.0.2");var subQ2=sQuery(id+"F7.wireOp",EDGE,"E78.0.1");var subQ3=sQuery(id+"F7.wireOp",EDGE,"E78.0.0");var subQ4=sQuery(id+"F7.wireOp",EDGE,"E73.0.2");var subQ5=sQuery(id+"F7.wireOp",EDGE,"E73.0.1");var subQ6=sQuery(id+"F7.wireOp",EDGE,"E73.0.0");var subQ7=sQuery(id+"F7.wireOp",EDGE,"E72.0.2");var subQ8=sQuery(id+"F7.wireOp",EDGE,"E72.0.1");var subQ9=sQuery(id+"F7.wireOp",EDGE,"E72.0.0");var subQ10=sQuery(id+"F7.wireOp",EDGE,"E71.0.3");var subQ11=sQuery(id+"F7.wireOp",EDGE,"E71.0.2");var subQ12=sQuery(id+"F7.wireOp",EDGE,"E71.0.1");var subQ13=sQuery(id+"F7.wireOp",EDGE,"E70.0.2");var subQ14=sQuery(id+"F7.wireOp",EDGE,"E70.0.1");var subQ15=sQuery(id+"F7.wireOp",EDGE,"E70.0.0");var subQ16=sQuery(id+"F7.wireOp",EDGE,"E68.0.2");var subQ17=sQuery(id+"F7.wireOp",EDGE,"E68.0.1");var subQ18=sQuery(id+"F7.wireOp",EDGE,"E68.0.0");Q27=makeQuery(id+"F14.imprint","IMPRINT",FACE,{"disambiguationData":[TD([[makeQuery(id+"F14.imprint","IMPRINT",EDGE,{"derivedFrom":makeQuery(id+"F12.boolean.opBoolean","INTERSECT",EDGE,{"derivedFrom":[makeQuery(id+"F10.boolean.opBoolean","MERGE",FACE,{"derivedFrom":[makeQuery(id+"F9.boolean.opBoolean","MERGE",FACE,{"derivedFrom":[makeQuery(id+"F8.opExtrude","CAP_FACE",FACE,{"disambiguationData":[OSD([subQ18,subQ17,subQ16,subQ15,subQ14,subQ13,subQ12,subQ11,subQ10,subQ9,subQ8,subQ7,subQ6,subQ5,subQ4,subQ3,subQ2,subQ1,sQuery(id+"F7.wireOp",EDGE,"E84.0.0"),sQuery(id+"F7.wireOp",EDGE,"E84.0.1"),sQuery(id+"F7.wireOp",EDGE,"E84.0.3"),sQuery(id+"F7.wireOp",EDGE,"E86.0.0"),sQuery(id+"F7.wireOp",EDGE,"E86.0.1"),sQuery(id+"F7.wireOp",EDGE,"E86.0.3"),sQuery(id+"F7.wireOp",EDGE,"E91.0.1"),sQuery(id+"F7.wireOp",EDGE,"E91.0.2"),sQuery(id+"F7.wireOp",EDGE,"E91.0.3"),sQuery(id+"F7.wireOp",EDGE,"E94.0.1"),sQuery(id+"F7.wireOp",EDGE,"E94.0.2"),sQuery(id+"F7.wireOp",EDGE,"E94.0.3"),sQuery(id+"F7.wireOp",EDGE,"E99.0.0"),sQuery(id+"F7.wireOp",EDGE,"E99.0.1"),sQuery(id+"F7.wireOp",EDGE,"E99.0.3"),sQuery(id+"F7.wireOp",EDGE,"E100.0.1"),sQuery(id+"F7.wireOp",EDGE,"E100.0.2"),sQuery(id+"F7.wireOp",EDGE,"E100.0.3"),sQuery(id+"F7.wireOp",EDGE,"E102.0"),sQuery(id+"F7.wireOp",EDGE,"E102.1"),sQuery(id+"F7.wireOp",EDGE,"E102.2"),sQuery(id+"F7.wireOp",EDGE,"E102.3"),sQuery(id+"F7.wireOp",EDGE,"E103.left"),sQuery(id+"F7.wireOp",EDGE,"E103.right"),sQuery(id+"F7.wireOp",EDGE,"E105"),subQ0])],"isStart":false}),makeQuery(id+"F9.opExtrude","CAP_FACE",FACE,{"disambiguationData":[OSD([sQuery(id+"F1.wireOp",EDGE,"E16"),sQuery(id+"F1.wireOp",EDGE,"E23.top"),sQuery(id+"F1.wireOp",EDGE,"E23.left"),sQuery(id+"F1.wireOp",EDGE,"E31.trimOffspring"),sQuery(id+"F1.wireOp",EDGE,"E40.MirrorCS")])],"isStart":false}),makeQuery(id+"F9.opExtrude","CAP_FACE",FACE,{"disambiguationData":[OSD([sQuery(id+"F1.wireOp",EDGE,"E20.MirrorC"),sQuery(id+"F1.wireOp",EDGE,"E27.MirrorCS"),sQuery(id+"F1.wireOp",EDGE,"E32.trimOffspring"),sQuery(id+"F1.wireOp",EDGE,"E33.1.0.8"),sQuery(id+"F1.wireOp",EDGE,"E33.1.0.15"),sQuery(id+"F1.wireOp",EDGE,"E33.1.0.22"),sQuery(id+"F1.wireOp",EDGE,"E41.MirrorCS")])],"isStart":false}),makeQuery(id+"F9.opExtrude","CAP_FACE",FACE,{"disambiguationData":[OSD([sQuery(id+"F1.wireOp",EDGE,"E33.1.0.9"),sQuery(id+"F1.wireOp",EDGE,"E33.1.0.11"),sQuery(id+"F1.wireOp",EDGE,"E33.1.0.19"),sQuery(id+"F1.wireOp",EDGE,"E33.2.0.8"),sQuery(id+"F1.wireOp",EDGE,"E33.2.0.15"),sQuery(id+"F1.wireOp",EDGE,"E33.2.0.22"),sQuery(id+"F1.wireOp",EDGE,"E42.MirrorCS")])],"isStart":false}),makeQuery(id+"F9.opExtrude","CAP_FACE",FACE,{"disambiguationData":[OSD([sQuery(id+"F1.wireOp",EDGE,"E33.2.0.9"),sQuery(id+"F1.wireOp",EDGE,"E33.2.0.11"),sQuery(id+"F1.wireOp",EDGE,"E33.2.0.19"),sQuery(id+"F1.wireOp",EDGE,"E33.3.0.8"),sQuery(id+"F1.wireOp",EDGE,"E33.3.0.15"),sQuery(id+"F1.wireOp",EDGE,"E33.3.0.22"),sQuery(id+"F1.wireOp",EDGE,"E43.MirrorCS")])],"isStart":false}),makeQuery(id+"F9.opExtrude","CAP_FACE",FACE,{"disambiguationData":[OSD([sQuery(id+"F1.wireOp",EDGE,"E33.3.0.9"),sQuery(id+"F1.wireOp",EDGE,"E33.3.0.11"),sQuery(id+"F1.wireOp",EDGE,"E33.3.0.19"),sQuery(id+"F1.wireOp",EDGE,"E33.4.0.8"),sQuery(id+"F1.wireOp",EDGE,"E33.4.0.15"),sQuery(id+"F1.wireOp",EDGE,"E33.4.0.22"),sQuery(id+"F1.wireOp",EDGE,"E44.MirrorCS")])],"isStart":false}),makeQuery(id+"F9.opExtrude","CAP_FACE",FACE,{"disambiguationData":[OSD([sQuery(id+"F1.wireOp",EDGE,"E33.4.0.4"),sQuery(id+"F1.wireOp",EDGE,"E33.4.0.9"),sQuery(id+"F1.wireOp",EDGE,"E33.4.0.11"),sQuery(id+"F1.wireOp",EDGE,"E33.4.0.19"),sQuery(id+"F1.wireOp",EDGE,"E45.MirrorCS")])],"isStart":false})]}),makeQuery(id+"F10.opExtrude","CAP_FACE",FACE,{"disambiguationData":[OSD([subQ18,subQ17,subQ16,sQuery(id+"F7.wireOp",EDGE,"E75.0"),sQuery(id+"F7.wireOp",EDGE,"E76.0"),subQ0])],"isStart":false}),makeQuery(id+"F10.opExtrude","CAP_FACE",FACE,{"disambiguationData":[OSD([sQuery(id+"F7.wireOp",EDGE,"E69.0"),subQ15,subQ14,subQ13,sQuery(id+"F7.wireOp",EDGE,"E74.0"),subQ0])],"isStart":false}),makeQuery(id+"F10.opExtrude","CAP_FACE",FACE,{"disambiguationData":[OSD([subQ12,subQ11,subQ10,sQuery(id+"F7.wireOp",EDGE,"E79.0"),sQuery(id+"F7.wireOp",EDGE,"E80.0"),subQ0])],"isStart":false}),makeQuery(id+"F10.opExtrude","CAP_FACE",FACE,{"disambiguationData":[OSD([subQ9,subQ8,subQ7,sQuery(id+"F7.wireOp",EDGE,"E81.0"),sQuery(id+"F7.wireOp",EDGE,"E82.0"),subQ0])],"isStart":false}),makeQuery(id+"F10.opExtrude","CAP_FACE",FACE,{"disambiguationData":[OSD([subQ6,subQ5,subQ4,sQuery(id+"F7.wireOp",EDGE,"E83.0"),subQ0])],"isStart":false}),makeQuery(id+"F10.opExtrude","CAP_FACE",FACE,{"disambiguationData":[OSD([sQuery(id+"F7.wireOp",EDGE,"E77.0"),subQ3,subQ2,subQ1,subQ0])],"isStart":false})]}),makeQuery(id+"F12.opExtrude","SWEPT_FACE",FACE,{"disambiguationData":[OSD([sQuery(id+"F11.wireOp",EDGE,"E117.MirrorC")])]})]})}),1.0]])]});}
            var Q28;
            Q28=makeQuery(id+"F14.imprint","IMPRINT",FACE,{"disambiguationData":[TD([[makeQuery(id+"F14.imprint","IMPRINT",EDGE,{"derivedFrom":makeQuery(id+"F9.opExtrude","CAP_EDGE",EDGE,{"disambiguationData":[OSD([sQuery(id+"F1.wireOp",EDGE,"E33.1.0.19")])],"isStart":false})}),-1.0]])]});
            var Q29;
            {var subQ0=sQuery(id+"F7.wireOp",EDGE,"E109");var subQ1=sQuery(id+"F7.wireOp",EDGE,"E78.0.2");var subQ2=sQuery(id+"F7.wireOp",EDGE,"E78.0.1");var subQ3=sQuery(id+"F7.wireOp",EDGE,"E78.0.0");var subQ4=sQuery(id+"F7.wireOp",EDGE,"E73.0.2");var subQ5=sQuery(id+"F7.wireOp",EDGE,"E73.0.1");var subQ6=sQuery(id+"F7.wireOp",EDGE,"E73.0.0");var subQ7=sQuery(id+"F7.wireOp",EDGE,"E72.0.2");var subQ8=sQuery(id+"F7.wireOp",EDGE,"E72.0.1");var subQ9=sQuery(id+"F7.wireOp",EDGE,"E72.0.0");var subQ10=sQuery(id+"F7.wireOp",EDGE,"E71.0.3");var subQ11=sQuery(id+"F7.wireOp",EDGE,"E71.0.2");var subQ12=sQuery(id+"F7.wireOp",EDGE,"E71.0.1");var subQ13=sQuery(id+"F7.wireOp",EDGE,"E70.0.2");var subQ14=sQuery(id+"F7.wireOp",EDGE,"E70.0.1");var subQ15=sQuery(id+"F7.wireOp",EDGE,"E70.0.0");var subQ16=sQuery(id+"F7.wireOp",EDGE,"E68.0.2");var subQ17=sQuery(id+"F7.wireOp",EDGE,"E68.0.1");var subQ18=sQuery(id+"F7.wireOp",EDGE,"E68.0.0");Q29=makeQuery(id+"F14.imprint","IMPRINT",FACE,{"disambiguationData":[TD([[makeQuery(id+"F14.imprint","IMPRINT",EDGE,{"derivedFrom":makeQuery(id+"F12.boolean.opBoolean","INTERSECT",EDGE,{"derivedFrom":[makeQuery(id+"F10.boolean.opBoolean","MERGE",FACE,{"derivedFrom":[makeQuery(id+"F9.boolean.opBoolean","MERGE",FACE,{"derivedFrom":[makeQuery(id+"F8.opExtrude","CAP_FACE",FACE,{"disambiguationData":[OSD([subQ18,subQ17,subQ16,subQ15,subQ14,subQ13,subQ12,subQ11,subQ10,subQ9,subQ8,subQ7,subQ6,subQ5,subQ4,subQ3,subQ2,subQ1,sQuery(id+"F7.wireOp",EDGE,"E84.0.0"),sQuery(id+"F7.wireOp",EDGE,"E84.0.1"),sQuery(id+"F7.wireOp",EDGE,"E84.0.3"),sQuery(id+"F7.wireOp",EDGE,"E86.0.0"),sQuery(id+"F7.wireOp",EDGE,"E86.0.1"),sQuery(id+"F7.wireOp",EDGE,"E86.0.3"),sQuery(id+"F7.wireOp",EDGE,"E91.0.1"),sQuery(id+"F7.wireOp",EDGE,"E91.0.2"),sQuery(id+"F7.wireOp",EDGE,"E91.0.3"),sQuery(id+"F7.wireOp",EDGE,"E94.0.1"),sQuery(id+"F7.wireOp",EDGE,"E94.0.2"),sQuery(id+"F7.wireOp",EDGE,"E94.0.3"),sQuery(id+"F7.wireOp",EDGE,"E99.0.0"),sQuery(id+"F7.wireOp",EDGE,"E99.0.1"),sQuery(id+"F7.wireOp",EDGE,"E99.0.3"),sQuery(id+"F7.wireOp",EDGE,"E100.0.1"),sQuery(id+"F7.wireOp",EDGE,"E100.0.2"),sQuery(id+"F7.wireOp",EDGE,"E100.0.3"),sQuery(id+"F7.wireOp",EDGE,"E102.0"),sQuery(id+"F7.wireOp",EDGE,"E102.1"),sQuery(id+"F7.wireOp",EDGE,"E102.2"),sQuery(id+"F7.wireOp",EDGE,"E102.3"),sQuery(id+"F7.wireOp",EDGE,"E103.left"),sQuery(id+"F7.wireOp",EDGE,"E103.right"),sQuery(id+"F7.wireOp",EDGE,"E105"),subQ0])],"isStart":false}),makeQuery(id+"F9.opExtrude","CAP_FACE",FACE,{"disambiguationData":[OSD([sQuery(id+"F1.wireOp",EDGE,"E16"),sQuery(id+"F1.wireOp",EDGE,"E23.top"),sQuery(id+"F1.wireOp",EDGE,"E23.left"),sQuery(id+"F1.wireOp",EDGE,"E31.trimOffspring"),sQuery(id+"F1.wireOp",EDGE,"E40.MirrorCS")])],"isStart":false}),makeQuery(id+"F9.opExtrude","CAP_FACE",FACE,{"disambiguationData":[OSD([sQuery(id+"F1.wireOp",EDGE,"E20.MirrorC"),sQuery(id+"F1.wireOp",EDGE,"E27.MirrorCS"),sQuery(id+"F1.wireOp",EDGE,"E32.trimOffspring"),sQuery(id+"F1.wireOp",EDGE,"E33.1.0.8"),sQuery(id+"F1.wireOp",EDGE,"E33.1.0.15"),sQuery(id+"F1.wireOp",EDGE,"E33.1.0.22"),sQuery(id+"F1.wireOp",EDGE,"E41.MirrorCS")])],"isStart":false}),makeQuery(id+"F9.opExtrude","CAP_FACE",FACE,{"disambiguationData":[OSD([sQuery(id+"F1.wireOp",EDGE,"E33.1.0.9"),sQuery(id+"F1.wireOp",EDGE,"E33.1.0.11"),sQuery(id+"F1.wireOp",EDGE,"E33.1.0.19"),sQuery(id+"F1.wireOp",EDGE,"E33.2.0.8"),sQuery(id+"F1.wireOp",EDGE,"E33.2.0.15"),sQuery(id+"F1.wireOp",EDGE,"E33.2.0.22"),sQuery(id+"F1.wireOp",EDGE,"E42.MirrorCS")])],"isStart":false}),makeQuery(id+"F9.opExtrude","CAP_FACE",FACE,{"disambiguationData":[OSD([sQuery(id+"F1.wireOp",EDGE,"E33.2.0.9"),sQuery(id+"F1.wireOp",EDGE,"E33.2.0.11"),sQuery(id+"F1.wireOp",EDGE,"E33.2.0.19"),sQuery(id+"F1.wireOp",EDGE,"E33.3.0.8"),sQuery(id+"F1.wireOp",EDGE,"E33.3.0.15"),sQuery(id+"F1.wireOp",EDGE,"E33.3.0.22"),sQuery(id+"F1.wireOp",EDGE,"E43.MirrorCS")])],"isStart":false}),makeQuery(id+"F9.opExtrude","CAP_FACE",FACE,{"disambiguationData":[OSD([sQuery(id+"F1.wireOp",EDGE,"E33.3.0.9"),sQuery(id+"F1.wireOp",EDGE,"E33.3.0.11"),sQuery(id+"F1.wireOp",EDGE,"E33.3.0.19"),sQuery(id+"F1.wireOp",EDGE,"E33.4.0.8"),sQuery(id+"F1.wireOp",EDGE,"E33.4.0.15"),sQuery(id+"F1.wireOp",EDGE,"E33.4.0.22"),sQuery(id+"F1.wireOp",EDGE,"E44.MirrorCS")])],"isStart":false}),makeQuery(id+"F9.opExtrude","CAP_FACE",FACE,{"disambiguationData":[OSD([sQuery(id+"F1.wireOp",EDGE,"E33.4.0.4"),sQuery(id+"F1.wireOp",EDGE,"E33.4.0.9"),sQuery(id+"F1.wireOp",EDGE,"E33.4.0.11"),sQuery(id+"F1.wireOp",EDGE,"E33.4.0.19"),sQuery(id+"F1.wireOp",EDGE,"E45.MirrorCS")])],"isStart":false})]}),makeQuery(id+"F10.opExtrude","CAP_FACE",FACE,{"disambiguationData":[OSD([subQ18,subQ17,subQ16,sQuery(id+"F7.wireOp",EDGE,"E75.0"),sQuery(id+"F7.wireOp",EDGE,"E76.0"),subQ0])],"isStart":false}),makeQuery(id+"F10.opExtrude","CAP_FACE",FACE,{"disambiguationData":[OSD([sQuery(id+"F7.wireOp",EDGE,"E69.0"),subQ15,subQ14,subQ13,sQuery(id+"F7.wireOp",EDGE,"E74.0"),subQ0])],"isStart":false}),makeQuery(id+"F10.opExtrude","CAP_FACE",FACE,{"disambiguationData":[OSD([subQ12,subQ11,subQ10,sQuery(id+"F7.wireOp",EDGE,"E79.0"),sQuery(id+"F7.wireOp",EDGE,"E80.0"),subQ0])],"isStart":false}),makeQuery(id+"F10.opExtrude","CAP_FACE",FACE,{"disambiguationData":[OSD([subQ9,subQ8,subQ7,sQuery(id+"F7.wireOp",EDGE,"E81.0"),sQuery(id+"F7.wireOp",EDGE,"E82.0"),subQ0])],"isStart":false}),makeQuery(id+"F10.opExtrude","CAP_FACE",FACE,{"disambiguationData":[OSD([subQ6,subQ5,subQ4,sQuery(id+"F7.wireOp",EDGE,"E83.0"),subQ0])],"isStart":false}),makeQuery(id+"F10.opExtrude","CAP_FACE",FACE,{"disambiguationData":[OSD([sQuery(id+"F7.wireOp",EDGE,"E77.0"),subQ3,subQ2,subQ1,subQ0])],"isStart":false})]}),makeQuery(id+"F12.opExtrude","SWEPT_FACE",FACE,{"disambiguationData":[OSD([sQuery(id+"F11.wireOp",EDGE,"E115.MirrorC")])]})]})}),-1.0]])]});}
            var Q30;
            Q30=makeQuery(id+"F14.imprint","IMPRINT",FACE,{"disambiguationData":[TD([[makeQuery(id+"F14.imprint","IMPRINT",EDGE,{"derivedFrom":makeQuery(id+"F9.opExtrude","CAP_EDGE",EDGE,{"disambiguationData":[OSD([sQuery(id+"F1.wireOp",EDGE,"E33.4.0.22")])],"isStart":false})}),1.0]])]});
            extrude(context, id + "F15", {"entities" : qUnion([Q0, Q1, Q2, Q3, Q4, Q5, Q6, Q7, Q8, Q9, Q10, Q11, Q12, Q13, Q14, Q15, Q16, Q17, Q18, Q19, Q20, Q21, Q22, Q23, Q24, Q25, Q26, Q27, Q28, Q29, Q30]), "depth" : 10 * mm, "offsetDistance" : 25 * mm});
        }
    });
